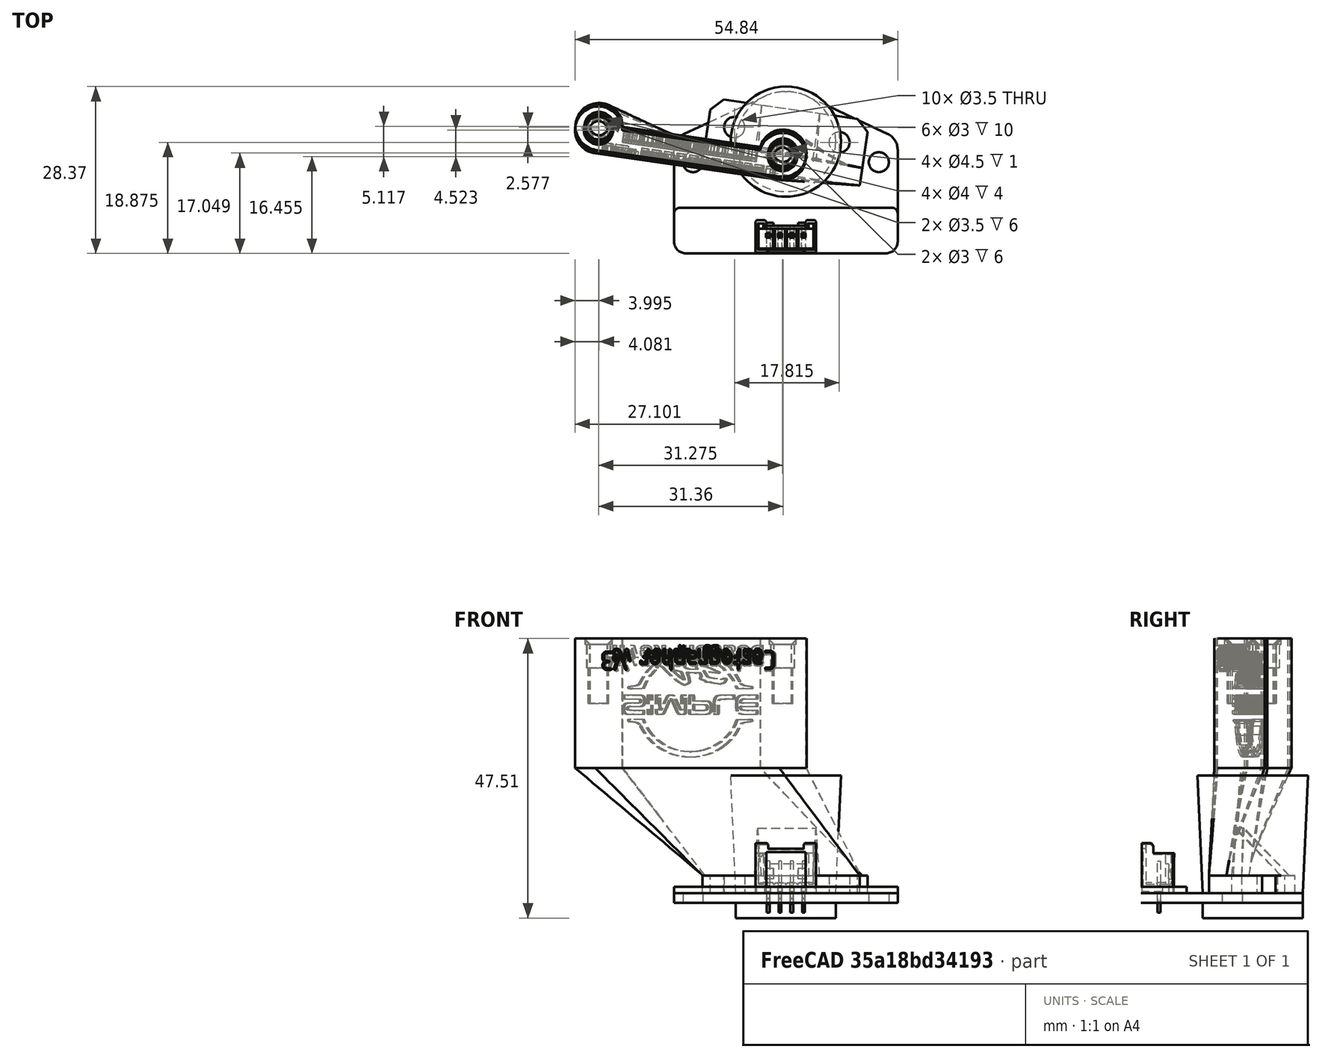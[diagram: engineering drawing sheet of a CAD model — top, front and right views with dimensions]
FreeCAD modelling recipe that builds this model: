
FCSTD DOCUMENT  (FreeCAD 1.2R20260324 (Git shallow))
Label: CartoBeaconMountEnder3V3SE
License: All rights reserved
LicenseURL: http://en.wikipedia.org/wiki/All_rights_reserved
objects: Sketcher::SketchObject×44, PartDesign::Pocket×19, PartDesign::Pad×10, PartDesign::AdditiveLoft×10, PartDesign::Chamfer×8, App::Point×7, Part::Feature×5, Part::Part2DObjectPython×5, PartDesign::Body×5, App::Part×2
note: 244 computed .brp shape members not serialized (recipe doc carries the construction recipe); baked Part::Feature solids carry a one-line shape summary decoded from their .brp

FEATURE [Part::Feature] Part__Feature  label="BeaconG_LP"
  shape: bbox 17 x 17 x 2.6 mm, 4 faces (baked)
FEATURE [Part::Feature] Part__Feature001  label="BeaconG_LP001"
  shape: bbox 18.75 x 18.75 x 20 mm, 4 faces (baked)
FEATURE [Part::Feature] Part__Feature002  label="BeaconG_LP002"
  shape: bbox 38 x 7.762 x 1.1 mm, 10 faces (baked)
FEATURE [Part::Feature] Part__Feature003  label="BeaconG_LP003"
  shape: bbox 38 x 27.5 x 1.611 mm, 18 faces (baked)
FEATURE [App::Part] BeaconG_LP  label="BeaconG_LP004"
  Group = -> [Part__Feature,Part__Feature001,Part__Feature002,Part__Feature003]
  Origin = -> Origin
  Placement = pos=(0,0,0) rot=(0,0,1;1.5708rad)
FEATURE [App::Point] Origin001
  Role = Origin
FEATURE [Part::Feature] Part__Feature004  label="353620450"
  Placement = pos=(4e-16,-16.1345,4.25) rot=(0,0.707107,0.707107;3.14159rad)
  shape: bbox 10.3 x 5.55 x 11.8 mm, 178 faces (baked)
FEATURE [App::Part] Beacon_Rev_H_Assm  label="Beacon Rev H Assm"
  Group = -> [BeaconG_LP,Part__Feature004]
  Origin = -> Origin002
  Placement = pos=(-14.8882,-23.3593,-85.3) rot=(0,0,1;4.71239rad)
FEATURE [App::Point] Origin003
  Role = Origin
FEATURE [App::Point] Origin009  label="Origin011"
  Role = Origin
FEATURE [Sketcher::SketchObject] Sketch011
  ArcFitTolerance = 1e-06
  AttachmentOffset = pos=(-16,-2,43.3) rot=(0,0,1;0rad)
  AttachmentSupport = -> [Origin008]
  ExternalTypes = [0,0]
  FullyConstrained = true
  MakeInternals = false
  MapMode = 5
  Placement = pos=(-16,-2,43.3) rot=(0,0,1;0rad)
  _ExternalGeoVersion = 0
  sketch-geometry (4):
    g0: ArcOfCircle CenterX=-15.8 CenterY=0 CenterZ=0 NormalX=0 NormalY=0 NormalZ=1 AngleXU=0 Radius=4 StartAngle=0.125328 EndAngle=4.71239
    g1: ArcOfCircle CenterX=15.8 CenterY=0 CenterZ=0 NormalX=0 NormalY=0 NormalZ=1 AngleXU=0 Radius=4 StartAngle=4.71239 EndAngle=9.29945
    g2: LineSegment StartX=-15.8 StartY=-4 StartZ=0 EndX=15.8 EndY=-4 EndZ=0
    g3: LineSegment StartX=-11.8314 StartY=0.5 StartZ=0 EndX=11.8314 EndY=0.5 EndZ=0
  constraints (12):
    c: DistanceX(g0,g1) = 31.6
    c: Vertical(g2,g1)
    c: Symmetric(g0,g1,g-2)
    c: Symmetric(g2,g2,g-2)
    c: Horizontal(g3)
    c: PointOnObject(g0,g-1)
    c: DistanceY(g2,g3) = 4.5
    c: DistanceY(g2,g0) = 4
    c: Coincident(g3,g1)
    c: Coincident(g1,g2)
    c: Coincident(g3,g0)
    c: Coincident(g0,g2)
FEATURE [Sketcher::SketchObject] Sketch013
  ArcFitTolerance = 1e-06
  AttachmentSupport = -> [Origin008]
  ExternalTypes = [0]
  FullyConstrained = true
  MakeInternals = false
  MapMode = 5
  _ExternalGeoVersion = 0
  expr: Constraints[11] = 5 + 3.5 / 2
  sketch-geometry (6):
    g0: LineSegment StartX=-13.5 StartY=-5.575 StartZ=0 EndX=13.5 EndY=-5.575 EndZ=0
    g1: LineSegment StartX=13.5 StartY=-5.575 StartZ=0 EndX=13.5 EndY=5.575 EndZ=0
    g2: Circle CenterX=-9 CenterY=1.175 CenterZ=0 NormalX=0 NormalY=0 NormalZ=1 AngleXU=0 Radius=1.75
    g3: Circle CenterX=9 CenterY=1.175 CenterZ=0 NormalX=0 NormalY=0 NormalZ=1 AngleXU=0 Radius=1.75
    g4: LineSegment StartX=-13.5 StartY=-5.575 StartZ=0 EndX=-13.5 EndY=5.575 EndZ=0
    g5: LineSegment StartX=-13.5 StartY=5.575 StartZ=0 EndX=13.5 EndY=5.575 EndZ=0
  constraints (16):
    c: Equal(g3,g2)
    c: Diameter(g3) = 3.5
    c: Symmetric(g2,g3,g-2)
    c: Coincident(g4,g0)
    c: Vertical(g4)
    c: Coincident(g5,g4)
    c: Coincident(g5,g1)
    c: Horizontal(g5)
    c: DistanceY(g4,g4) = 11.15
    c: Symmetric(g4,g0,g-1)
    c: DistanceX(g5,g5) = 27
    c: DistanceY(g0,g2) = 6.75
    c: DistanceX(g2,g3) = 18
    c: Horizontal(g0)
    c: Vertical(g1)
    c: Coincident(g1,g0)
FEATURE [PartDesign::Pad] Pad008
  Direction = (0,0,1)
  Length = 22
  Length2 = 10
  Profile = -> Sketch011
  ReferenceAxis = -> Sketch011 [N_Axis]
  Refine = true
  Reversed = true
  SideType = 0
  Suppressed = false
  Type = 0
  Type2 = 0
FEATURE [PartDesign::Pad] Pad009
  BaseFeature = -> Pad008
  Direction = (0,0,1)
  Length = 3
  Length2 = 10
  Profile = -> Sketch013
  ReferenceAxis = -> Sketch013 [N_Axis]
  Refine = true
  SideType = 0
  Suppressed = false
  Type = 0
  Type2 = 0
FEATURE [Sketcher::SketchObject] Sketch014
  ArcFitTolerance = 1e-06
  AttachmentSupport = -> [Pad009]
  ExternalGeometry = -> [Pad009]
  ExternalTypes = [0,0]
  FullyConstrained = true
  MakeInternals = false
  MapMode = 5
  Placement = pos=(0,0,3) rot=(0,0,1;0rad)
  _ExternalGeoVersion = 0
  sketch-geometry (4):
    g0: LineSegment StartX=-13.5 StartY=-5.575 StartZ=0 EndX=13.5 EndY=-5.575 EndZ=0
    g1: LineSegment StartX=13.5 StartY=-5.575 StartZ=0 EndX=13.5 EndY=-2.575 EndZ=0
    g2: LineSegment StartX=13.5 StartY=-2.575 StartZ=0 EndX=-13.5 EndY=-2.575 EndZ=0
    g3: LineSegment StartX=-13.5 StartY=-2.575 StartZ=0 EndX=-13.5 EndY=-5.575 EndZ=0
  constraints (11):
    c: Coincident(g0,g1)
    c: Coincident(g1,g2)
    c: Coincident(g2,g3)
    c: Coincident(g3,g0)
    c: Horizontal(g2)
    c: Vertical(g1)
    c: Vertical(g3)
    c: DistanceY(g1,g1) = 3
    c: Horizontal(g0)
    c: Coincident(g0,g-3)
    c: PointOnObject(g2,g-4)
FEATURE [Sketcher::SketchObject] MirroredSketch001
  ArcFitTolerance = 1e-06
  AttachmentOffset = pos=(14,-18,0) rot=(0,0,1;0rad)
  AttachmentSupport = -> [Pad009]
  ExternalTypes = [0]
  FullyConstrained = false
  MakeInternals = false
  MapMode = 5
  Placement = pos=(-14,-1.5,-18) rot=(0,0.707107,0.707107;3.14159rad)
  _ExternalGeoVersion = 0
  sketch-geometry (160):
    g0: BSplineCurve PolesCount=4 KnotsCount=2 Degree=3 IsPeriodic=0
    g1: BSplineCurve PolesCount=4 KnotsCount=2 Degree=3 IsPeriodic=0
    g2: BSplineCurve PolesCount=4 KnotsCount=2 Degree=3 IsPeriodic=0
    g3: BSplineCurve PolesCount=4 KnotsCount=2 Degree=3 IsPeriodic=0
    g4: BSplineCurve PolesCount=4 KnotsCount=2 Degree=3 IsPeriodic=0
    g5: BSplineCurve PolesCount=4 KnotsCount=2 Degree=3 IsPeriodic=0
    g6: BSplineCurve PolesCount=4 KnotsCount=2 Degree=3 IsPeriodic=0
    g7: BSplineCurve PolesCount=4 KnotsCount=2 Degree=3 IsPeriodic=0
    g8: BSplineCurve PolesCount=4 KnotsCount=2 Degree=3 IsPeriodic=0
    g9: BSplineCurve PolesCount=4 KnotsCount=2 Degree=3 IsPeriodic=0
    g10: BSplineCurve PolesCount=4 KnotsCount=2 Degree=3 IsPeriodic=0
    g11: BSplineCurve PolesCount=4 KnotsCount=2 Degree=3 IsPeriodic=0
    g12: BSplineCurve PolesCount=4 KnotsCount=2 Degree=3 IsPeriodic=0
    g13: BSplineCurve PolesCount=4 KnotsCount=2 Degree=3 IsPeriodic=0
    g14: BSplineCurve PolesCount=4 KnotsCount=2 Degree=3 IsPeriodic=0
    g15: BSplineCurve PolesCount=4 KnotsCount=2 Degree=3 IsPeriodic=0
    g16: BSplineCurve PolesCount=4 KnotsCount=2 Degree=3 IsPeriodic=0
    g17: BSplineCurve PolesCount=4 KnotsCount=2 Degree=3 IsPeriodic=0
    g18: BSplineCurve PolesCount=4 KnotsCount=2 Degree=3 IsPeriodic=0
    g19: BSplineCurve PolesCount=4 KnotsCount=2 Degree=3 IsPeriodic=0
    g20: BSplineCurve PolesCount=4 KnotsCount=2 Degree=3 IsPeriodic=0
    g21: BSplineCurve PolesCount=4 KnotsCount=2 Degree=3 IsPeriodic=0
    g22: BSplineCurve PolesCount=4 KnotsCount=2 Degree=3 IsPeriodic=0
    g23: BSplineCurve PolesCount=4 KnotsCount=2 Degree=3 IsPeriodic=0
    g24: BSplineCurve PolesCount=4 KnotsCount=2 Degree=3 IsPeriodic=0
    g25: BSplineCurve PolesCount=4 KnotsCount=2 Degree=3 IsPeriodic=0
    g26: BSplineCurve PolesCount=4 KnotsCount=2 Degree=3 IsPeriodic=0
    g27: BSplineCurve PolesCount=4 KnotsCount=2 Degree=3 IsPeriodic=0
    g28: BSplineCurve PolesCount=4 KnotsCount=2 Degree=3 IsPeriodic=0
    g29: BSplineCurve PolesCount=4 KnotsCount=2 Degree=3 IsPeriodic=0
    g30: BSplineCurve PolesCount=4 KnotsCount=2 Degree=3 IsPeriodic=0
    g31: BSplineCurve PolesCount=4 KnotsCount=2 Degree=3 IsPeriodic=0
    g32: BSplineCurve PolesCount=4 KnotsCount=2 Degree=3 IsPeriodic=0
    g33: BSplineCurve PolesCount=4 KnotsCount=2 Degree=3 IsPeriodic=0
    g34: BSplineCurve PolesCount=4 KnotsCount=2 Degree=3 IsPeriodic=0
    g35: BSplineCurve PolesCount=4 KnotsCount=2 Degree=3 IsPeriodic=0
    g36: BSplineCurve PolesCount=4 KnotsCount=2 Degree=3 IsPeriodic=0
    g37: BSplineCurve PolesCount=4 KnotsCount=2 Degree=3 IsPeriodic=0
    g38: BSplineCurve PolesCount=4 KnotsCount=2 Degree=3 IsPeriodic=0
    g39: BSplineCurve PolesCount=4 KnotsCount=2 Degree=3 IsPeriodic=0
    g40: BSplineCurve PolesCount=4 KnotsCount=2 Degree=3 IsPeriodic=0
    g41: BSplineCurve PolesCount=4 KnotsCount=2 Degree=3 IsPeriodic=0
    g42: BSplineCurve PolesCount=4 KnotsCount=2 Degree=3 IsPeriodic=0
    g43: BSplineCurve PolesCount=4 KnotsCount=2 Degree=3 IsPeriodic=0
    g44: BSplineCurve PolesCount=4 KnotsCount=2 Degree=3 IsPeriodic=0
    g45: BSplineCurve PolesCount=4 KnotsCount=2 Degree=3 IsPeriodic=0
    g46: BSplineCurve PolesCount=4 KnotsCount=2 Degree=3 IsPeriodic=0
    g47: BSplineCurve PolesCount=4 KnotsCount=2 Degree=3 IsPeriodic=0
    g48: BSplineCurve PolesCount=4 KnotsCount=2 Degree=3 IsPeriodic=0
    g49: BSplineCurve PolesCount=4 KnotsCount=2 Degree=3 IsPeriodic=0
    g50: BSplineCurve PolesCount=4 KnotsCount=2 Degree=3 IsPeriodic=0
    g51: BSplineCurve PolesCount=4 KnotsCount=2 Degree=3 IsPeriodic=0
    g52: BSplineCurve PolesCount=4 KnotsCount=2 Degree=3 IsPeriodic=0
    g53: BSplineCurve PolesCount=4 KnotsCount=2 Degree=3 IsPeriodic=0
    g54: BSplineCurve PolesCount=4 KnotsCount=2 Degree=3 IsPeriodic=0
    g55: BSplineCurve PolesCount=4 KnotsCount=2 Degree=3 IsPeriodic=0
    g56: BSplineCurve PolesCount=4 KnotsCount=2 Degree=3 IsPeriodic=0
    g57: BSplineCurve PolesCount=4 KnotsCount=2 Degree=3 IsPeriodic=0
    g58: BSplineCurve PolesCount=4 KnotsCount=2 Degree=3 IsPeriodic=0
    g59: BSplineCurve PolesCount=4 KnotsCount=2 Degree=3 IsPeriodic=0
    g60: BSplineCurve PolesCount=4 KnotsCount=2 Degree=3 IsPeriodic=0
    g61: BSplineCurve PolesCount=4 KnotsCount=2 Degree=3 IsPeriodic=0
    g62: BSplineCurve PolesCount=4 KnotsCount=2 Degree=3 IsPeriodic=0
    g63: BSplineCurve PolesCount=4 KnotsCount=2 Degree=3 IsPeriodic=0
    g64: BSplineCurve PolesCount=4 KnotsCount=2 Degree=3 IsPeriodic=0
    g65: BSplineCurve PolesCount=4 KnotsCount=2 Degree=3 IsPeriodic=0
    g66: BSplineCurve PolesCount=4 KnotsCount=2 Degree=3 IsPeriodic=0
    g67: BSplineCurve PolesCount=4 KnotsCount=2 Degree=3 IsPeriodic=0
    g68: BSplineCurve PolesCount=4 KnotsCount=2 Degree=3 IsPeriodic=0
    g69: BSplineCurve PolesCount=4 KnotsCount=2 Degree=3 IsPeriodic=0
    g70: BSplineCurve PolesCount=4 KnotsCount=2 Degree=3 IsPeriodic=0
    g71: BSplineCurve PolesCount=4 KnotsCount=2 Degree=3 IsPeriodic=0
    g72: BSplineCurve PolesCount=4 KnotsCount=2 Degree=3 IsPeriodic=0
    g73: BSplineCurve PolesCount=4 KnotsCount=2 Degree=3 IsPeriodic=0
    g74: BSplineCurve PolesCount=4 KnotsCount=2 Degree=3 IsPeriodic=0
    g75: BSplineCurve PolesCount=4 KnotsCount=2 Degree=3 IsPeriodic=0
    g76: BSplineCurve PolesCount=4 KnotsCount=2 Degree=3 IsPeriodic=0
    g77: BSplineCurve PolesCount=4 KnotsCount=2 Degree=3 IsPeriodic=0
    g78: BSplineCurve PolesCount=4 KnotsCount=2 Degree=3 IsPeriodic=0
    g79: BSplineCurve PolesCount=4 KnotsCount=2 Degree=3 IsPeriodic=0
    g80: BSplineCurve PolesCount=4 KnotsCount=2 Degree=3 IsPeriodic=0
    g81: BSplineCurve PolesCount=4 KnotsCount=2 Degree=3 IsPeriodic=0
    g82: BSplineCurve PolesCount=4 KnotsCount=2 Degree=3 IsPeriodic=0
    g83: BSplineCurve PolesCount=4 KnotsCount=2 Degree=3 IsPeriodic=0
    g84: BSplineCurve PolesCount=4 KnotsCount=2 Degree=3 IsPeriodic=0
    g85: BSplineCurve PolesCount=4 KnotsCount=2 Degree=3 IsPeriodic=0
    g86: BSplineCurve PolesCount=4 KnotsCount=2 Degree=3 IsPeriodic=0
    g87: BSplineCurve PolesCount=4 KnotsCount=2 Degree=3 IsPeriodic=0
    g88: BSplineCurve PolesCount=4 KnotsCount=2 Degree=3 IsPeriodic=0
    g89: BSplineCurve PolesCount=4 KnotsCount=2 Degree=3 IsPeriodic=0
    g90: BSplineCurve PolesCount=4 KnotsCount=2 Degree=3 IsPeriodic=0
    g91: BSplineCurve PolesCount=4 KnotsCount=2 Degree=3 IsPeriodic=0
    g92: BSplineCurve PolesCount=4 KnotsCount=2 Degree=3 IsPeriodic=0
    g93: BSplineCurve PolesCount=4 KnotsCount=2 Degree=3 IsPeriodic=0
    g94: BSplineCurve PolesCount=4 KnotsCount=2 Degree=3 IsPeriodic=0
    g95: BSplineCurve PolesCount=4 KnotsCount=2 Degree=3 IsPeriodic=0
    g96: BSplineCurve PolesCount=4 KnotsCount=2 Degree=3 IsPeriodic=0
    g97: BSplineCurve PolesCount=4 KnotsCount=2 Degree=3 IsPeriodic=0
    g98: BSplineCurve PolesCount=4 KnotsCount=2 Degree=3 IsPeriodic=0
    g99: BSplineCurve PolesCount=4 KnotsCount=2 Degree=3 IsPeriodic=0
    g100: BSplineCurve PolesCount=4 KnotsCount=2 Degree=3 IsPeriodic=0
    g101: BSplineCurve PolesCount=4 KnotsCount=2 Degree=3 IsPeriodic=0
    g102: BSplineCurve PolesCount=4 KnotsCount=2 Degree=3 IsPeriodic=0
    g103: BSplineCurve PolesCount=4 KnotsCount=2 Degree=3 IsPeriodic=0
    g104: BSplineCurve PolesCount=4 KnotsCount=2 Degree=3 IsPeriodic=0
    g105: BSplineCurve PolesCount=2 KnotsCount=2 Degree=1 IsPeriodic=0
    g106: BSplineCurve PolesCount=4 KnotsCount=2 Degree=3 IsPeriodic=0
    g107: BSplineCurve PolesCount=4 KnotsCount=2 Degree=3 IsPeriodic=0
    g108: BSplineCurve PolesCount=4 KnotsCount=2 Degree=3 IsPeriodic=0
    g109: BSplineCurve PolesCount=4 KnotsCount=2 Degree=3 IsPeriodic=0
    g110: BSplineCurve PolesCount=4 KnotsCount=2 Degree=3 IsPeriodic=0
    g111: BSplineCurve PolesCount=4 KnotsCount=2 Degree=3 IsPeriodic=0
    g112: BSplineCurve PolesCount=4 KnotsCount=2 Degree=3 IsPeriodic=0
    g113: BSplineCurve PolesCount=4 KnotsCount=2 Degree=3 IsPeriodic=0
    g114: BSplineCurve PolesCount=4 KnotsCount=2 Degree=3 IsPeriodic=0
    g115: BSplineCurve PolesCount=4 KnotsCount=2 Degree=3 IsPeriodic=0
    g116: BSplineCurve PolesCount=4 KnotsCount=2 Degree=3 IsPeriodic=0
    g117: BSplineCurve PolesCount=4 KnotsCount=2 Degree=3 IsPeriodic=0
    g118: BSplineCurve PolesCount=4 KnotsCount=2 Degree=3 IsPeriodic=0
    g119: BSplineCurve PolesCount=4 KnotsCount=2 Degree=3 IsPeriodic=0
    g120: BSplineCurve PolesCount=4 KnotsCount=2 Degree=3 IsPeriodic=0
    g121: BSplineCurve PolesCount=4 KnotsCount=2 Degree=3 IsPeriodic=0
    g122: BSplineCurve PolesCount=4 KnotsCount=2 Degree=3 IsPeriodic=0
    g123: BSplineCurve PolesCount=4 KnotsCount=2 Degree=3 IsPeriodic=0
    g124: BSplineCurve PolesCount=4 KnotsCount=2 Degree=3 IsPeriodic=0
    g125: BSplineCurve PolesCount=4 KnotsCount=2 Degree=3 IsPeriodic=0
    g126: BSplineCurve PolesCount=4 KnotsCount=2 Degree=3 IsPeriodic=0
    g127: BSplineCurve PolesCount=4 KnotsCount=2 Degree=3 IsPeriodic=0
    g128: BSplineCurve PolesCount=4 KnotsCount=2 Degree=3 IsPeriodic=0
    g129: BSplineCurve PolesCount=4 KnotsCount=2 Degree=3 IsPeriodic=0
    g130: BSplineCurve PolesCount=4 KnotsCount=2 Degree=3 IsPeriodic=0
    g131: BSplineCurve PolesCount=4 KnotsCount=2 Degree=3 IsPeriodic=0
    g132: BSplineCurve PolesCount=4 KnotsCount=2 Degree=3 IsPeriodic=0
    g133: BSplineCurve PolesCount=4 KnotsCount=2 Degree=3 IsPeriodic=0
    g134: BSplineCurve PolesCount=4 KnotsCount=2 Degree=3 IsPeriodic=0
    g135: BSplineCurve PolesCount=4 KnotsCount=2 Degree=3 IsPeriodic=0
    g136: BSplineCurve PolesCount=4 KnotsCount=2 Degree=3 IsPeriodic=0
    g137: BSplineCurve PolesCount=4 KnotsCount=2 Degree=3 IsPeriodic=0
    g138: BSplineCurve PolesCount=4 KnotsCount=2 Degree=3 IsPeriodic=0
    g139: BSplineCurve PolesCount=4 KnotsCount=2 Degree=3 IsPeriodic=0
    g140: BSplineCurve PolesCount=4 KnotsCount=2 Degree=3 IsPeriodic=0
    g141: BSplineCurve PolesCount=4 KnotsCount=2 Degree=3 IsPeriodic=0
    g142: BSplineCurve PolesCount=4 KnotsCount=2 Degree=3 IsPeriodic=0
    g143: BSplineCurve PolesCount=4 KnotsCount=2 Degree=3 IsPeriodic=0
    g144: BSplineCurve PolesCount=4 KnotsCount=2 Degree=3 IsPeriodic=0
    g145: BSplineCurve PolesCount=4 KnotsCount=2 Degree=3 IsPeriodic=0
    g146: BSplineCurve PolesCount=4 KnotsCount=2 Degree=3 IsPeriodic=0
    g147: BSplineCurve PolesCount=4 KnotsCount=2 Degree=3 IsPeriodic=0
    g148: BSplineCurve PolesCount=4 KnotsCount=2 Degree=3 IsPeriodic=0
    g149: BSplineCurve PolesCount=4 KnotsCount=2 Degree=3 IsPeriodic=0
    g150: BSplineCurve PolesCount=4 KnotsCount=2 Degree=3 IsPeriodic=0
    g151: BSplineCurve PolesCount=4 KnotsCount=2 Degree=3 IsPeriodic=0
    g152: BSplineCurve PolesCount=4 KnotsCount=2 Degree=3 IsPeriodic=0
    g153: BSplineCurve PolesCount=4 KnotsCount=2 Degree=3 IsPeriodic=0
    g154: BSplineCurve PolesCount=4 KnotsCount=2 Degree=3 IsPeriodic=0
    g155: BSplineCurve PolesCount=4 KnotsCount=2 Degree=3 IsPeriodic=0
    g156: BSplineCurve PolesCount=4 KnotsCount=2 Degree=3 IsPeriodic=0
    g157: BSplineCurve PolesCount=4 KnotsCount=2 Degree=3 IsPeriodic=0
    g158: BSplineCurve PolesCount=4 KnotsCount=2 Degree=3 IsPeriodic=0
    g159: BSplineCurve PolesCount=4 KnotsCount=2 Degree=3 IsPeriodic=0
  constraints (160):
    c: Coincident(g10,g11)
    c: Coincident(g4,g5)
    c: Coincident(g11,g12)
    c: Coincident(g0,g12)
    c: Coincident(g5,g6)
    c: Coincident(g9,g10)
    c: Coincident(g0,g1)
    c: Coincident(g8,g9)
    c: Coincident(g1,g2)
    c: Coincident(g3,g4)
    c: Coincident(g2,g3)
    c: Coincident(g7,g8)
    c: Coincident(g6,g7)
    c: Coincident(g79,g80)
    c: Coincident(g96,g97)
    c: Coincident(g109,g110)
    c: Coincident(g13,g26)
    c: Coincident(g110,g111)
    c: Coincident(g13,g14)
    c: Coincident(g136,g137)
    c: Coincident(g102,g103)
    c: Coincident(g82,g83)
    c: Coincident(g137,g138)
    c: Coincident(g103,g104)
    c: Coincident(g78,g79)
    c: Coincident(g83,g84)
    c: Coincident(g80,g81)
    c: Coincident(g25,g26)
    c: Coincident(g95,g96)
    c: Coincident(g108,g109)
    c: Coincident(g73,g81)
    c: Coincident(g14,g15)
    c: Coincident(g111,g112)
    c: Coincident(g127,g131)
    c: Coincident(g127,g128)
    c: Coincident(g87,g88)
    c: Coincident(g91,g92)
    c: Coincident(g112,g113)
    c: Coincident(g15,g16)
    c: Coincident(g130,g131)
    c: Coincident(g97,g98)
    c: Coincident(g88,g89)
    c: Coincident(g84,g85)
    c: Coincident(g92,g93)
    c: Coincident(g113,g114)
    c: Coincident(g16,g17)
    c: Coincident(g17,g18)
    c: Coincident(g114,g115)
    c: Coincident(g82,g100)
    c: Coincident(g129,g130)
    c: Coincident(g128,g129)
    c: Coincident(g73,g74)
    c: Coincident(g107,g108)
    c: Coincident(g135,g136)
    c: Coincident(g18,g19)
    c: Coincident(g19,g20)
    c: Coincident(g106,g107)
    c: Coincident(g24,g25)
    c: Coincident(g99,g100)
    c: Coincident(g106,g120)
    c: Coincident(g74,g75)
    c: Coincident(g75,g76)
    c: Coincident(g138,g139)
    c: Coincident(g119,g120)
    c: Coincident(g139,g140)
    c: Coincident(g132,g140)
    c: Coincident(g20,g21)
    c: Coincident(g98,g99)
    c: Coincident(g118,g119)
    c: Coincident(g132,g133)
    c: Coincident(g21,g22)
    c: Coincident(g115,g116)
    c: Coincident(g90,g91)
    c: Coincident(g89,g90)
    c: Coincident(g77,g78)
    c: Coincident(g134,g135)
    c: Coincident(g85,g86)
    c: Coincident(g86,g87)
    c: Coincident(g23,g24)
    c: Coincident(g104,g105)
    c: Coincident(g101,g102)
    c: Coincident(g94,g95)
    c: Coincident(g117,g118)
    c: Coincident(g101,g105)
    c: Coincident(g22,g23)
    c: Coincident(g93,g94)
    c: Coincident(g76,g77)
    c: Coincident(g133,g134)
    c: Coincident(g116,g117)
    c: Coincident(g148,g149)
    c: Coincident(g157,g158)
    c: Coincident(g158,g159)
    c: Coincident(g147,g148)
    c: Coincident(g146,g147)
    c: Coincident(g156,g157)
    c: Coincident(g149,g150)
    c: Coincident(g57,g58)
    c: Coincident(g155,g156)
    c: Coincident(g46,g47)
    c: Coincident(g56,g57)
    c: Coincident(g47,g48)
    c: Coincident(g48,g49)
    c: Coincident(g45,g46)
    c: Coincident(g150,g151)
    c: Coincident(g55,g56)
    c: Coincident(g49,g50)
    c: Coincident(g122,g123)
    c: Coincident(g43,g44)
    c: Coincident(g44,g45)
    c: Coincident(g54,g55)
    c: Coincident(g123,g124)
    c: Coincident(g42,g43)
    c: Coincident(g50,g51)
    c: Coincident(g124,g125)
    c: Coincident(g53,g54)
    c: Coincident(g40,g41)
    c: Coincident(g52,g53)
    c: Coincident(g51,g52)
    c: Coincident(g58,g59)
    c: Coincident(g121,g122)
    c: Coincident(g39,g40)
    c: Coincident(g41,g42)
    c: Coincident(g38,g39)
    c: Coincident(g125,g126)
    c: Coincident(g121,g126)
    c: Coincident(g32,g33)
    c: Coincident(g31,g32)
    c: Coincident(g153,g159)
    c: Coincident(g37,g38)
    c: Coincident(g59,g60)
    c: Coincident(g67,g68)
    c: Coincident(g154,g155)
    c: Coincident(g66,g67)
    c: Coincident(g36,g37)
    c: Coincident(g60,g61)
    c: Coincident(g153,g154)
    c: Coincident(g65,g66)
    c: Coincident(g68,g69)
    c: Coincident(g71,g72)
    c: Coincident(g141,g144)
    c: Coincident(g33,g34)
    c: Coincident(g64,g65)
    c: Coincident(g145,g146)
    c: Coincident(g141,g142)
    c: Coincident(g63,g64)
    c: Coincident(g145,g152)
    c: Coincident(g143,g144)
    c: Coincident(g61,g62)
    c: Coincident(g34,g35)
    c: Coincident(g29,g30)
    c: Coincident(g35,g36)
    c: Coincident(g62,g63)
    c: Coincident(g27,g30)
    c: Coincident(g69,g70)
    c: Coincident(g70,g71)
    c: Coincident(g142,g143)
    c: Coincident(g28,g29)
    c: Coincident(g151,g152)
    c: Coincident(g27,g28)
    c: Coincident(g31,g72)
FEATURE [Part::Part2DObjectPython] Clone2D002  label="MirroredSketch001 (2D)"  # Draft 2D object (typed FeaturePython)
  AttachmentOffset = pos=(4.3,23,0) rot=(0,0,-1;1.5708rad)
  AttachmentSupport = -> [Pad009]
  ForceCompound = false
  Fuse = false
  MapMode = 5
  Objects = -> [MirroredSketch001]
  Placement = pos=(-4.3,-1.5,23) rot=(-0.57735,0.57735,0.57735;2.0944rad)
  Scale = (0.65,0.65,0.65)
FEATURE [PartDesign::Pocket] Pocket005
  BaseFeature = -> Pad009
  Direction = (0,-1,2e-16)
  Length = 2
  Length2 = 5
  Profile = -> Clone2D002
  ReferenceAxis = -> Clone2D002 [N_Axis]
  Refine = true
  SideType = 0
  Suppressed = false
  Type = 0
  Type2 = 0
FEATURE [PartDesign::AdditiveLoft] AdditiveLoft002
  BaseFeature = -> Pocket005
  Closed = false
  Profile = -> Sketch014
  Refine = true
  Ruled = false
  Sections = -> [Pocket005]
  Suppressed = false
FEATURE [PartDesign::Chamfer] Chamfer
  Angle = 45
  Base = -> AdditiveLoft002 [Edge468,Edge489]
  BaseFeature = -> AdditiveLoft002
  ChamferType = 0
  FlipDirection = false
  Refine = true
  Size = 2
  Size2 = 1
  SupportTransform = false
  Suppressed = false
  UseAllEdges = false
FEATURE [Sketcher::SketchObject] Sketch016
  ArcFitTolerance = 1e-06
  AttachmentSupport = -> [Chamfer]
  ExternalGeometry = -> [Chamfer]
  ExternalTypes = [0,0]
  FullyConstrained = true
  MakeInternals = false
  MapMode = 5
  Placement = pos=(0,0,43.3) rot=(0,0,1;0rad)
  _ExternalGeoVersion = 0
  sketch-geometry (2):
    g0: Circle CenterX=-31.8 CenterY=-2 CenterZ=0 NormalX=0 NormalY=0 NormalZ=1 AngleXU=0 Radius=1.5
    g1: Circle CenterX=-0.2 CenterY=-2 CenterZ=0 NormalX=0 NormalY=0 NormalZ=1 AngleXU=0 Radius=1.5
  constraints (4):
    c: Coincident(g0,g-4)
    c: Coincident(g1,g-3)
    c: Equal(g1,g0)
    c: Diameter(g0) = 3
FEATURE [PartDesign::Pocket] Pocket006
  BaseFeature = -> Chamfer
  Direction = (0,0,-1)
  Length = 11
  Length2 = 5
  Profile = -> Sketch016
  ReferenceAxis = -> Sketch016 [N_Axis]
  Refine = true
  SideType = 0
  Suppressed = false
  Type = 0
  Type2 = 0
FEATURE [PartDesign::Chamfer] Chamfer001
  Angle = 45
  Base = -> Pocket006 [Edge194,Edge193]
  BaseFeature = -> Pocket006
  ChamferType = 0
  FlipDirection = false
  Refine = true
  Size = 1
  Size2 = 1
  SupportTransform = false
  Suppressed = false
  UseAllEdges = false
FEATURE [Sketcher::SketchObject] Sketch017
  ArcFitTolerance = 1e-06
  AttachmentSupport = -> [Chamfer001]
  ExternalGeometry = -> [Chamfer001]
  ExternalTypes = [0,0]
  FullyConstrained = true
  MakeInternals = false
  MapMode = 5
  Placement = pos=(0,0,3) rot=(0,0,1;0rad)
  _ExternalGeoVersion = 0
  sketch-geometry (4):
    g0: LineSegment StartX=-5 StartY=-2.575 StartZ=0 EndX=5 EndY=-2.575 EndZ=0
    g1: LineSegment StartX=5 StartY=-2.575 StartZ=0 EndX=5 EndY=5.575 EndZ=0
    g2: LineSegment StartX=5 StartY=5.575 StartZ=0 EndX=-5 EndY=5.575 EndZ=0
    g3: LineSegment StartX=-5 StartY=5.575 StartZ=0 EndX=-5 EndY=-2.575 EndZ=0
  constraints (11):
    c: Coincident(g0,g1)
    c: Coincident(g1,g2)
    c: Coincident(g2,g3)
    c: Coincident(g3,g0)
    c: Horizontal(g0)
    c: Vertical(g1)
    c: Vertical(g3)
    c: PointOnObject(g0,g-3)
    c: PointOnObject(g1,g-4)
    c: DistanceX(g2,g2) = 10
    c: Symmetric(g1,g2,g-2)
FEATURE [Sketcher::SketchObject] Sketch018
  ArcFitTolerance = 1e-06
  AttachmentSupport = -> [Chamfer001]
  ExternalGeometry = -> [Chamfer001]
  ExternalTypes = [0]
  FullyConstrained = true
  MakeInternals = false
  MapMode = 5
  Placement = pos=(1e-16,-2.74177,0.16106) rot=(0,0.727545,0.68606;3.14159rad)
  _ExternalGeoVersion = 0
  sketch-geometry (4):
    g0: LineSegment StartX=-5.5 StartY=10.9438 StartZ=0 EndX=-5.5 EndY=10.8438 EndZ=0
    g1: LineSegment StartX=-5.5 StartY=10.8438 StartZ=0 EndX=4.5 EndY=10.8438 EndZ=0
    g2: LineSegment StartX=4.5 StartY=10.8438 StartZ=0 EndX=4.5 EndY=10.9438 EndZ=0
    g3: LineSegment StartX=4.5 StartY=10.9438 StartZ=0 EndX=-5.5 EndY=10.9438 EndZ=0
  constraints (12):
    c: Coincident(g0,g1)
    c: Coincident(g1,g2)
    c: Coincident(g2,g3)
    c: Coincident(g3,g0)
    c: Vertical(g0)
    c: Vertical(g2)
    c: Horizontal(g1)
    c: Horizontal(g3)
    c: DistanceX(g3,g3) = 10
    c: DistanceY(g2,g2) = 0.1
    c: DistanceY(g-3,g0) = 8
    c: DistanceX(g-3,g0) = 8
FEATURE [PartDesign::AdditiveLoft] AdditiveLoft003
  BaseFeature = -> Chamfer001
  Closed = false
  Profile = -> Sketch017
  Refine = true
  Ruled = false
  Sections = -> [Sketch018]
  Suppressed = false
FEATURE [Sketcher::SketchObject] Sketch
  ArcFitTolerance = 1e-06
  AttachmentSupport = -> [AdditiveLoft003]
  ExternalGeometry = -> [AdditiveLoft003]
  ExternalTypes = [0,0]
  FullyConstrained = false
  MakeInternals = false
  MapMode = 5
  Placement = pos=(0,-6,0) rot=(1,0,0;1.5708rad)
  _ExternalGeoVersion = 0
  sketch-geometry (256):
    g0: LineSegment [constr] StartX=-3.2 StartY=42.193 StartZ=0 EndX=-28.8 EndY=42.193 EndZ=0
    g1: BSplineCurve PolesCount=3 KnotsCount=2 Degree=2 IsPeriodic=0
    g2: BSplineCurve PolesCount=3 KnotsCount=2 Degree=2 IsPeriodic=0
    g3: BSplineCurve PolesCount=3 KnotsCount=2 Degree=2 IsPeriodic=0
    g4: LineSegment StartX=-4.39844 StartY=38.9376 StartZ=0 EndX=-3.86003 EndY=38.9376 EndZ=0
    g5: BSplineCurve PolesCount=3 KnotsCount=2 Degree=2 IsPeriodic=0
    g6: BSplineCurve PolesCount=3 KnotsCount=2 Degree=2 IsPeriodic=0
    g7: LineSegment StartX=-3.46115 StartY=39.3364 StartZ=0 EndX=-3.46115 EndY=40.703 EndZ=0
    g8: BSplineCurve PolesCount=3 KnotsCount=2 Degree=2 IsPeriodic=0
    g9: BSplineCurve PolesCount=3 KnotsCount=2 Degree=2 IsPeriodic=0
    g10: LineSegment StartX=-3.81889 StartY=41.118 StartZ=0 EndX=-4.4199 EndY=41.118 EndZ=0
    g11: BSplineCurve PolesCount=3 KnotsCount=2 Degree=2 IsPeriodic=0
    g12: BSplineCurve PolesCount=3 KnotsCount=2 Degree=2 IsPeriodic=0
    g13: LineSegment StartX=-4.41811 StartY=41.372 StartZ=0 EndX=-3.80816 EndY=41.372 EndZ=0
    g14: BSplineCurve PolesCount=3 KnotsCount=2 Degree=2 IsPeriodic=0
    g15: BSplineCurve PolesCount=3 KnotsCount=2 Degree=2 IsPeriodic=0
    g16: LineSegment StartX=-3.2 StartY=40.7173 StartZ=0 EndX=-3.2 EndY=39.3168 EndZ=0
    g17: BSplineCurve PolesCount=3 KnotsCount=2 Degree=2 IsPeriodic=0
    g18: BSplineCurve PolesCount=3 KnotsCount=2 Degree=2 IsPeriodic=0
    g19: BSplineCurve PolesCount=3 KnotsCount=2 Degree=2 IsPeriodic=0
    g20: BSplineCurve PolesCount=3 KnotsCount=2 Degree=2 IsPeriodic=0
    g21: BSplineCurve PolesCount=3 KnotsCount=2 Degree=2 IsPeriodic=0
    g22: BSplineCurve PolesCount=3 KnotsCount=2 Degree=2 IsPeriodic=0
    g23: LineSegment StartX=-5.44304 StartY=41.1073 StartZ=0 EndX=-5.99039 EndY=41.1073 EndZ=0
    g24: LineSegment StartX=-5.99039 StartY=41.1073 StartZ=0 EndX=-5.99039 EndY=40.5528 EndZ=0
    g25: LineSegment StartX=-5.99039 StartY=40.5528 StartZ=0 EndX=-5.46808 EndY=40.5528 EndZ=0
    g26: BSplineCurve PolesCount=3 KnotsCount=2 Degree=2 IsPeriodic=0
    g27: BSplineCurve PolesCount=3 KnotsCount=2 Degree=2 IsPeriodic=0
    g28: LineSegment StartX=-5.18189 StartY=39.4795 StartZ=0 EndX=-5.73818 EndY=39.4795 EndZ=0
    g29: BSplineCurve PolesCount=3 KnotsCount=2 Degree=2 IsPeriodic=0
    g30: BSplineCurve PolesCount=3 KnotsCount=2 Degree=2 IsPeriodic=0
    g31: LineSegment StartX=-6.25869 StartY=40.0072 StartZ=0 EndX=-6.25869 EndY=41.2092 EndZ=0
    g32: BSplineCurve PolesCount=3 KnotsCount=2 Degree=2 IsPeriodic=0
    g33: BSplineCurve PolesCount=3 KnotsCount=2 Degree=2 IsPeriodic=0
    g34: LineSegment StartX=-6.10486 StartY=41.3774 StartZ=0 EndX=-5.42515 EndY=41.3774 EndZ=0
    g35: BSplineCurve PolesCount=3 KnotsCount=2 Degree=2 IsPeriodic=0
    g36: BSplineCurve PolesCount=3 KnotsCount=2 Degree=2 IsPeriodic=0
    g37: BSplineCurve PolesCount=3 KnotsCount=2 Degree=2 IsPeriodic=0
    g38: BSplineCurve PolesCount=3 KnotsCount=2 Degree=2 IsPeriodic=0
    g39: LineSegment StartX=-5.43231 StartY=40.2934 StartZ=0 EndX=-5.99039 EndY=40.2934 EndZ=0
    g40: LineSegment StartX=-5.99039 StartY=40.2934 StartZ=0 EndX=-5.99039 EndY=39.9643 EndZ=0
    g41: BSplineCurve PolesCount=3 KnotsCount=2 Degree=2 IsPeriodic=0
    g42: BSplineCurve PolesCount=3 KnotsCount=2 Degree=2 IsPeriodic=0
    g43: LineSegment StartX=-5.73102 StartY=39.7407 StartZ=0 EndX=-5.18189 EndY=39.7407 EndZ=0
    g44: BSplineCurve PolesCount=3 KnotsCount=2 Degree=2 IsPeriodic=0
    g45: BSplineCurve PolesCount=3 KnotsCount=2 Degree=2 IsPeriodic=0
    g46: BSplineCurve PolesCount=3 KnotsCount=2 Degree=2 IsPeriodic=0
    g47: BSplineCurve PolesCount=3 KnotsCount=2 Degree=2 IsPeriodic=0
    g48: BSplineCurve PolesCount=3 KnotsCount=2 Degree=2 IsPeriodic=0
    g49: BSplineCurve PolesCount=3 KnotsCount=2 Degree=2 IsPeriodic=0
    g50: BSplineCurve PolesCount=3 KnotsCount=2 Degree=2 IsPeriodic=0
    g51: LineSegment StartX=-7.54299 StartY=39.7425 StartZ=0 EndX=-6.98849 EndY=39.7425 EndZ=0
    g52: LineSegment StartX=-6.98849 StartY=39.7425 StartZ=0 EndX=-6.98849 EndY=41.2307 EndZ=0
    g53: BSplineCurve PolesCount=3 KnotsCount=2 Degree=2 IsPeriodic=0
    g54: BSplineCurve PolesCount=3 KnotsCount=2 Degree=2 IsPeriodic=0
    g55: BSplineCurve PolesCount=3 KnotsCount=2 Degree=2 IsPeriodic=0
    g56: BSplineCurve PolesCount=3 KnotsCount=2 Degree=2 IsPeriodic=0
    g57: BSplineCurve PolesCount=3 KnotsCount=2 Degree=2 IsPeriodic=0
    g58: BSplineCurve PolesCount=3 KnotsCount=2 Degree=2 IsPeriodic=0
    g59: BSplineCurve PolesCount=3 KnotsCount=2 Degree=2 IsPeriodic=0
    g60: BSplineCurve PolesCount=3 KnotsCount=2 Degree=2 IsPeriodic=0
    g61: BSplineCurve PolesCount=3 KnotsCount=2 Degree=2 IsPeriodic=0
    g62: LineSegment StartX=-9.02225 StartY=39.7461 StartZ=0 EndX=-8.61621 EndY=39.7461 EndZ=0
    g63: LineSegment StartX=-8.61621 StartY=39.7461 StartZ=0 EndX=-8.61621 EndY=41.2396 EndZ=0
    g64: BSplineCurve PolesCount=3 KnotsCount=2 Degree=2 IsPeriodic=0
    g65: BSplineCurve PolesCount=3 KnotsCount=2 Degree=2 IsPeriodic=0
    g66: LineSegment StartX=-8.35864 StartY=41.2271 StartZ=0 EndX=-8.35864 EndY=39.7461 EndZ=0
    g67: LineSegment StartX=-8.35864 StartY=39.7461 StartZ=0 EndX=-8.22269 EndY=39.7461 EndZ=0
    g68: BSplineCurve PolesCount=3 KnotsCount=2 Degree=2 IsPeriodic=0
    g69: BSplineCurve PolesCount=3 KnotsCount=2 Degree=2 IsPeriodic=0
    g70: LineSegment StartX=-8.22091 StartY=39.4921 StartZ=0 EndX=-8.35864 EndY=39.4921 EndZ=0
    g71: LineSegment StartX=-8.35864 StartY=39.4921 StartZ=0 EndX=-8.35864 EndY=38.8106 EndZ=0
    g72: BSplineCurve PolesCount=3 KnotsCount=2 Degree=2 IsPeriodic=0
    g73: LineSegment StartX=-9.7431 StartY=40.1628 StartZ=0 EndX=-9.7431 EndY=40.712 EndZ=0
    g74: BSplineCurve PolesCount=3 KnotsCount=2 Degree=2 IsPeriodic=0
    g75: BSplineCurve PolesCount=3 KnotsCount=2 Degree=2 IsPeriodic=0
    g76: BSplineCurve PolesCount=3 KnotsCount=2 Degree=2 IsPeriodic=0
    g77: BSplineCurve PolesCount=3 KnotsCount=2 Degree=2 IsPeriodic=0
    g78: LineSegment StartX=-10.5748 StartY=40.6565 StartZ=0 EndX=-10.5748 EndY=40.2004 EndZ=0
    g79: BSplineCurve PolesCount=3 KnotsCount=2 Degree=2 IsPeriodic=0
    g80: BSplineCurve PolesCount=3 KnotsCount=2 Degree=2 IsPeriodic=0
    g81: BSplineCurve PolesCount=3 KnotsCount=2 Degree=2 IsPeriodic=0
    g82: BSplineCurve PolesCount=3 KnotsCount=2 Degree=2 IsPeriodic=0
    g83: BSplineCurve PolesCount=3 KnotsCount=2 Degree=2 IsPeriodic=0
    g84: LineSegment StartX=-10.8271 StartY=40.0859 StartZ=0 EndX=-10.8271 EndY=40.7084 EndZ=0
    g85: BSplineCurve PolesCount=3 KnotsCount=2 Degree=2 IsPeriodic=0
    g86: BSplineCurve PolesCount=3 KnotsCount=2 Degree=2 IsPeriodic=0
    g87: BSplineCurve PolesCount=3 KnotsCount=2 Degree=2 IsPeriodic=0
    g88: BSplineCurve PolesCount=3 KnotsCount=2 Degree=2 IsPeriodic=0
    g89: LineSegment StartX=-9.48731 StartY=40.6994 StartZ=0 EndX=-9.48731 EndY=40.1145 EndZ=0
    g90: BSplineCurve PolesCount=3 KnotsCount=2 Degree=2 IsPeriodic=0
    g91: BSplineCurve PolesCount=3 KnotsCount=2 Degree=2 IsPeriodic=0
    g92: BSplineCurve PolesCount=3 KnotsCount=2 Degree=2 IsPeriodic=0
    g93: BSplineCurve PolesCount=3 KnotsCount=2 Degree=2 IsPeriodic=0
    g94: LineSegment StartX=-11.5461 StartY=40.0483 StartZ=0 EndX=-11.5461 EndY=40.7942 EndZ=0
    g95: BSplineCurve PolesCount=3 KnotsCount=2 Degree=2 IsPeriodic=0
    g96: BSplineCurve PolesCount=3 KnotsCount=2 Degree=2 IsPeriodic=0
    g97: LineSegment StartX=-11.843 StartY=41.118 StartZ=0 EndX=-12.3725 EndY=41.118 EndZ=0
    g98: LineSegment StartX=-12.3725 StartY=41.118 StartZ=0 EndX=-12.3725 EndY=39.7478 EndZ=0
    g99: LineSegment StartX=-12.3725 StartY=39.7478 StartZ=0 EndX=-11.8556 EndY=39.7478 EndZ=0
    g100: BSplineCurve PolesCount=3 KnotsCount=2 Degree=2 IsPeriodic=0
    g101: BSplineCurve PolesCount=3 KnotsCount=2 Degree=2 IsPeriodic=0
    g102: BSplineCurve PolesCount=3 KnotsCount=2 Degree=2 IsPeriodic=0
    g103: BSplineCurve PolesCount=3 KnotsCount=2 Degree=2 IsPeriodic=0
    g104: BSplineCurve PolesCount=3 KnotsCount=2 Degree=2 IsPeriodic=0
    g105: BSplineCurve PolesCount=3 KnotsCount=2 Degree=2 IsPeriodic=0
    g106: BSplineCurve PolesCount=3 KnotsCount=2 Degree=2 IsPeriodic=0
    g107: BSplineCurve PolesCount=3 KnotsCount=2 Degree=2 IsPeriodic=0
    g108: BSplineCurve PolesCount=3 KnotsCount=2 Degree=2 IsPeriodic=0
    g109: BSplineCurve PolesCount=3 KnotsCount=2 Degree=2 IsPeriodic=0
    g110: LineSegment StartX=-12.3671 StartY=41.6796 StartZ=0 EndX=-12.3671 EndY=41.3774 EndZ=0
    g111: BSplineCurve PolesCount=3 KnotsCount=2 Degree=2 IsPeriodic=0
    g112: BSplineCurve PolesCount=3 KnotsCount=2 Degree=2 IsPeriodic=0
    g113: BSplineCurve PolesCount=3 KnotsCount=2 Degree=2 IsPeriodic=0
    g114: BSplineCurve PolesCount=3 KnotsCount=2 Degree=2 IsPeriodic=0
    g115: BSplineCurve PolesCount=3 KnotsCount=2 Degree=2 IsPeriodic=0
    g116: BSplineCurve PolesCount=3 KnotsCount=2 Degree=2 IsPeriodic=0
    g117: BSplineCurve PolesCount=3 KnotsCount=2 Degree=2 IsPeriodic=0
    g118: BSplineCurve PolesCount=3 KnotsCount=2 Degree=2 IsPeriodic=0
    g119: BSplineCurve PolesCount=3 KnotsCount=2 Degree=2 IsPeriodic=0
    g120: BSplineCurve PolesCount=3 KnotsCount=2 Degree=2 IsPeriodic=0
    g121: BSplineCurve PolesCount=3 KnotsCount=2 Degree=2 IsPeriodic=0
    g122: BSplineCurve PolesCount=3 KnotsCount=2 Degree=2 IsPeriodic=0
    g123: BSplineCurve PolesCount=3 KnotsCount=2 Degree=2 IsPeriodic=0
    g124: LineSegment StartX=-13.9519 StartY=39.7425 StartZ=0 EndX=-13.3974 EndY=39.7425 EndZ=0
    g125: LineSegment StartX=-13.3974 StartY=39.7425 StartZ=0 EndX=-13.3974 EndY=41.2307 EndZ=0
    g126: BSplineCurve PolesCount=3 KnotsCount=2 Degree=2 IsPeriodic=0
    g127: BSplineCurve PolesCount=3 KnotsCount=2 Degree=2 IsPeriodic=0
    g128: BSplineCurve PolesCount=3 KnotsCount=2 Degree=2 IsPeriodic=0
    g129: BSplineCurve PolesCount=3 KnotsCount=2 Degree=2 IsPeriodic=0
    g130: BSplineCurve PolesCount=3 KnotsCount=2 Degree=2 IsPeriodic=0
    g131: BSplineCurve PolesCount=3 KnotsCount=2 Degree=2 IsPeriodic=0
    g132: BSplineCurve PolesCount=3 KnotsCount=2 Degree=2 IsPeriodic=0
    g133: LineSegment StartX=-15.1074 StartY=41.1073 StartZ=0 EndX=-15.6548 EndY=41.1073 EndZ=0
    g134: LineSegment StartX=-15.6548 StartY=41.1073 StartZ=0 EndX=-15.6548 EndY=40.5528 EndZ=0
    g135: LineSegment StartX=-15.6548 StartY=40.5528 StartZ=0 EndX=-15.1325 EndY=40.5528 EndZ=0
    g136: BSplineCurve PolesCount=3 KnotsCount=2 Degree=2 IsPeriodic=0
    g137: BSplineCurve PolesCount=3 KnotsCount=2 Degree=2 IsPeriodic=0
    g138: LineSegment StartX=-14.8463 StartY=39.4795 StartZ=0 EndX=-15.4026 EndY=39.4795 EndZ=0
    g139: BSplineCurve PolesCount=3 KnotsCount=2 Degree=2 IsPeriodic=0
    g140: BSplineCurve PolesCount=3 KnotsCount=2 Degree=2 IsPeriodic=0
    g141: LineSegment StartX=-15.9231 StartY=40.0072 StartZ=0 EndX=-15.9231 EndY=41.2092 EndZ=0
    g142: BSplineCurve PolesCount=3 KnotsCount=2 Degree=2 IsPeriodic=0
    g143: BSplineCurve PolesCount=3 KnotsCount=2 Degree=2 IsPeriodic=0
    g144: LineSegment StartX=-15.7693 StartY=41.3774 StartZ=0 EndX=-15.0895 EndY=41.3774 EndZ=0
    g145: BSplineCurve PolesCount=3 KnotsCount=2 Degree=2 IsPeriodic=0
    g146: BSplineCurve PolesCount=3 KnotsCount=2 Degree=2 IsPeriodic=0
    g147: BSplineCurve PolesCount=3 KnotsCount=2 Degree=2 IsPeriodic=0
    g148: BSplineCurve PolesCount=3 KnotsCount=2 Degree=2 IsPeriodic=0
    g149: LineSegment StartX=-15.0967 StartY=40.2934 StartZ=0 EndX=-15.6548 EndY=40.2934 EndZ=0
    g150: LineSegment StartX=-15.6548 StartY=40.2934 StartZ=0 EndX=-15.6548 EndY=39.9643 EndZ=0
    g151: BSplineCurve PolesCount=3 KnotsCount=2 Degree=2 IsPeriodic=0
    g152: BSplineCurve PolesCount=3 KnotsCount=2 Degree=2 IsPeriodic=0
    g153: LineSegment StartX=-15.3954 StartY=39.7407 StartZ=0 EndX=-14.8463 EndY=39.7407 EndZ=0
    g154: BSplineCurve PolesCount=3 KnotsCount=2 Degree=2 IsPeriodic=0
    g155: BSplineCurve PolesCount=3 KnotsCount=2 Degree=2 IsPeriodic=0
    g156: LineSegment StartX=-17.515 StartY=40.83 StartZ=0 EndX=-17.515 EndY=40.0466 EndZ=0
    g157: BSplineCurve PolesCount=3 KnotsCount=2 Degree=2 IsPeriodic=0
    g158: BSplineCurve PolesCount=3 KnotsCount=2 Degree=2 IsPeriodic=0
    g159: LineSegment StartX=-17.2414 StartY=39.7532 StartZ=0 EndX=-16.6869 EndY=39.7532 EndZ=0
    g160: LineSegment StartX=-16.6869 StartY=39.7532 StartZ=0 EndX=-16.6869 EndY=41.1198 EndZ=0
    g161: LineSegment StartX=-16.6869 StartY=41.1198 StartZ=0 EndX=-17.261 EndY=41.1198 EndZ=0
    g162: BSplineCurve PolesCount=3 KnotsCount=2 Degree=2 IsPeriodic=0
    g163: BSplineCurve PolesCount=3 KnotsCount=2 Degree=2 IsPeriodic=0
    g164: BSplineCurve PolesCount=3 KnotsCount=2 Degree=2 IsPeriodic=0
    g165: BSplineCurve PolesCount=3 KnotsCount=2 Degree=2 IsPeriodic=0
    g166: BSplineCurve PolesCount=3 KnotsCount=2 Degree=2 IsPeriodic=0
    g167: BSplineCurve PolesCount=3 KnotsCount=2 Degree=2 IsPeriodic=0
    g168: BSplineCurve PolesCount=3 KnotsCount=2 Degree=2 IsPeriodic=0
    g169: LineSegment StartX=-17.2736 StartY=41.3774 StartZ=0 EndX=-16.6869 EndY=41.3774 EndZ=0
    g170: LineSegment StartX=-16.6869 StartY=41.3774 StartZ=0 EndX=-16.6869 EndY=42.0302 EndZ=0
    g171: BSplineCurve PolesCount=3 KnotsCount=2 Degree=2 IsPeriodic=0
    g172: BSplineCurve PolesCount=3 KnotsCount=2 Degree=2 IsPeriodic=0
    g173: BSplineCurve PolesCount=3 KnotsCount=2 Degree=2 IsPeriodic=0
    g174: BSplineCurve PolesCount=3 KnotsCount=2 Degree=2 IsPeriodic=0
    g175: BSplineCurve PolesCount=3 KnotsCount=2 Degree=2 IsPeriodic=0
    g176: LineSegment StartX=-18.5435 StartY=38.8195 StartZ=0 EndX=-18.5435 EndY=39.4813 EndZ=0
    g177: LineSegment StartX=-18.5435 StartY=39.4813 StartZ=0 EndX=-19.098 EndY=39.4813 EndZ=0
    g178: BSplineCurve PolesCount=3 KnotsCount=2 Degree=2 IsPeriodic=0
    g179: BSplineCurve PolesCount=3 KnotsCount=2 Degree=2 IsPeriodic=0
    g180: LineSegment StartX=-19.6257 StartY=40.0161 StartZ=0 EndX=-19.6257 EndY=41.2271 EndZ=0
    g181: BSplineCurve PolesCount=3 KnotsCount=2 Degree=2 IsPeriodic=0
    g182: BSplineCurve PolesCount=3 KnotsCount=2 Degree=2 IsPeriodic=0
    g183: LineSegment StartX=-19.3699 StartY=41.2235 StartZ=0 EndX=-19.3699 EndY=40.0466 EndZ=0
    g184: BSplineCurve PolesCount=3 KnotsCount=2 Degree=2 IsPeriodic=0
    g185: LineSegment StartX=-19.0551 StartY=39.7389 StartZ=0 EndX=-18.5435 EndY=39.7389 EndZ=0
    g186: LineSegment StartX=-18.5435 StartY=39.7389 StartZ=0 EndX=-18.5435 EndY=41.2217 EndZ=0
    g187: BSplineCurve PolesCount=3 KnotsCount=2 Degree=2 IsPeriodic=0
    g188: BSplineCurve PolesCount=3 KnotsCount=2 Degree=2 IsPeriodic=0
    g189: LineSegment StartX=-18.2824 StartY=41.2128 StartZ=0 EndX=-18.2824 EndY=38.8267 EndZ=0
    g190: LineSegment StartX=-20.3591 StartY=40.297 StartZ=0 EndX=-21.1801 EndY=40.297 EndZ=0
    g191: BSplineCurve PolesCount=3 KnotsCount=2 Degree=2 IsPeriodic=0
    g192: BSplineCurve PolesCount=3 KnotsCount=2 Degree=2 IsPeriodic=0
    g193: BSplineCurve PolesCount=3 KnotsCount=2 Degree=2 IsPeriodic=0
    g194: BSplineCurve PolesCount=3 KnotsCount=2 Degree=2 IsPeriodic=0
    g195: BSplineCurve PolesCount=3 KnotsCount=2 Degree=2 IsPeriodic=0
    g196: BSplineCurve PolesCount=3 KnotsCount=2 Degree=2 IsPeriodic=0
    g197: BSplineCurve PolesCount=3 KnotsCount=2 Degree=2 IsPeriodic=0
    g198: BSplineCurve PolesCount=3 KnotsCount=2 Degree=2 IsPeriodic=0
    g199: LineSegment StartX=-21.4359 StartY=40.0823 StartZ=0 EndX=-21.4359 EndY=40.4222 EndZ=0
    g200: BSplineCurve PolesCount=3 KnotsCount=2 Degree=2 IsPeriodic=0
    g201: LineSegment StartX=-21.316 StartY=40.551 StartZ=0 EndX=-20.3555 EndY=40.551 EndZ=0
    g202: LineSegment StartX=-20.3555 StartY=40.551 StartZ=0 EndX=-20.3555 EndY=40.7871 EndZ=0
    g203: BSplineCurve PolesCount=3 KnotsCount=2 Degree=2 IsPeriodic=0
    g204: LineSegment StartX=-20.6345 StartY=41.1162 StartZ=0 EndX=-21.2838 EndY=41.1162 EndZ=0
    g205: BSplineCurve PolesCount=3 KnotsCount=2 Degree=2 IsPeriodic=0
    g206: BSplineCurve PolesCount=3 KnotsCount=2 Degree=2 IsPeriodic=0
    g207: LineSegment StartX=-21.2856 StartY=41.3774 StartZ=0 EndX=-20.6274 EndY=41.3774 EndZ=0
    g208: BSplineCurve PolesCount=3 KnotsCount=2 Degree=2 IsPeriodic=0
    g209: BSplineCurve PolesCount=3 KnotsCount=2 Degree=2 IsPeriodic=0
    g210: BSplineCurve PolesCount=3 KnotsCount=2 Degree=2 IsPeriodic=0
    g211: BSplineCurve PolesCount=3 KnotsCount=2 Degree=2 IsPeriodic=0
    g212: BSplineCurve PolesCount=3 KnotsCount=2 Degree=2 IsPeriodic=0
    g213: BSplineCurve PolesCount=3 KnotsCount=2 Degree=2 IsPeriodic=0
    g214: BSplineCurve PolesCount=3 KnotsCount=2 Degree=2 IsPeriodic=0
    g215: BSplineCurve PolesCount=3 KnotsCount=2 Degree=2 IsPeriodic=0
    g216: BSplineCurve PolesCount=3 KnotsCount=2 Degree=2 IsPeriodic=0
    g217: BSplineCurve PolesCount=3 KnotsCount=2 Degree=2 IsPeriodic=0
    g218: LineSegment StartX=-22.7255 StartY=39.7425 StartZ=0 EndX=-22.171 EndY=39.7425 EndZ=0
    g219: LineSegment StartX=-22.171 StartY=39.7425 StartZ=0 EndX=-22.171 EndY=41.2307 EndZ=0
    g220: BSplineCurve PolesCount=3 KnotsCount=2 Degree=2 IsPeriodic=0
    g221: BSplineCurve PolesCount=3 KnotsCount=2 Degree=2 IsPeriodic=0
    g222: BSplineCurve PolesCount=3 KnotsCount=2 Degree=2 IsPeriodic=0
    g223: LineSegment StartX=-25.8808 StartY=40.8407 StartZ=0 EndX=-26.5695 EndY=38.7945 EndZ=0
    g224: BSplineCurve PolesCount=3 KnotsCount=2 Degree=2 IsPeriodic=0
    g225: BSplineCurve PolesCount=3 KnotsCount=2 Degree=2 IsPeriodic=0
    g226: BSplineCurve PolesCount=3 KnotsCount=2 Degree=2 IsPeriodic=0
    g227: LineSegment StartX=-26.8145 StartY=38.8839 StartZ=0 EndX=-26.0257 EndY=41.2557 EndZ=0
    g228: BSplineCurve PolesCount=3 KnotsCount=2 Degree=2 IsPeriodic=0
    g229: BSplineCurve PolesCount=3 KnotsCount=2 Degree=2 IsPeriodic=0
    g230: LineSegment StartX=-25.7574 StartY=41.2593 StartZ=0 EndX=-24.9471 EndY=38.8589 EndZ=0
    g231: BSplineCurve PolesCount=3 KnotsCount=2 Degree=2 IsPeriodic=0
    g232: BSplineCurve PolesCount=3 KnotsCount=2 Degree=2 IsPeriodic=0
    g233: BSplineCurve PolesCount=3 KnotsCount=2 Degree=2 IsPeriodic=0
    g234: LineSegment StartX=-25.2011 StartY=38.8088 StartZ=0 EndX=-25.8808 EndY=40.8407 EndZ=0
    g235: BSplineCurve PolesCount=3 KnotsCount=2 Degree=2 IsPeriodic=0
    g236: BSplineCurve PolesCount=3 KnotsCount=2 Degree=2 IsPeriodic=0
    g237: BSplineCurve PolesCount=3 KnotsCount=2 Degree=2 IsPeriodic=0
    g238: LineSegment StartX=-27.9718 StartY=38.8624 StartZ=0 EndX=-27.4835 EndY=40.5653 EndZ=0
    g239: LineSegment StartX=-27.4835 StartY=40.5653 StartZ=0 EndX=-28.1364 EndY=40.5653 EndZ=0
    g240: LineSegment StartX=-28.1364 StartY=40.5653 StartZ=0 EndX=-28.1364 EndY=40.1753 EndZ=0
    g241: BSplineCurve PolesCount=3 KnotsCount=2 Degree=2 IsPeriodic=0
    g242: BSplineCurve PolesCount=3 KnotsCount=2 Degree=2 IsPeriodic=0
    g243: LineSegment StartX=-28.394 StartY=40.1861 StartZ=0 EndX=-28.394 EndY=40.5671 EndZ=0
    g244: BSplineCurve PolesCount=3 KnotsCount=2 Degree=2 IsPeriodic=0
    g245: BSplineCurve PolesCount=3 KnotsCount=2 Degree=2 IsPeriodic=0
    g246: BSplineCurve PolesCount=3 KnotsCount=2 Degree=2 IsPeriodic=0
    g247: LineSegment StartX=-28.6641 StartY=40.8229 StartZ=0 EndX=-28.394 EndY=40.8229 EndZ=0
    g248: LineSegment StartX=-28.394 StartY=40.8229 StartZ=0 EndX=-28.394 EndY=41.2271 EndZ=0
    g249: BSplineCurve PolesCount=3 KnotsCount=2 Degree=2 IsPeriodic=0
    g250: BSplineCurve PolesCount=3 KnotsCount=2 Degree=2 IsPeriodic=0
    g251: LineSegment StartX=-28.1364 StartY=41.2325 StartZ=0 EndX=-28.1364 EndY=40.8282 EndZ=0
    g252: LineSegment StartX=-28.1364 StartY=40.8282 StartZ=0 EndX=-27.3154 EndY=40.8282 EndZ=0
    g253: BSplineCurve PolesCount=3 KnotsCount=2 Degree=2 IsPeriodic=0
    g254: BSplineCurve PolesCount=3 KnotsCount=2 Degree=2 IsPeriodic=0
    g255: BSplineCurve PolesCount=3 KnotsCount=2 Degree=2 IsPeriodic=0
  constraints (4):
    c: Horizontal(g0)
    c: T21(g0,g1,g2)
    c: DistanceX(g0,g-4) = 3
    c: DistanceX(g-3,g0) = 3
FEATURE [PartDesign::Pocket] Pocket
  BaseFeature = -> AdditiveLoft003
  Direction = (0,1,-2e-16)
  Length = 1
  Length2 = 5
  Profile = -> Sketch
  ReferenceAxis = -> Sketch [N_Axis]
  Refine = true
  SideType = 0
  Suppressed = false
  Type = 0
  Type2 = 0
FEATURE [PartDesign::Body] Body002  label="CartographerV4"
  AllowCompound = true
  Group = -> [Sketch011,Sketch013,Pad008,Pad009,Sketch014,MirroredSketch001,Clone2D002,Pocket005,AdditiveLoft002,Chamfer,Sketch016,Pocket006,Chamfer001,Sketch017,Sketch018,AdditiveLoft003,Sketch,Pocket]
  Origin = -> Origin008
  Placement = pos=(0,0,0) rot=(0,0,1;6.13955rad)
  Tip = -> Pocket
FEATURE [App::Point] Origin011  label="Origin013"
  Role = Origin
FEATURE [Sketcher::SketchObject] Sketch020
  ArcFitTolerance = 1e-06
  AttachmentOffset = pos=(-16,-2.6,43.3) rot=(0,0,1;0rad)
  AttachmentSupport = -> [Origin010]
  ExternalTypes = [0,0]
  FullyConstrained = true
  MakeInternals = false
  MapMode = 5
  Placement = pos=(-16,-2.6,43.3) rot=(0,0,1;0rad)
  _ExternalGeoVersion = 0
  sketch-geometry (4):
    g0: ArcOfCircle CenterX=-15.8 CenterY=0 CenterZ=0 NormalX=0 NormalY=0 NormalZ=1 AngleXU=0 Radius=4 StartAngle=0.125328 EndAngle=4.71239
    g1: ArcOfCircle CenterX=15.8 CenterY=0 CenterZ=0 NormalX=0 NormalY=0 NormalZ=1 AngleXU=0 Radius=4 StartAngle=4.71239 EndAngle=9.29945
    g2: LineSegment StartX=-15.8 StartY=-4 StartZ=0 EndX=15.8 EndY=-4 EndZ=0
    g3: LineSegment StartX=-11.8314 StartY=0.5 StartZ=0 EndX=11.8314 EndY=0.5 EndZ=0
  constraints (12):
    c: DistanceX(g0,g1) = 31.6
    c: Vertical(g2,g1)
    c: Symmetric(g0,g1,g-2)
    c: Symmetric(g2,g2,g-2)
    c: Horizontal(g3)
    c: PointOnObject(g0,g-1)
    c: DistanceY(g2,g3) = 4.5
    c: DistanceY(g2,g0) = 4
    c: Coincident(g3,g1)
    c: Coincident(g1,g2)
    c: Coincident(g3,g0)
    c: Coincident(g0,g2)
FEATURE [PartDesign::Pad] Pad010
  Direction = (0,0,1)
  Length = 22
  Length2 = 10
  Profile = -> Sketch020
  ReferenceAxis = -> Sketch020 [N_Axis]
  Refine = true
  Reversed = true
  SideType = 0
  Suppressed = false
  Type = 0
  Type2 = 0
FEATURE [Sketcher::SketchObject] Sketch021
  ArcFitTolerance = 1e-06
  AttachmentSupport = -> [Origin010]
  ExternalTypes = [0]
  FullyConstrained = true
  MakeInternals = false
  MapMode = 5
  _ExternalGeoVersion = 0
  expr: Constraints[11] = 5 + 3.5 / 2
  sketch-geometry (6):
    g0: LineSegment StartX=-13.5 StartY=-5.575 StartZ=0 EndX=13.5 EndY=-5.575 EndZ=0
    g1: LineSegment StartX=13.5 StartY=-5.575 StartZ=0 EndX=13.5 EndY=5.575 EndZ=0
    g2: Circle CenterX=-9 CenterY=1.175 CenterZ=0 NormalX=0 NormalY=0 NormalZ=1 AngleXU=0 Radius=1.75
    g3: Circle CenterX=9 CenterY=1.175 CenterZ=0 NormalX=0 NormalY=0 NormalZ=1 AngleXU=0 Radius=1.75
    g4: LineSegment StartX=-13.5 StartY=-5.575 StartZ=0 EndX=-13.5 EndY=5.575 EndZ=0
    g5: LineSegment StartX=-13.5 StartY=5.575 StartZ=0 EndX=13.5 EndY=5.575 EndZ=0
  constraints (16):
    c: Equal(g3,g2)
    c: Diameter(g3) = 3.5
    c: Symmetric(g2,g3,g-2)
    c: Coincident(g4,g0)
    c: Vertical(g4)
    c: Coincident(g5,g4)
    c: Coincident(g5,g1)
    c: Horizontal(g5)
    c: DistanceY(g4,g4) = 11.15
    c: Symmetric(g4,g0,g-1)
    c: DistanceX(g5,g5) = 27
    c: DistanceY(g0,g2) = 6.75
    c: DistanceX(g2,g3) = 18
    c: Horizontal(g0)
    c: Vertical(g1)
    c: Coincident(g1,g0)
FEATURE [PartDesign::Pad] Pad011
  BaseFeature = -> Pad010
  Direction = (0,0,1)
  Length = 3
  Length2 = 10
  Profile = -> Sketch021
  ReferenceAxis = -> Sketch021 [N_Axis]
  Refine = true
  SideType = 0
  Suppressed = false
  Type = 0
  Type2 = 0
FEATURE [Sketcher::SketchObject] MirroredSketch002
  ArcFitTolerance = 1e-06
  AttachmentOffset = pos=(14,-18,0) rot=(0,0,1;0rad)
  AttachmentSupport = -> [Pad011]
  ExternalTypes = [0]
  FullyConstrained = false
  MakeInternals = false
  MapMode = 5
  Placement = pos=(-14,-2.1,-18) rot=(0,0.707107,0.707107;3.14159rad)
  _ExternalGeoVersion = 0
  sketch-geometry (160):
    g0: BSplineCurve PolesCount=4 KnotsCount=2 Degree=3 IsPeriodic=0
    g1: BSplineCurve PolesCount=4 KnotsCount=2 Degree=3 IsPeriodic=0
    g2: BSplineCurve PolesCount=4 KnotsCount=2 Degree=3 IsPeriodic=0
    g3: BSplineCurve PolesCount=4 KnotsCount=2 Degree=3 IsPeriodic=0
    g4: BSplineCurve PolesCount=4 KnotsCount=2 Degree=3 IsPeriodic=0
    g5: BSplineCurve PolesCount=4 KnotsCount=2 Degree=3 IsPeriodic=0
    g6: BSplineCurve PolesCount=4 KnotsCount=2 Degree=3 IsPeriodic=0
    g7: BSplineCurve PolesCount=4 KnotsCount=2 Degree=3 IsPeriodic=0
    g8: BSplineCurve PolesCount=4 KnotsCount=2 Degree=3 IsPeriodic=0
    g9: BSplineCurve PolesCount=4 KnotsCount=2 Degree=3 IsPeriodic=0
    g10: BSplineCurve PolesCount=4 KnotsCount=2 Degree=3 IsPeriodic=0
    g11: BSplineCurve PolesCount=4 KnotsCount=2 Degree=3 IsPeriodic=0
    g12: BSplineCurve PolesCount=4 KnotsCount=2 Degree=3 IsPeriodic=0
    g13: BSplineCurve PolesCount=4 KnotsCount=2 Degree=3 IsPeriodic=0
    g14: BSplineCurve PolesCount=4 KnotsCount=2 Degree=3 IsPeriodic=0
    g15: BSplineCurve PolesCount=4 KnotsCount=2 Degree=3 IsPeriodic=0
    g16: BSplineCurve PolesCount=4 KnotsCount=2 Degree=3 IsPeriodic=0
    g17: BSplineCurve PolesCount=4 KnotsCount=2 Degree=3 IsPeriodic=0
    g18: BSplineCurve PolesCount=4 KnotsCount=2 Degree=3 IsPeriodic=0
    g19: BSplineCurve PolesCount=4 KnotsCount=2 Degree=3 IsPeriodic=0
    g20: BSplineCurve PolesCount=4 KnotsCount=2 Degree=3 IsPeriodic=0
    g21: BSplineCurve PolesCount=4 KnotsCount=2 Degree=3 IsPeriodic=0
    g22: BSplineCurve PolesCount=4 KnotsCount=2 Degree=3 IsPeriodic=0
    g23: BSplineCurve PolesCount=4 KnotsCount=2 Degree=3 IsPeriodic=0
    g24: BSplineCurve PolesCount=4 KnotsCount=2 Degree=3 IsPeriodic=0
    g25: BSplineCurve PolesCount=4 KnotsCount=2 Degree=3 IsPeriodic=0
    g26: BSplineCurve PolesCount=4 KnotsCount=2 Degree=3 IsPeriodic=0
    g27: BSplineCurve PolesCount=4 KnotsCount=2 Degree=3 IsPeriodic=0
    g28: BSplineCurve PolesCount=4 KnotsCount=2 Degree=3 IsPeriodic=0
    g29: BSplineCurve PolesCount=4 KnotsCount=2 Degree=3 IsPeriodic=0
    g30: BSplineCurve PolesCount=4 KnotsCount=2 Degree=3 IsPeriodic=0
    g31: BSplineCurve PolesCount=4 KnotsCount=2 Degree=3 IsPeriodic=0
    g32: BSplineCurve PolesCount=4 KnotsCount=2 Degree=3 IsPeriodic=0
    g33: BSplineCurve PolesCount=4 KnotsCount=2 Degree=3 IsPeriodic=0
    g34: BSplineCurve PolesCount=4 KnotsCount=2 Degree=3 IsPeriodic=0
    g35: BSplineCurve PolesCount=4 KnotsCount=2 Degree=3 IsPeriodic=0
    g36: BSplineCurve PolesCount=4 KnotsCount=2 Degree=3 IsPeriodic=0
    g37: BSplineCurve PolesCount=4 KnotsCount=2 Degree=3 IsPeriodic=0
    g38: BSplineCurve PolesCount=4 KnotsCount=2 Degree=3 IsPeriodic=0
    g39: BSplineCurve PolesCount=4 KnotsCount=2 Degree=3 IsPeriodic=0
    g40: BSplineCurve PolesCount=4 KnotsCount=2 Degree=3 IsPeriodic=0
    g41: BSplineCurve PolesCount=4 KnotsCount=2 Degree=3 IsPeriodic=0
    g42: BSplineCurve PolesCount=4 KnotsCount=2 Degree=3 IsPeriodic=0
    g43: BSplineCurve PolesCount=4 KnotsCount=2 Degree=3 IsPeriodic=0
    g44: BSplineCurve PolesCount=4 KnotsCount=2 Degree=3 IsPeriodic=0
    g45: BSplineCurve PolesCount=4 KnotsCount=2 Degree=3 IsPeriodic=0
    g46: BSplineCurve PolesCount=4 KnotsCount=2 Degree=3 IsPeriodic=0
    g47: BSplineCurve PolesCount=4 KnotsCount=2 Degree=3 IsPeriodic=0
    g48: BSplineCurve PolesCount=4 KnotsCount=2 Degree=3 IsPeriodic=0
    g49: BSplineCurve PolesCount=4 KnotsCount=2 Degree=3 IsPeriodic=0
    g50: BSplineCurve PolesCount=4 KnotsCount=2 Degree=3 IsPeriodic=0
    g51: BSplineCurve PolesCount=4 KnotsCount=2 Degree=3 IsPeriodic=0
    g52: BSplineCurve PolesCount=4 KnotsCount=2 Degree=3 IsPeriodic=0
    g53: BSplineCurve PolesCount=4 KnotsCount=2 Degree=3 IsPeriodic=0
    g54: BSplineCurve PolesCount=4 KnotsCount=2 Degree=3 IsPeriodic=0
    g55: BSplineCurve PolesCount=4 KnotsCount=2 Degree=3 IsPeriodic=0
    g56: BSplineCurve PolesCount=4 KnotsCount=2 Degree=3 IsPeriodic=0
    g57: BSplineCurve PolesCount=4 KnotsCount=2 Degree=3 IsPeriodic=0
    g58: BSplineCurve PolesCount=4 KnotsCount=2 Degree=3 IsPeriodic=0
    g59: BSplineCurve PolesCount=4 KnotsCount=2 Degree=3 IsPeriodic=0
    g60: BSplineCurve PolesCount=4 KnotsCount=2 Degree=3 IsPeriodic=0
    g61: BSplineCurve PolesCount=4 KnotsCount=2 Degree=3 IsPeriodic=0
    g62: BSplineCurve PolesCount=4 KnotsCount=2 Degree=3 IsPeriodic=0
    g63: BSplineCurve PolesCount=4 KnotsCount=2 Degree=3 IsPeriodic=0
    g64: BSplineCurve PolesCount=4 KnotsCount=2 Degree=3 IsPeriodic=0
    g65: BSplineCurve PolesCount=4 KnotsCount=2 Degree=3 IsPeriodic=0
    g66: BSplineCurve PolesCount=4 KnotsCount=2 Degree=3 IsPeriodic=0
    g67: BSplineCurve PolesCount=4 KnotsCount=2 Degree=3 IsPeriodic=0
    g68: BSplineCurve PolesCount=4 KnotsCount=2 Degree=3 IsPeriodic=0
    g69: BSplineCurve PolesCount=4 KnotsCount=2 Degree=3 IsPeriodic=0
    g70: BSplineCurve PolesCount=4 KnotsCount=2 Degree=3 IsPeriodic=0
    g71: BSplineCurve PolesCount=4 KnotsCount=2 Degree=3 IsPeriodic=0
    g72: BSplineCurve PolesCount=4 KnotsCount=2 Degree=3 IsPeriodic=0
    g73: BSplineCurve PolesCount=4 KnotsCount=2 Degree=3 IsPeriodic=0
    g74: BSplineCurve PolesCount=4 KnotsCount=2 Degree=3 IsPeriodic=0
    g75: BSplineCurve PolesCount=4 KnotsCount=2 Degree=3 IsPeriodic=0
    g76: BSplineCurve PolesCount=4 KnotsCount=2 Degree=3 IsPeriodic=0
    g77: BSplineCurve PolesCount=4 KnotsCount=2 Degree=3 IsPeriodic=0
    g78: BSplineCurve PolesCount=4 KnotsCount=2 Degree=3 IsPeriodic=0
    g79: BSplineCurve PolesCount=4 KnotsCount=2 Degree=3 IsPeriodic=0
    g80: BSplineCurve PolesCount=4 KnotsCount=2 Degree=3 IsPeriodic=0
    g81: BSplineCurve PolesCount=4 KnotsCount=2 Degree=3 IsPeriodic=0
    g82: BSplineCurve PolesCount=4 KnotsCount=2 Degree=3 IsPeriodic=0
    g83: BSplineCurve PolesCount=4 KnotsCount=2 Degree=3 IsPeriodic=0
    g84: BSplineCurve PolesCount=4 KnotsCount=2 Degree=3 IsPeriodic=0
    g85: BSplineCurve PolesCount=4 KnotsCount=2 Degree=3 IsPeriodic=0
    g86: BSplineCurve PolesCount=4 KnotsCount=2 Degree=3 IsPeriodic=0
    g87: BSplineCurve PolesCount=4 KnotsCount=2 Degree=3 IsPeriodic=0
    g88: BSplineCurve PolesCount=4 KnotsCount=2 Degree=3 IsPeriodic=0
    g89: BSplineCurve PolesCount=4 KnotsCount=2 Degree=3 IsPeriodic=0
    g90: BSplineCurve PolesCount=4 KnotsCount=2 Degree=3 IsPeriodic=0
    g91: BSplineCurve PolesCount=4 KnotsCount=2 Degree=3 IsPeriodic=0
    g92: BSplineCurve PolesCount=4 KnotsCount=2 Degree=3 IsPeriodic=0
    g93: BSplineCurve PolesCount=4 KnotsCount=2 Degree=3 IsPeriodic=0
    g94: BSplineCurve PolesCount=4 KnotsCount=2 Degree=3 IsPeriodic=0
    g95: BSplineCurve PolesCount=4 KnotsCount=2 Degree=3 IsPeriodic=0
    g96: BSplineCurve PolesCount=4 KnotsCount=2 Degree=3 IsPeriodic=0
    g97: BSplineCurve PolesCount=4 KnotsCount=2 Degree=3 IsPeriodic=0
    g98: BSplineCurve PolesCount=4 KnotsCount=2 Degree=3 IsPeriodic=0
    g99: BSplineCurve PolesCount=4 KnotsCount=2 Degree=3 IsPeriodic=0
    g100: BSplineCurve PolesCount=4 KnotsCount=2 Degree=3 IsPeriodic=0
    g101: BSplineCurve PolesCount=4 KnotsCount=2 Degree=3 IsPeriodic=0
    g102: BSplineCurve PolesCount=4 KnotsCount=2 Degree=3 IsPeriodic=0
    g103: BSplineCurve PolesCount=4 KnotsCount=2 Degree=3 IsPeriodic=0
    g104: BSplineCurve PolesCount=4 KnotsCount=2 Degree=3 IsPeriodic=0
    g105: BSplineCurve PolesCount=2 KnotsCount=2 Degree=1 IsPeriodic=0
    g106: BSplineCurve PolesCount=4 KnotsCount=2 Degree=3 IsPeriodic=0
    g107: BSplineCurve PolesCount=4 KnotsCount=2 Degree=3 IsPeriodic=0
    g108: BSplineCurve PolesCount=4 KnotsCount=2 Degree=3 IsPeriodic=0
    g109: BSplineCurve PolesCount=4 KnotsCount=2 Degree=3 IsPeriodic=0
    g110: BSplineCurve PolesCount=4 KnotsCount=2 Degree=3 IsPeriodic=0
    g111: BSplineCurve PolesCount=4 KnotsCount=2 Degree=3 IsPeriodic=0
    g112: BSplineCurve PolesCount=4 KnotsCount=2 Degree=3 IsPeriodic=0
    g113: BSplineCurve PolesCount=4 KnotsCount=2 Degree=3 IsPeriodic=0
    g114: BSplineCurve PolesCount=4 KnotsCount=2 Degree=3 IsPeriodic=0
    g115: BSplineCurve PolesCount=4 KnotsCount=2 Degree=3 IsPeriodic=0
    g116: BSplineCurve PolesCount=4 KnotsCount=2 Degree=3 IsPeriodic=0
    g117: BSplineCurve PolesCount=4 KnotsCount=2 Degree=3 IsPeriodic=0
    g118: BSplineCurve PolesCount=4 KnotsCount=2 Degree=3 IsPeriodic=0
    g119: BSplineCurve PolesCount=4 KnotsCount=2 Degree=3 IsPeriodic=0
    g120: BSplineCurve PolesCount=4 KnotsCount=2 Degree=3 IsPeriodic=0
    g121: BSplineCurve PolesCount=4 KnotsCount=2 Degree=3 IsPeriodic=0
    g122: BSplineCurve PolesCount=4 KnotsCount=2 Degree=3 IsPeriodic=0
    g123: BSplineCurve PolesCount=4 KnotsCount=2 Degree=3 IsPeriodic=0
    g124: BSplineCurve PolesCount=4 KnotsCount=2 Degree=3 IsPeriodic=0
    g125: BSplineCurve PolesCount=4 KnotsCount=2 Degree=3 IsPeriodic=0
    g126: BSplineCurve PolesCount=4 KnotsCount=2 Degree=3 IsPeriodic=0
    g127: BSplineCurve PolesCount=4 KnotsCount=2 Degree=3 IsPeriodic=0
    g128: BSplineCurve PolesCount=4 KnotsCount=2 Degree=3 IsPeriodic=0
    g129: BSplineCurve PolesCount=4 KnotsCount=2 Degree=3 IsPeriodic=0
    g130: BSplineCurve PolesCount=4 KnotsCount=2 Degree=3 IsPeriodic=0
    g131: BSplineCurve PolesCount=4 KnotsCount=2 Degree=3 IsPeriodic=0
    g132: BSplineCurve PolesCount=4 KnotsCount=2 Degree=3 IsPeriodic=0
    g133: BSplineCurve PolesCount=4 KnotsCount=2 Degree=3 IsPeriodic=0
    g134: BSplineCurve PolesCount=4 KnotsCount=2 Degree=3 IsPeriodic=0
    g135: BSplineCurve PolesCount=4 KnotsCount=2 Degree=3 IsPeriodic=0
    g136: BSplineCurve PolesCount=4 KnotsCount=2 Degree=3 IsPeriodic=0
    g137: BSplineCurve PolesCount=4 KnotsCount=2 Degree=3 IsPeriodic=0
    g138: BSplineCurve PolesCount=4 KnotsCount=2 Degree=3 IsPeriodic=0
    g139: BSplineCurve PolesCount=4 KnotsCount=2 Degree=3 IsPeriodic=0
    g140: BSplineCurve PolesCount=4 KnotsCount=2 Degree=3 IsPeriodic=0
    g141: BSplineCurve PolesCount=4 KnotsCount=2 Degree=3 IsPeriodic=0
    g142: BSplineCurve PolesCount=4 KnotsCount=2 Degree=3 IsPeriodic=0
    g143: BSplineCurve PolesCount=4 KnotsCount=2 Degree=3 IsPeriodic=0
    g144: BSplineCurve PolesCount=4 KnotsCount=2 Degree=3 IsPeriodic=0
    g145: BSplineCurve PolesCount=4 KnotsCount=2 Degree=3 IsPeriodic=0
    g146: BSplineCurve PolesCount=4 KnotsCount=2 Degree=3 IsPeriodic=0
    g147: BSplineCurve PolesCount=4 KnotsCount=2 Degree=3 IsPeriodic=0
    g148: BSplineCurve PolesCount=4 KnotsCount=2 Degree=3 IsPeriodic=0
    g149: BSplineCurve PolesCount=4 KnotsCount=2 Degree=3 IsPeriodic=0
    g150: BSplineCurve PolesCount=4 KnotsCount=2 Degree=3 IsPeriodic=0
    g151: BSplineCurve PolesCount=4 KnotsCount=2 Degree=3 IsPeriodic=0
    g152: BSplineCurve PolesCount=4 KnotsCount=2 Degree=3 IsPeriodic=0
    g153: BSplineCurve PolesCount=4 KnotsCount=2 Degree=3 IsPeriodic=0
    g154: BSplineCurve PolesCount=4 KnotsCount=2 Degree=3 IsPeriodic=0
    g155: BSplineCurve PolesCount=4 KnotsCount=2 Degree=3 IsPeriodic=0
    g156: BSplineCurve PolesCount=4 KnotsCount=2 Degree=3 IsPeriodic=0
    g157: BSplineCurve PolesCount=4 KnotsCount=2 Degree=3 IsPeriodic=0
    g158: BSplineCurve PolesCount=4 KnotsCount=2 Degree=3 IsPeriodic=0
    g159: BSplineCurve PolesCount=4 KnotsCount=2 Degree=3 IsPeriodic=0
  constraints (160):
    c: Coincident(g10,g11)
    c: Coincident(g4,g5)
    c: Coincident(g11,g12)
    c: Coincident(g0,g12)
    c: Coincident(g5,g6)
    c: Coincident(g9,g10)
    c: Coincident(g0,g1)
    c: Coincident(g8,g9)
    c: Coincident(g1,g2)
    c: Coincident(g3,g4)
    c: Coincident(g2,g3)
    c: Coincident(g7,g8)
    c: Coincident(g6,g7)
    c: Coincident(g79,g80)
    c: Coincident(g96,g97)
    c: Coincident(g109,g110)
    c: Coincident(g13,g26)
    c: Coincident(g110,g111)
    c: Coincident(g13,g14)
    c: Coincident(g136,g137)
    c: Coincident(g102,g103)
    c: Coincident(g82,g83)
    c: Coincident(g137,g138)
    c: Coincident(g103,g104)
    c: Coincident(g78,g79)
    c: Coincident(g83,g84)
    c: Coincident(g80,g81)
    c: Coincident(g25,g26)
    c: Coincident(g95,g96)
    c: Coincident(g108,g109)
    c: Coincident(g73,g81)
    c: Coincident(g14,g15)
    c: Coincident(g111,g112)
    c: Coincident(g127,g131)
    c: Coincident(g127,g128)
    c: Coincident(g87,g88)
    c: Coincident(g91,g92)
    c: Coincident(g112,g113)
    c: Coincident(g15,g16)
    c: Coincident(g130,g131)
    c: Coincident(g97,g98)
    c: Coincident(g88,g89)
    c: Coincident(g84,g85)
    c: Coincident(g92,g93)
    c: Coincident(g113,g114)
    c: Coincident(g16,g17)
    c: Coincident(g17,g18)
    c: Coincident(g114,g115)
    c: Coincident(g82,g100)
    c: Coincident(g129,g130)
    c: Coincident(g128,g129)
    c: Coincident(g73,g74)
    c: Coincident(g107,g108)
    c: Coincident(g135,g136)
    c: Coincident(g18,g19)
    c: Coincident(g19,g20)
    c: Coincident(g106,g107)
    c: Coincident(g24,g25)
    c: Coincident(g99,g100)
    c: Coincident(g106,g120)
    c: Coincident(g74,g75)
    c: Coincident(g75,g76)
    c: Coincident(g138,g139)
    c: Coincident(g119,g120)
    c: Coincident(g139,g140)
    c: Coincident(g132,g140)
    c: Coincident(g20,g21)
    c: Coincident(g98,g99)
    c: Coincident(g118,g119)
    c: Coincident(g132,g133)
    c: Coincident(g21,g22)
    c: Coincident(g115,g116)
    c: Coincident(g90,g91)
    c: Coincident(g89,g90)
    c: Coincident(g77,g78)
    c: Coincident(g134,g135)
    c: Coincident(g85,g86)
    c: Coincident(g86,g87)
    c: Coincident(g23,g24)
    c: Coincident(g104,g105)
    c: Coincident(g101,g102)
    c: Coincident(g94,g95)
    c: Coincident(g117,g118)
    c: Coincident(g101,g105)
    c: Coincident(g22,g23)
    c: Coincident(g93,g94)
    c: Coincident(g76,g77)
    c: Coincident(g133,g134)
    c: Coincident(g116,g117)
    c: Coincident(g148,g149)
    c: Coincident(g157,g158)
    c: Coincident(g158,g159)
    c: Coincident(g147,g148)
    c: Coincident(g146,g147)
    c: Coincident(g156,g157)
    c: Coincident(g149,g150)
    c: Coincident(g57,g58)
    c: Coincident(g155,g156)
    c: Coincident(g46,g47)
    c: Coincident(g56,g57)
    c: Coincident(g47,g48)
    c: Coincident(g48,g49)
    c: Coincident(g45,g46)
    c: Coincident(g150,g151)
    c: Coincident(g55,g56)
    c: Coincident(g49,g50)
    c: Coincident(g122,g123)
    c: Coincident(g43,g44)
    c: Coincident(g44,g45)
    c: Coincident(g54,g55)
    c: Coincident(g123,g124)
    c: Coincident(g42,g43)
    c: Coincident(g50,g51)
    c: Coincident(g124,g125)
    c: Coincident(g53,g54)
    c: Coincident(g40,g41)
    c: Coincident(g52,g53)
    c: Coincident(g51,g52)
    c: Coincident(g58,g59)
    c: Coincident(g121,g122)
    c: Coincident(g39,g40)
    c: Coincident(g41,g42)
    c: Coincident(g38,g39)
    c: Coincident(g125,g126)
    c: Coincident(g121,g126)
    c: Coincident(g32,g33)
    c: Coincident(g31,g32)
    c: Coincident(g153,g159)
    c: Coincident(g37,g38)
    c: Coincident(g59,g60)
    c: Coincident(g67,g68)
    c: Coincident(g154,g155)
    c: Coincident(g66,g67)
    c: Coincident(g36,g37)
    c: Coincident(g60,g61)
    c: Coincident(g153,g154)
    c: Coincident(g65,g66)
    c: Coincident(g68,g69)
    c: Coincident(g71,g72)
    c: Coincident(g141,g144)
    c: Coincident(g33,g34)
    c: Coincident(g64,g65)
    c: Coincident(g145,g146)
    c: Coincident(g141,g142)
    c: Coincident(g63,g64)
    c: Coincident(g145,g152)
    c: Coincident(g143,g144)
    c: Coincident(g61,g62)
    c: Coincident(g34,g35)
    c: Coincident(g29,g30)
    c: Coincident(g35,g36)
    c: Coincident(g62,g63)
    c: Coincident(g27,g30)
    c: Coincident(g69,g70)
    c: Coincident(g70,g71)
    c: Coincident(g142,g143)
    c: Coincident(g28,g29)
    c: Coincident(g151,g152)
    c: Coincident(g27,g28)
    c: Coincident(g31,g72)
FEATURE [Part::Part2DObjectPython] Clone2D003  label="MirroredSketch001 (2D)002"  # Draft 2D object (typed FeaturePython)
  AttachmentOffset = pos=(4.3,23,0) rot=(0,0,-1;1.5708rad)
  AttachmentSupport = -> [Pad011]
  ForceCompound = false
  Fuse = false
  MapMode = 5
  Objects = -> [MirroredSketch002]
  Placement = pos=(-4.3,-2.1,23) rot=(-0.57735,0.57735,0.57735;2.0944rad)
  Scale = (0.65,0.65,0.65)
FEATURE [PartDesign::Pocket] Pocket008
  BaseFeature = -> Pad011
  Direction = (0,-1,2e-16)
  Length = 2
  Length2 = 5
  Profile = -> Clone2D003
  ReferenceAxis = -> Clone2D003 [N_Axis]
  Refine = true
  SideType = 0
  Suppressed = false
  Type = 0
  Type2 = 0
FEATURE [Sketcher::SketchObject] Sketch022
  ArcFitTolerance = 1e-06
  AttachmentSupport = -> [Pad011]
  ExternalGeometry = -> [Pad011]
  ExternalTypes = [0,0]
  FullyConstrained = true
  MakeInternals = false
  MapMode = 5
  Placement = pos=(0,0,3) rot=(0,0,1;0rad)
  _ExternalGeoVersion = 0
  sketch-geometry (4):
    g0: LineSegment StartX=-13.5 StartY=-5.575 StartZ=0 EndX=13.5 EndY=-5.575 EndZ=0
    g1: LineSegment StartX=13.5 StartY=-5.575 StartZ=0 EndX=13.5 EndY=-2.575 EndZ=0
    g2: LineSegment StartX=13.5 StartY=-2.575 StartZ=0 EndX=-13.5 EndY=-2.575 EndZ=0
    g3: LineSegment StartX=-13.5 StartY=-2.575 StartZ=0 EndX=-13.5 EndY=-5.575 EndZ=0
  constraints (11):
    c: Coincident(g0,g1)
    c: Coincident(g1,g2)
    c: Coincident(g2,g3)
    c: Coincident(g3,g0)
    c: Horizontal(g2)
    c: Vertical(g1)
    c: Vertical(g3)
    c: DistanceY(g1,g1) = 3
    c: Horizontal(g0)
    c: Coincident(g0,g-3)
    c: PointOnObject(g2,g-4)
FEATURE [PartDesign::AdditiveLoft] AdditiveLoft004
  BaseFeature = -> Pocket008
  Closed = false
  Profile = -> Sketch022
  Refine = true
  Ruled = false
  Sections = -> [Pocket008]
  Suppressed = false
FEATURE [PartDesign::Chamfer] Chamfer002
  Angle = 45
  Base = -> AdditiveLoft004 [Edge468,Edge489]
  BaseFeature = -> AdditiveLoft004
  ChamferType = 0
  FlipDirection = false
  Refine = true
  Size = 2
  Size2 = 1
  SupportTransform = false
  Suppressed = false
  UseAllEdges = false
FEATURE [Sketcher::SketchObject] Sketch023
  ArcFitTolerance = 1e-06
  AttachmentSupport = -> [Chamfer002]
  ExternalGeometry = -> [Chamfer002]
  ExternalTypes = [0,0]
  FullyConstrained = true
  MakeInternals = false
  MapMode = 5
  Placement = pos=(0,0,43.3) rot=(0,0,1;0rad)
  _ExternalGeoVersion = 0
  sketch-geometry (2):
    g0: Circle CenterX=-31.8 CenterY=-2.6 CenterZ=0 NormalX=0 NormalY=0 NormalZ=1 AngleXU=0 Radius=1.5
    g1: Circle CenterX=-0.2 CenterY=-2.6 CenterZ=0 NormalX=0 NormalY=0 NormalZ=1 AngleXU=0 Radius=1.5
  constraints (4):
    c: Coincident(g0,g-4)
    c: Coincident(g1,g-3)
    c: Equal(g1,g0)
    c: Diameter(g0) = 3
FEATURE [PartDesign::Pocket] Pocket009
  BaseFeature = -> Chamfer002
  Direction = (0,0,-1)
  Length = 11
  Length2 = 5
  Profile = -> Sketch023
  ReferenceAxis = -> Sketch023 [N_Axis]
  Refine = true
  SideType = 0
  Suppressed = false
  Type = 0
  Type2 = 0
FEATURE [PartDesign::Chamfer] Chamfer003
  Angle = 45
  Base = -> Pocket009 [Edge194,Edge193]
  BaseFeature = -> Pocket009
  ChamferType = 0
  FlipDirection = false
  Refine = true
  Size = 1
  Size2 = 1
  SupportTransform = false
  Suppressed = false
  UseAllEdges = false
FEATURE [Sketcher::SketchObject] Sketch024
  ArcFitTolerance = 1e-06
  AttachmentSupport = -> [Chamfer003]
  ExternalGeometry = -> [Chamfer003]
  ExternalTypes = [0,0]
  FullyConstrained = true
  MakeInternals = false
  MapMode = 5
  Placement = pos=(0,0,3) rot=(0,0,1;0rad)
  _ExternalGeoVersion = 0
  sketch-geometry (4):
    g0: LineSegment StartX=-5 StartY=-2.575 StartZ=0 EndX=5 EndY=-2.575 EndZ=0
    g1: LineSegment StartX=5 StartY=-2.575 StartZ=0 EndX=5 EndY=5.575 EndZ=0
    g2: LineSegment StartX=5 StartY=5.575 StartZ=0 EndX=-5 EndY=5.575 EndZ=0
    g3: LineSegment StartX=-5 StartY=5.575 StartZ=0 EndX=-5 EndY=-2.575 EndZ=0
  constraints (11):
    c: Coincident(g0,g1)
    c: Coincident(g1,g2)
    c: Coincident(g2,g3)
    c: Coincident(g3,g0)
    c: Horizontal(g0)
    c: Vertical(g1)
    c: Vertical(g3)
    c: PointOnObject(g0,g-3)
    c: PointOnObject(g1,g-4)
    c: DistanceX(g2,g2) = 10
    c: Symmetric(g1,g2,g-2)
FEATURE [Sketcher::SketchObject] Sketch025
  ArcFitTolerance = 1e-06
  AttachmentSupport = -> [Chamfer003]
  ExternalGeometry = -> [Chamfer003]
  ExternalTypes = [0]
  FullyConstrained = true
  MakeInternals = false
  MapMode = 5
  Placement = pos=(1e-16,-2.65108,0.0688123) rot=(0,0.716222,0.697873;3.14159rad)
  _ExternalGeoVersion = 0
  sketch-geometry (4):
    g0: LineSegment StartX=-5.5 StartY=11.0322 StartZ=0 EndX=-5.5 EndY=10.9322 EndZ=0
    g1: LineSegment StartX=-5.5 StartY=10.9322 StartZ=0 EndX=4.5 EndY=10.9322 EndZ=0
    g2: LineSegment StartX=4.5 StartY=10.9322 StartZ=0 EndX=4.5 EndY=11.0322 EndZ=0
    g3: LineSegment StartX=4.5 StartY=11.0322 StartZ=0 EndX=-5.5 EndY=11.0322 EndZ=0
  constraints (12):
    c: Coincident(g0,g1)
    c: Coincident(g1,g2)
    c: Coincident(g2,g3)
    c: Coincident(g3,g0)
    c: Vertical(g0)
    c: Vertical(g2)
    c: Horizontal(g1)
    c: Horizontal(g3)
    c: DistanceX(g3,g3) = 10
    c: DistanceY(g2,g2) = 0.1
    c: DistanceY(g-3,g0) = 8
    c: DistanceX(g-3,g0) = 8
FEATURE [PartDesign::AdditiveLoft] AdditiveLoft005
  BaseFeature = -> Chamfer003
  Closed = false
  Profile = -> Sketch024
  Refine = true
  Ruled = false
  Sections = -> [Sketch025]
  Suppressed = false
FEATURE [Sketcher::SketchObject] Sketch019
  ArcFitTolerance = 1e-06
  AttachmentSupport = -> [AdditiveLoft005]
  ExternalTypes = [0,0]
  FullyConstrained = false
  MakeInternals = false
  MapMode = 5
  Placement = pos=(0,-6.6,0) rot=(1,0,0;1.5708rad)
  _ExternalGeoVersion = 0
  sketch-geometry (560):
    g0: LineSegment [constr] StartX=-3.2 StartY=42.193 StartZ=0 EndX=-28.8 EndY=42.193 EndZ=0
    g1: BSplineCurve PolesCount=3 KnotsCount=2 Degree=2 IsPeriodic=0
    g2: BSplineCurve PolesCount=3 KnotsCount=2 Degree=2 IsPeriodic=0
    g3: BSplineCurve PolesCount=3 KnotsCount=2 Degree=2 IsPeriodic=0
    g4: BSplineCurve PolesCount=3 KnotsCount=2 Degree=2 IsPeriodic=0
    g5: BSplineCurve PolesCount=3 KnotsCount=2 Degree=2 IsPeriodic=0
    g6: BSplineCurve PolesCount=3 KnotsCount=2 Degree=2 IsPeriodic=0
    g7: LineSegment StartX=-3.2 StartY=40.9277 StartZ=0 EndX=-3.2 EndY=40.0467 EndZ=0
    g8: BSplineCurve PolesCount=3 KnotsCount=2 Degree=2 IsPeriodic=0
    g9: BSplineCurve PolesCount=3 KnotsCount=2 Degree=2 IsPeriodic=0
    g10: BSplineCurve PolesCount=3 KnotsCount=2 Degree=2 IsPeriodic=0
    g11: BSplineCurve PolesCount=3 KnotsCount=2 Degree=2 IsPeriodic=0
    g12: BSplineCurve PolesCount=3 KnotsCount=2 Degree=2 IsPeriodic=0
    g13: BSplineCurve PolesCount=3 KnotsCount=2 Degree=2 IsPeriodic=0
    g14: BSplineCurve PolesCount=3 KnotsCount=2 Degree=2 IsPeriodic=0
    g15: BSplineCurve PolesCount=3 KnotsCount=2 Degree=2 IsPeriodic=0
    g16: BSplineCurve PolesCount=3 KnotsCount=2 Degree=2 IsPeriodic=0
    g17: BSplineCurve PolesCount=3 KnotsCount=2 Degree=2 IsPeriodic=0
    g18: BSplineCurve PolesCount=3 KnotsCount=2 Degree=2 IsPeriodic=0
    g19: BSplineCurve PolesCount=3 KnotsCount=2 Degree=2 IsPeriodic=0
    g20: LineSegment StartX=-4.49416 StartY=39.96 StartZ=0 EndX=-4.49416 EndY=39.9716 EndZ=0
    g21: LineSegment StartX=-4.49416 StartY=39.9716 StartZ=0 EndX=-4.1504 EndY=39.9716 EndZ=0
    g22: LineSegment StartX=-4.1504 StartY=39.9716 StartZ=0 EndX=-4.1504 EndY=39.9658 EndZ=0
    g23: BSplineCurve PolesCount=3 KnotsCount=2 Degree=2 IsPeriodic=0
    g24: BSplineCurve PolesCount=3 KnotsCount=2 Degree=2 IsPeriodic=0
    g25: BSplineCurve PolesCount=3 KnotsCount=2 Degree=2 IsPeriodic=0
    g26: BSplineCurve PolesCount=3 KnotsCount=2 Degree=2 IsPeriodic=0
    g27: BSplineCurve PolesCount=3 KnotsCount=2 Degree=2 IsPeriodic=0
    g28: BSplineCurve PolesCount=3 KnotsCount=2 Degree=2 IsPeriodic=0
    g29: BSplineCurve PolesCount=3 KnotsCount=2 Degree=2 IsPeriodic=0
    g30: BSplineCurve PolesCount=3 KnotsCount=2 Degree=2 IsPeriodic=0
    g31: LineSegment StartX=-3.54376 StartY=40.0467 StartZ=0 EndX=-3.54376 EndY=40.9277 EndZ=0
    g32: BSplineCurve PolesCount=3 KnotsCount=2 Degree=2 IsPeriodic=0
    g33: BSplineCurve PolesCount=3 KnotsCount=2 Degree=2 IsPeriodic=0
    g34: BSplineCurve PolesCount=3 KnotsCount=2 Degree=2 IsPeriodic=0
    g35: BSplineCurve PolesCount=3 KnotsCount=2 Degree=2 IsPeriodic=0
    g36: BSplineCurve PolesCount=3 KnotsCount=2 Degree=2 IsPeriodic=0
    g37: BSplineCurve PolesCount=3 KnotsCount=2 Degree=2 IsPeriodic=0
    g38: BSplineCurve PolesCount=3 KnotsCount=2 Degree=2 IsPeriodic=0
    g39: BSplineCurve PolesCount=3 KnotsCount=2 Degree=2 IsPeriodic=0
    g40: LineSegment StartX=-4.1504 StartY=41.0086 StartZ=0 EndX=-4.1504 EndY=41.0028 EndZ=0
    g41: LineSegment StartX=-4.1504 StartY=41.0028 StartZ=0 EndX=-4.49416 EndY=41.0028 EndZ=0
    g42: LineSegment StartX=-4.49416 StartY=41.0028 StartZ=0 EndX=-4.49416 EndY=41.0144 EndZ=0
    g43: BSplineCurve PolesCount=3 KnotsCount=2 Degree=2 IsPeriodic=0
    g44: BSplineCurve PolesCount=3 KnotsCount=2 Degree=2 IsPeriodic=0
    g45: BSplineCurve PolesCount=3 KnotsCount=2 Degree=2 IsPeriodic=0
    g46: BSplineCurve PolesCount=3 KnotsCount=2 Degree=2 IsPeriodic=0
    g47: BSplineCurve PolesCount=3 KnotsCount=2 Degree=2 IsPeriodic=0
    g48: BSplineCurve PolesCount=3 KnotsCount=2 Degree=2 IsPeriodic=0
    g49: BSplineCurve PolesCount=3 KnotsCount=2 Degree=2 IsPeriodic=0
    g50: BSplineCurve PolesCount=3 KnotsCount=2 Degree=2 IsPeriodic=0
    g51: BSplineCurve PolesCount=3 KnotsCount=2 Degree=2 IsPeriodic=0
    g52: BSplineCurve PolesCount=3 KnotsCount=2 Degree=2 IsPeriodic=0
    g53: BSplineCurve PolesCount=3 KnotsCount=2 Degree=2 IsPeriodic=0
    g54: BSplineCurve PolesCount=3 KnotsCount=2 Degree=2 IsPeriodic=0
    g55: BSplineCurve PolesCount=3 KnotsCount=2 Degree=2 IsPeriodic=0
    g56: BSplineCurve PolesCount=3 KnotsCount=2 Degree=2 IsPeriodic=0
    g57: BSplineCurve PolesCount=3 KnotsCount=2 Degree=2 IsPeriodic=0
    g58: BSplineCurve PolesCount=3 KnotsCount=2 Degree=2 IsPeriodic=0
    g59: BSplineCurve PolesCount=3 KnotsCount=2 Degree=2 IsPeriodic=0
    g60: BSplineCurve PolesCount=3 KnotsCount=2 Degree=2 IsPeriodic=0
    g61: LineSegment StartX=-5.65254 StartY=40.6302 StartZ=0 EndX=-5.88364 EndY=40.6302 EndZ=0
    g62: LineSegment StartX=-5.88364 StartY=40.6302 StartZ=0 EndX=-5.88364 EndY=40.5551 EndZ=0
    g63: BSplineCurve PolesCount=3 KnotsCount=2 Degree=2 IsPeriodic=0
    g64: BSplineCurve PolesCount=3 KnotsCount=2 Degree=2 IsPeriodic=0
    g65: BSplineCurve PolesCount=3 KnotsCount=2 Degree=2 IsPeriodic=0
    g66: BSplineCurve PolesCount=3 KnotsCount=2 Degree=2 IsPeriodic=0
    g67: BSplineCurve PolesCount=3 KnotsCount=2 Degree=2 IsPeriodic=0
    g68: BSplineCurve PolesCount=3 KnotsCount=2 Degree=2 IsPeriodic=0
    g69: BSplineCurve PolesCount=3 KnotsCount=2 Degree=2 IsPeriodic=0
    g70: BSplineCurve PolesCount=3 KnotsCount=2 Degree=2 IsPeriodic=0
    g71: LineSegment StartX=-5.28856 StartY=40.4887 StartZ=0 EndX=-5.28856 EndY=40.4915 EndZ=0
    g72: LineSegment StartX=-5.28856 StartY=40.4915 StartZ=0 EndX=-4.95058 EndY=40.4915 EndZ=0
    g73: LineSegment StartX=-4.95058 StartY=40.4915 StartZ=0 EndX=-4.95058 EndY=40.4829 EndZ=0
    g74: BSplineCurve PolesCount=3 KnotsCount=2 Degree=2 IsPeriodic=0
    g75: BSplineCurve PolesCount=3 KnotsCount=2 Degree=2 IsPeriodic=0
    g76: BSplineCurve PolesCount=3 KnotsCount=2 Degree=2 IsPeriodic=0
    g77: BSplineCurve PolesCount=3 KnotsCount=2 Degree=2 IsPeriodic=0
    g78: BSplineCurve PolesCount=3 KnotsCount=2 Degree=2 IsPeriodic=0
    g79: BSplineCurve PolesCount=3 KnotsCount=2 Degree=2 IsPeriodic=0
    g80: BSplineCurve PolesCount=3 KnotsCount=2 Degree=2 IsPeriodic=0
    g81: BSplineCurve PolesCount=3 KnotsCount=2 Degree=2 IsPeriodic=0
    g82: BSplineCurve PolesCount=3 KnotsCount=2 Degree=2 IsPeriodic=0
    g83: BSplineCurve PolesCount=3 KnotsCount=2 Degree=2 IsPeriodic=0
    g84: BSplineCurve PolesCount=3 KnotsCount=2 Degree=2 IsPeriodic=0
    g85: BSplineCurve PolesCount=3 KnotsCount=2 Degree=2 IsPeriodic=0
    g86: LineSegment StartX=-6.22162 StartY=40.5551 StartZ=0 EndX=-6.22162 EndY=41.5488 EndZ=0
    g87: LineSegment StartX=-6.22162 StartY=41.5488 StartZ=0 EndX=-5.88364 EndY=41.5488 EndZ=0
    g88: LineSegment StartX=-5.88364 StartY=41.5488 StartZ=0 EndX=-5.88364 EndY=41.2975 EndZ=0
    g89: BSplineCurve PolesCount=3 KnotsCount=2 Degree=2 IsPeriodic=0
    g90: BSplineCurve PolesCount=3 KnotsCount=2 Degree=2 IsPeriodic=0
    g91: BSplineCurve PolesCount=3 KnotsCount=2 Degree=2 IsPeriodic=0
    g92: BSplineCurve PolesCount=3 KnotsCount=2 Degree=2 IsPeriodic=0
    g93: BSplineCurve PolesCount=3 KnotsCount=2 Degree=2 IsPeriodic=0
    g94: BSplineCurve PolesCount=3 KnotsCount=2 Degree=2 IsPeriodic=0
    g95: BSplineCurve PolesCount=3 KnotsCount=2 Degree=2 IsPeriodic=0
    g96: BSplineCurve PolesCount=3 KnotsCount=2 Degree=2 IsPeriodic=0
    g97: LineSegment StartX=-5.88364 StartY=41.0028 StartZ=0 EndX=-5.88364 EndY=40.9162 EndZ=0
    g98: LineSegment StartX=-5.88364 StartY=40.9162 StartZ=0 EndX=-5.65254 EndY=40.9162 EndZ=0
    g99: BSplineCurve PolesCount=3 KnotsCount=2 Degree=2 IsPeriodic=0
    g100: BSplineCurve PolesCount=3 KnotsCount=2 Degree=2 IsPeriodic=0
    g101: BSplineCurve PolesCount=3 KnotsCount=2 Degree=2 IsPeriodic=0
    g102: BSplineCurve PolesCount=3 KnotsCount=2 Degree=2 IsPeriodic=0
    g103: BSplineCurve PolesCount=3 KnotsCount=2 Degree=2 IsPeriodic=0
    g104: BSplineCurve PolesCount=3 KnotsCount=2 Degree=2 IsPeriodic=0
    g105: BSplineCurve PolesCount=3 KnotsCount=2 Degree=2 IsPeriodic=0
    g106: BSplineCurve PolesCount=3 KnotsCount=2 Degree=2 IsPeriodic=0
    g107: BSplineCurve PolesCount=3 KnotsCount=2 Degree=2 IsPeriodic=0
    g108: BSplineCurve PolesCount=3 KnotsCount=2 Degree=2 IsPeriodic=0
    g109: LineSegment StartX=-6.87736 StartY=41.5488 StartZ=0 EndX=-6.87736 EndY=40.0467 EndZ=0
    g110: LineSegment StartX=-6.87736 StartY=40.0467 StartZ=0 EndX=-7.22112 EndY=40.0467 EndZ=0
    g111: LineSegment StartX=-7.22112 StartY=40.0467 StartZ=0 EndX=-7.22112 EndY=40.4424 EndZ=0
    g112: BSplineCurve PolesCount=3 KnotsCount=2 Degree=2 IsPeriodic=0
    g113: BSplineCurve PolesCount=3 KnotsCount=2 Degree=2 IsPeriodic=0
    g114: BSplineCurve PolesCount=3 KnotsCount=2 Degree=2 IsPeriodic=0
    g115: BSplineCurve PolesCount=3 KnotsCount=2 Degree=2 IsPeriodic=0
    g116: BSplineCurve PolesCount=3 KnotsCount=2 Degree=2 IsPeriodic=0
    g117: BSplineCurve PolesCount=3 KnotsCount=2 Degree=2 IsPeriodic=0
    g118: LineSegment StartX=-7.96353 StartY=40.0236 StartZ=0 EndX=-7.96353 EndY=40.3384 EndZ=0
    g119: BSplineCurve PolesCount=3 KnotsCount=2 Degree=2 IsPeriodic=0
    g120: BSplineCurve PolesCount=3 KnotsCount=2 Degree=2 IsPeriodic=0
    g121: BSplineCurve PolesCount=3 KnotsCount=2 Degree=2 IsPeriodic=0
    g122: BSplineCurve PolesCount=3 KnotsCount=2 Degree=2 IsPeriodic=0
    g123: BSplineCurve PolesCount=3 KnotsCount=2 Degree=2 IsPeriodic=0
    g124: BSplineCurve PolesCount=3 KnotsCount=2 Degree=2 IsPeriodic=0
    g125: BSplineCurve PolesCount=3 KnotsCount=2 Degree=2 IsPeriodic=0
    g126: BSplineCurve PolesCount=3 KnotsCount=2 Degree=2 IsPeriodic=0
    g127: BSplineCurve PolesCount=3 KnotsCount=2 Degree=2 IsPeriodic=0
    g128: BSplineCurve PolesCount=3 KnotsCount=2 Degree=2 IsPeriodic=0
    g129: LineSegment StartX=-7.22112 StartY=40.7515 StartZ=0 EndX=-7.22112 EndY=41.5488 EndZ=0
    g130: LineSegment StartX=-7.22112 StartY=41.5488 StartZ=0 EndX=-6.87736 EndY=41.5488 EndZ=0
    g131: LineSegment StartX=-9.68811 StartY=41.5488 StartZ=0 EndX=-9.33857 EndY=41.5488 EndZ=0
    g132: BSplineCurve PolesCount=3 KnotsCount=2 Degree=2 IsPeriodic=0
    g133: BSplineCurve PolesCount=3 KnotsCount=2 Degree=2 IsPeriodic=0
    g134: BSplineCurve PolesCount=3 KnotsCount=2 Degree=2 IsPeriodic=0
    g135: BSplineCurve PolesCount=3 KnotsCount=2 Degree=2 IsPeriodic=0
    g136: BSplineCurve PolesCount=3 KnotsCount=2 Degree=2 IsPeriodic=0
    g137: BSplineCurve PolesCount=3 KnotsCount=2 Degree=2 IsPeriodic=0
    g138: LineSegment StartX=-8.82437 StartY=41.0346 StartZ=0 EndX=-8.82437 EndY=40.3384 EndZ=0
    g139: LineSegment StartX=-8.82437 StartY=40.3384 StartZ=0 EndX=-8.42284 EndY=40.3384 EndZ=0
    g140: LineSegment StartX=-8.42284 StartY=40.3384 StartZ=0 EndX=-8.42284 EndY=40.0467 EndZ=0
    g141: LineSegment StartX=-8.42284 StartY=40.0467 StartZ=0 EndX=-8.82437 EndY=40.0467 EndZ=0
    g142: LineSegment StartX=-8.82437 StartY=40.0467 StartZ=0 EndX=-8.82437 EndY=39.4256 EndZ=0
    g143: LineSegment StartX=-8.82437 StartY=39.4256 StartZ=0 EndX=-9.16813 EndY=39.4256 EndZ=0
    g144: LineSegment StartX=-9.16813 StartY=39.4256 StartZ=0 EndX=-9.16813 EndY=40.0467 EndZ=0
    g145: LineSegment StartX=-9.16813 StartY=40.0467 StartZ=0 EndX=-9.68811 EndY=40.0467 EndZ=0
    g146: LineSegment StartX=-9.68811 StartY=40.0467 StartZ=0 EndX=-9.68811 EndY=40.3384 EndZ=0
    g147: LineSegment StartX=-9.68811 StartY=40.3384 StartZ=0 EndX=-9.16813 EndY=40.3384 EndZ=0
    g148: LineSegment StartX=-9.16813 StartY=40.3384 StartZ=0 EndX=-9.16813 EndY=41.0346 EndZ=0
    g149: BSplineCurve PolesCount=3 KnotsCount=2 Degree=2 IsPeriodic=0
    g150: BSplineCurve PolesCount=3 KnotsCount=2 Degree=2 IsPeriodic=0
    g151: BSplineCurve PolesCount=3 KnotsCount=2 Degree=2 IsPeriodic=0
    g152: BSplineCurve PolesCount=3 KnotsCount=2 Degree=2 IsPeriodic=0
    g153: LineSegment StartX=-9.33857 StartY=41.2571 StartZ=0 EndX=-9.68811 EndY=41.2571 EndZ=0
    g154: LineSegment StartX=-9.68811 StartY=41.2571 StartZ=0 EndX=-9.68811 EndY=41.5488 EndZ=0
    g155: BSplineCurve PolesCount=3 KnotsCount=2 Degree=2 IsPeriodic=0
    g156: BSplineCurve PolesCount=3 KnotsCount=2 Degree=2 IsPeriodic=0
    g157: BSplineCurve PolesCount=3 KnotsCount=2 Degree=2 IsPeriodic=0
    g158: BSplineCurve PolesCount=3 KnotsCount=2 Degree=2 IsPeriodic=0
    g159: BSplineCurve PolesCount=3 KnotsCount=2 Degree=2 IsPeriodic=0
    g160: BSplineCurve PolesCount=3 KnotsCount=2 Degree=2 IsPeriodic=0
    g161: LineSegment StartX=-10.133 StartY=40.9422 StartZ=0 EndX=-10.133 EndY=40.6533 EndZ=0
    g162: BSplineCurve PolesCount=3 KnotsCount=2 Degree=2 IsPeriodic=0
    g163: BSplineCurve PolesCount=3 KnotsCount=2 Degree=2 IsPeriodic=0
    g164: BSplineCurve PolesCount=3 KnotsCount=2 Degree=2 IsPeriodic=0
    g165: BSplineCurve PolesCount=3 KnotsCount=2 Degree=2 IsPeriodic=0
    g166: BSplineCurve PolesCount=3 KnotsCount=2 Degree=2 IsPeriodic=0
    g167: BSplineCurve PolesCount=3 KnotsCount=2 Degree=2 IsPeriodic=0
    g168: BSplineCurve PolesCount=3 KnotsCount=2 Degree=2 IsPeriodic=0
    g169: BSplineCurve PolesCount=3 KnotsCount=2 Degree=2 IsPeriodic=0
    g170: BSplineCurve PolesCount=3 KnotsCount=2 Degree=2 IsPeriodic=0
    g171: BSplineCurve PolesCount=3 KnotsCount=2 Degree=2 IsPeriodic=0
    g172: BSplineCurve PolesCount=3 KnotsCount=2 Degree=2 IsPeriodic=0
    g173: BSplineCurve PolesCount=3 KnotsCount=2 Degree=2 IsPeriodic=0
    g174: LineSegment StartX=-11.4445 StartY=40.6533 StartZ=0 EndX=-11.4445 EndY=40.9422 EndZ=0
    g175: BSplineCurve PolesCount=3 KnotsCount=2 Degree=2 IsPeriodic=0
    g176: BSplineCurve PolesCount=3 KnotsCount=2 Degree=2 IsPeriodic=0
    g177: BSplineCurve PolesCount=3 KnotsCount=2 Degree=2 IsPeriodic=0
    g178: BSplineCurve PolesCount=3 KnotsCount=2 Degree=2 IsPeriodic=0
    g179: BSplineCurve PolesCount=3 KnotsCount=2 Degree=2 IsPeriodic=0
    g180: BSplineCurve PolesCount=3 KnotsCount=2 Degree=2 IsPeriodic=0
    g181: BSplineCurve PolesCount=3 KnotsCount=2 Degree=2 IsPeriodic=0
    g182: BSplineCurve PolesCount=3 KnotsCount=2 Degree=2 IsPeriodic=0
    g183: BSplineCurve PolesCount=3 KnotsCount=2 Degree=2 IsPeriodic=0
    g184: BSplineCurve PolesCount=3 KnotsCount=2 Degree=2 IsPeriodic=0
    g185: LineSegment StartX=-11.1007 StartY=40.9422 StartZ=0 EndX=-11.1007 EndY=40.6533 EndZ=0
    g186: BSplineCurve PolesCount=3 KnotsCount=2 Degree=2 IsPeriodic=0
    g187: BSplineCurve PolesCount=3 KnotsCount=2 Degree=2 IsPeriodic=0
    g188: BSplineCurve PolesCount=3 KnotsCount=2 Degree=2 IsPeriodic=0
    g189: BSplineCurve PolesCount=3 KnotsCount=2 Degree=2 IsPeriodic=0
    g190: BSplineCurve PolesCount=3 KnotsCount=2 Degree=2 IsPeriodic=0
    g191: BSplineCurve PolesCount=3 KnotsCount=2 Degree=2 IsPeriodic=0
    g192: BSplineCurve PolesCount=3 KnotsCount=2 Degree=2 IsPeriodic=0
    g193: BSplineCurve PolesCount=3 KnotsCount=2 Degree=2 IsPeriodic=0
    g194: LineSegment StartX=-10.4767 StartY=40.6533 StartZ=0 EndX=-10.4767 EndY=40.9422 EndZ=0
    g195: BSplineCurve PolesCount=3 KnotsCount=2 Degree=2 IsPeriodic=0
    g196: BSplineCurve PolesCount=3 KnotsCount=2 Degree=2 IsPeriodic=0
    g197: BSplineCurve PolesCount=3 KnotsCount=2 Degree=2 IsPeriodic=0
    g198: BSplineCurve PolesCount=3 KnotsCount=2 Degree=2 IsPeriodic=0
    g199: BSplineCurve PolesCount=3 KnotsCount=2 Degree=2 IsPeriodic=0
    g200: BSplineCurve PolesCount=3 KnotsCount=2 Degree=2 IsPeriodic=0
    g201: BSplineCurve PolesCount=3 KnotsCount=2 Degree=2 IsPeriodic=0
    g202: BSplineCurve PolesCount=3 KnotsCount=2 Degree=2 IsPeriodic=0
    g203: BSplineCurve PolesCount=3 KnotsCount=2 Degree=2 IsPeriodic=0
    g204: BSplineCurve PolesCount=3 KnotsCount=2 Degree=2 IsPeriodic=0
    g205: LineSegment StartX=-11.8835 StartY=41.7539 StartZ=0 EndX=-12.2273 EndY=41.7539 EndZ=0
    g206: BSplineCurve PolesCount=3 KnotsCount=2 Degree=2 IsPeriodic=0
    g207: BSplineCurve PolesCount=3 KnotsCount=2 Degree=2 IsPeriodic=0
    g208: BSplineCurve PolesCount=3 KnotsCount=2 Degree=2 IsPeriodic=0
    g209: BSplineCurve PolesCount=3 KnotsCount=2 Degree=2 IsPeriodic=0
    g210: BSplineCurve PolesCount=3 KnotsCount=2 Degree=2 IsPeriodic=0
    g211: BSplineCurve PolesCount=3 KnotsCount=2 Degree=2 IsPeriodic=0
    g212: BSplineCurve PolesCount=3 KnotsCount=2 Degree=2 IsPeriodic=0
    g213: BSplineCurve PolesCount=3 KnotsCount=2 Degree=2 IsPeriodic=0
    g214: LineSegment StartX=-12.8108 StartY=41.5633 StartZ=0 EndX=-12.8108 EndY=41.2686 EndZ=0
    g215: BSplineCurve PolesCount=3 KnotsCount=2 Degree=2 IsPeriodic=0
    g216: BSplineCurve PolesCount=3 KnotsCount=2 Degree=2 IsPeriodic=0
    g217: BSplineCurve PolesCount=3 KnotsCount=2 Degree=2 IsPeriodic=0
    g218: BSplineCurve PolesCount=3 KnotsCount=2 Degree=2 IsPeriodic=0
    g219: BSplineCurve PolesCount=3 KnotsCount=2 Degree=2 IsPeriodic=0
    g220: BSplineCurve PolesCount=3 KnotsCount=2 Degree=2 IsPeriodic=0
    g221: BSplineCurve PolesCount=3 KnotsCount=2 Degree=2 IsPeriodic=0
    g222: BSplineCurve PolesCount=3 KnotsCount=2 Degree=2 IsPeriodic=0
    g223: BSplineCurve PolesCount=3 KnotsCount=2 Degree=2 IsPeriodic=0
    g224: BSplineCurve PolesCount=3 KnotsCount=2 Degree=2 IsPeriodic=0
    g225: LineSegment StartX=-11.8662 StartY=40.9422 StartZ=0 EndX=-11.8662 EndY=40.6533 EndZ=0
    g226: BSplineCurve PolesCount=3 KnotsCount=2 Degree=2 IsPeriodic=0
    g227: BSplineCurve PolesCount=3 KnotsCount=2 Degree=2 IsPeriodic=0
    g228: BSplineCurve PolesCount=3 KnotsCount=2 Degree=2 IsPeriodic=0
    g229: BSplineCurve PolesCount=3 KnotsCount=2 Degree=2 IsPeriodic=0
    g230: BSplineCurve PolesCount=3 KnotsCount=2 Degree=2 IsPeriodic=0
    g231: BSplineCurve PolesCount=3 KnotsCount=2 Degree=2 IsPeriodic=0
    g232: BSplineCurve PolesCount=3 KnotsCount=2 Degree=2 IsPeriodic=0
    g233: BSplineCurve PolesCount=3 KnotsCount=2 Degree=2 IsPeriodic=0
    g234: BSplineCurve PolesCount=3 KnotsCount=2 Degree=2 IsPeriodic=0
    g235: BSplineCurve PolesCount=3 KnotsCount=2 Degree=2 IsPeriodic=0
    g236: LineSegment StartX=-12.8108 StartY=40.3269 StartZ=0 EndX=-12.8108 EndY=40.0467 EndZ=0
    g237: LineSegment StartX=-12.8108 StartY=40.0467 StartZ=0 EndX=-13.1546 EndY=40.0467 EndZ=0
    g238: LineSegment StartX=-13.1546 StartY=40.0467 StartZ=0 EndX=-13.1546 EndY=41.5633 EndZ=0
    g239: BSplineCurve PolesCount=3 KnotsCount=2 Degree=2 IsPeriodic=0
    g240: BSplineCurve PolesCount=3 KnotsCount=2 Degree=2 IsPeriodic=0
    g241: BSplineCurve PolesCount=3 KnotsCount=2 Degree=2 IsPeriodic=0
    g242: BSplineCurve PolesCount=3 KnotsCount=2 Degree=2 IsPeriodic=0
    g243: BSplineCurve PolesCount=3 KnotsCount=2 Degree=2 IsPeriodic=0
    g244: BSplineCurve PolesCount=3 KnotsCount=2 Degree=2 IsPeriodic=0
    g245: BSplineCurve PolesCount=3 KnotsCount=2 Degree=2 IsPeriodic=0
    g246: BSplineCurve PolesCount=3 KnotsCount=2 Degree=2 IsPeriodic=0
    g247: BSplineCurve PolesCount=3 KnotsCount=2 Degree=2 IsPeriodic=0
    g248: BSplineCurve PolesCount=3 KnotsCount=2 Degree=2 IsPeriodic=0
    g249: LineSegment StartX=-12.8108 StartY=40.9422 StartZ=0 EndX=-12.8108 EndY=40.6533 EndZ=0
    g250: BSplineCurve PolesCount=3 KnotsCount=2 Degree=2 IsPeriodic=0
    g251: BSplineCurve PolesCount=3 KnotsCount=2 Degree=2 IsPeriodic=0
    g252: BSplineCurve PolesCount=3 KnotsCount=2 Degree=2 IsPeriodic=0
    g253: BSplineCurve PolesCount=3 KnotsCount=2 Degree=2 IsPeriodic=0
    g254: BSplineCurve PolesCount=3 KnotsCount=2 Degree=2 IsPeriodic=0
    g255: BSplineCurve PolesCount=3 KnotsCount=2 Degree=2 IsPeriodic=0
    g256: BSplineCurve PolesCount=3 KnotsCount=2 Degree=2 IsPeriodic=0
    g257: BSplineCurve PolesCount=3 KnotsCount=2 Degree=2 IsPeriodic=0
    g258: LineSegment StartX=-12.21 StartY=40.6533 StartZ=0 EndX=-12.21 EndY=40.9422 EndZ=0
    g259: BSplineCurve PolesCount=3 KnotsCount=2 Degree=2 IsPeriodic=0
    g260: BSplineCurve PolesCount=3 KnotsCount=2 Degree=2 IsPeriodic=0
    g261: BSplineCurve PolesCount=3 KnotsCount=2 Degree=2 IsPeriodic=0
    g262: BSplineCurve PolesCount=3 KnotsCount=2 Degree=2 IsPeriodic=0
    g263: LineSegment StartX=-13.8103 StartY=41.5488 StartZ=0 EndX=-13.8103 EndY=40.0467 EndZ=0
    g264: LineSegment StartX=-13.8103 StartY=40.0467 StartZ=0 EndX=-14.1541 EndY=40.0467 EndZ=0
    g265: LineSegment StartX=-14.1541 StartY=40.0467 StartZ=0 EndX=-14.1541 EndY=40.4424 EndZ=0
    g266: BSplineCurve PolesCount=3 KnotsCount=2 Degree=2 IsPeriodic=0
    g267: BSplineCurve PolesCount=3 KnotsCount=2 Degree=2 IsPeriodic=0
    g268: BSplineCurve PolesCount=3 KnotsCount=2 Degree=2 IsPeriodic=0
    g269: BSplineCurve PolesCount=3 KnotsCount=2 Degree=2 IsPeriodic=0
    g270: BSplineCurve PolesCount=3 KnotsCount=2 Degree=2 IsPeriodic=0
    g271: BSplineCurve PolesCount=3 KnotsCount=2 Degree=2 IsPeriodic=0
    g272: LineSegment StartX=-14.8965 StartY=40.0236 StartZ=0 EndX=-14.8965 EndY=40.3384 EndZ=0
    g273: BSplineCurve PolesCount=3 KnotsCount=2 Degree=2 IsPeriodic=0
    g274: BSplineCurve PolesCount=3 KnotsCount=2 Degree=2 IsPeriodic=0
    g275: BSplineCurve PolesCount=3 KnotsCount=2 Degree=2 IsPeriodic=0
    g276: BSplineCurve PolesCount=3 KnotsCount=2 Degree=2 IsPeriodic=0
    g277: BSplineCurve PolesCount=3 KnotsCount=2 Degree=2 IsPeriodic=0
    g278: BSplineCurve PolesCount=3 KnotsCount=2 Degree=2 IsPeriodic=0
    g279: BSplineCurve PolesCount=3 KnotsCount=2 Degree=2 IsPeriodic=0
    g280: BSplineCurve PolesCount=3 KnotsCount=2 Degree=2 IsPeriodic=0
    g281: BSplineCurve PolesCount=3 KnotsCount=2 Degree=2 IsPeriodic=0
    g282: BSplineCurve PolesCount=3 KnotsCount=2 Degree=2 IsPeriodic=0
    g283: LineSegment StartX=-14.1541 StartY=40.7515 StartZ=0 EndX=-14.1541 EndY=41.5488 EndZ=0
    g284: LineSegment StartX=-14.1541 StartY=41.5488 StartZ=0 EndX=-13.8103 EndY=41.5488 EndZ=0
    g285: BSplineCurve PolesCount=3 KnotsCount=2 Degree=2 IsPeriodic=0
    g286: BSplineCurve PolesCount=3 KnotsCount=2 Degree=2 IsPeriodic=0
    g287: BSplineCurve PolesCount=3 KnotsCount=2 Degree=2 IsPeriodic=0
    g288: BSplineCurve PolesCount=3 KnotsCount=2 Degree=2 IsPeriodic=0
    g289: BSplineCurve PolesCount=3 KnotsCount=2 Degree=2 IsPeriodic=0
    g290: BSplineCurve PolesCount=3 KnotsCount=2 Degree=2 IsPeriodic=0
    g291: BSplineCurve PolesCount=3 KnotsCount=2 Degree=2 IsPeriodic=0
    g292: BSplineCurve PolesCount=3 KnotsCount=2 Degree=2 IsPeriodic=0
    g293: BSplineCurve PolesCount=3 KnotsCount=2 Degree=2 IsPeriodic=0
    g294: BSplineCurve PolesCount=3 KnotsCount=2 Degree=2 IsPeriodic=0
    g295: BSplineCurve PolesCount=3 KnotsCount=2 Degree=2 IsPeriodic=0
    g296: BSplineCurve PolesCount=3 KnotsCount=2 Degree=2 IsPeriodic=0
    g297: LineSegment StartX=-16.052 StartY=40.6302 StartZ=0 EndX=-16.2831 EndY=40.6302 EndZ=0
    g298: LineSegment StartX=-16.2831 StartY=40.6302 StartZ=0 EndX=-16.2831 EndY=40.5551 EndZ=0
    g299: BSplineCurve PolesCount=3 KnotsCount=2 Degree=2 IsPeriodic=0
    g300: BSplineCurve PolesCount=3 KnotsCount=2 Degree=2 IsPeriodic=0
    g301: BSplineCurve PolesCount=3 KnotsCount=2 Degree=2 IsPeriodic=0
    g302: BSplineCurve PolesCount=3 KnotsCount=2 Degree=2 IsPeriodic=0
    g303: BSplineCurve PolesCount=3 KnotsCount=2 Degree=2 IsPeriodic=0
    g304: BSplineCurve PolesCount=3 KnotsCount=2 Degree=2 IsPeriodic=0
    g305: BSplineCurve PolesCount=3 KnotsCount=2 Degree=2 IsPeriodic=0
    g306: BSplineCurve PolesCount=3 KnotsCount=2 Degree=2 IsPeriodic=0
    g307: LineSegment StartX=-15.688 StartY=40.4887 StartZ=0 EndX=-15.688 EndY=40.4915 EndZ=0
    g308: LineSegment StartX=-15.688 StartY=40.4915 StartZ=0 EndX=-15.35 EndY=40.4915 EndZ=0
    g309: LineSegment StartX=-15.35 StartY=40.4915 StartZ=0 EndX=-15.35 EndY=40.4829 EndZ=0
    g310: BSplineCurve PolesCount=3 KnotsCount=2 Degree=2 IsPeriodic=0
    g311: BSplineCurve PolesCount=3 KnotsCount=2 Degree=2 IsPeriodic=0
    g312: BSplineCurve PolesCount=3 KnotsCount=2 Degree=2 IsPeriodic=0
    g313: BSplineCurve PolesCount=3 KnotsCount=2 Degree=2 IsPeriodic=0
    g314: BSplineCurve PolesCount=3 KnotsCount=2 Degree=2 IsPeriodic=0
    g315: BSplineCurve PolesCount=3 KnotsCount=2 Degree=2 IsPeriodic=0
    g316: BSplineCurve PolesCount=3 KnotsCount=2 Degree=2 IsPeriodic=0
    g317: BSplineCurve PolesCount=3 KnotsCount=2 Degree=2 IsPeriodic=0
    g318: BSplineCurve PolesCount=3 KnotsCount=2 Degree=2 IsPeriodic=0
    g319: BSplineCurve PolesCount=3 KnotsCount=2 Degree=2 IsPeriodic=0
    g320: BSplineCurve PolesCount=3 KnotsCount=2 Degree=2 IsPeriodic=0
    g321: BSplineCurve PolesCount=3 KnotsCount=2 Degree=2 IsPeriodic=0
    g322: LineSegment StartX=-16.6211 StartY=40.5551 StartZ=0 EndX=-16.6211 EndY=41.5488 EndZ=0
    g323: LineSegment StartX=-16.6211 StartY=41.5488 StartZ=0 EndX=-16.2831 EndY=41.5488 EndZ=0
    g324: LineSegment StartX=-16.2831 StartY=41.5488 StartZ=0 EndX=-16.2831 EndY=41.2975 EndZ=0
    g325: BSplineCurve PolesCount=3 KnotsCount=2 Degree=2 IsPeriodic=0
    g326: BSplineCurve PolesCount=3 KnotsCount=2 Degree=2 IsPeriodic=0
    g327: BSplineCurve PolesCount=3 KnotsCount=2 Degree=2 IsPeriodic=0
    g328: BSplineCurve PolesCount=3 KnotsCount=2 Degree=2 IsPeriodic=0
    g329: BSplineCurve PolesCount=3 KnotsCount=2 Degree=2 IsPeriodic=0
    g330: BSplineCurve PolesCount=3 KnotsCount=2 Degree=2 IsPeriodic=0
    g331: BSplineCurve PolesCount=3 KnotsCount=2 Degree=2 IsPeriodic=0
    g332: BSplineCurve PolesCount=3 KnotsCount=2 Degree=2 IsPeriodic=0
    g333: LineSegment StartX=-16.2831 StartY=41.0028 StartZ=0 EndX=-16.2831 EndY=40.9162 EndZ=0
    g334: LineSegment StartX=-16.2831 StartY=40.9162 StartZ=0 EndX=-16.052 EndY=40.9162 EndZ=0
    g335: BSplineCurve PolesCount=3 KnotsCount=2 Degree=2 IsPeriodic=0
    g336: BSplineCurve PolesCount=3 KnotsCount=2 Degree=2 IsPeriodic=0
    g337: BSplineCurve PolesCount=3 KnotsCount=2 Degree=2 IsPeriodic=0
    g338: BSplineCurve PolesCount=3 KnotsCount=2 Degree=2 IsPeriodic=0
    g339: BSplineCurve PolesCount=3 KnotsCount=2 Degree=2 IsPeriodic=0
    g340: BSplineCurve PolesCount=3 KnotsCount=2 Degree=2 IsPeriodic=0
    g341: BSplineCurve PolesCount=3 KnotsCount=2 Degree=2 IsPeriodic=0
    g342: BSplineCurve PolesCount=3 KnotsCount=2 Degree=2 IsPeriodic=0
    g343: BSplineCurve PolesCount=3 KnotsCount=2 Degree=2 IsPeriodic=0
    g344: BSplineCurve PolesCount=3 KnotsCount=2 Degree=2 IsPeriodic=0
    g345: LineSegment StartX=-17.0891 StartY=42.1699 StartZ=0 EndX=-17.0891 EndY=40.0467 EndZ=0
    g346: LineSegment StartX=-17.0891 StartY=40.0467 StartZ=0 EndX=-17.4328 EndY=40.0467 EndZ=0
    g347: LineSegment StartX=-17.4328 StartY=40.0467 StartZ=0 EndX=-17.4328 EndY=40.3269 EndZ=0
    g348: BSplineCurve PolesCount=3 KnotsCount=2 Degree=2 IsPeriodic=0
    g349: BSplineCurve PolesCount=3 KnotsCount=2 Degree=2 IsPeriodic=0
    g350: BSplineCurve PolesCount=3 KnotsCount=2 Degree=2 IsPeriodic=0
    g351: BSplineCurve PolesCount=3 KnotsCount=2 Degree=2 IsPeriodic=0
    g352: BSplineCurve PolesCount=3 KnotsCount=2 Degree=2 IsPeriodic=0
    g353: BSplineCurve PolesCount=3 KnotsCount=2 Degree=2 IsPeriodic=0
    g354: BSplineCurve PolesCount=3 KnotsCount=2 Degree=2 IsPeriodic=0
    g355: BSplineCurve PolesCount=3 KnotsCount=2 Degree=2 IsPeriodic=0
    g356: BSplineCurve PolesCount=3 KnotsCount=2 Degree=2 IsPeriodic=0
    g357: BSplineCurve PolesCount=3 KnotsCount=2 Degree=2 IsPeriodic=0
    g358: LineSegment StartX=-18.3774 StartY=40.6533 StartZ=0 EndX=-18.3774 EndY=40.9422 EndZ=0
    g359: BSplineCurve PolesCount=3 KnotsCount=2 Degree=2 IsPeriodic=0
    g360: BSplineCurve PolesCount=3 KnotsCount=2 Degree=2 IsPeriodic=0
    g361: BSplineCurve PolesCount=3 KnotsCount=2 Degree=2 IsPeriodic=0
    g362: BSplineCurve PolesCount=3 KnotsCount=2 Degree=2 IsPeriodic=0
    g363: BSplineCurve PolesCount=3 KnotsCount=2 Degree=2 IsPeriodic=0
    g364: BSplineCurve PolesCount=3 KnotsCount=2 Degree=2 IsPeriodic=0
    g365: BSplineCurve PolesCount=3 KnotsCount=2 Degree=2 IsPeriodic=0
    g366: BSplineCurve PolesCount=3 KnotsCount=2 Degree=2 IsPeriodic=0
    g367: BSplineCurve PolesCount=3 KnotsCount=2 Degree=2 IsPeriodic=0
    g368: BSplineCurve PolesCount=3 KnotsCount=2 Degree=2 IsPeriodic=0
    g369: LineSegment StartX=-17.4328 StartY=41.2686 StartZ=0 EndX=-17.4328 EndY=42.1699 EndZ=0
    g370: LineSegment StartX=-17.4328 StartY=42.1699 StartZ=0 EndX=-17.0891 EndY=42.1699 EndZ=0
    g371: BSplineCurve PolesCount=3 KnotsCount=2 Degree=2 IsPeriodic=0
    g372: BSplineCurve PolesCount=3 KnotsCount=2 Degree=2 IsPeriodic=0
    g373: BSplineCurve PolesCount=3 KnotsCount=2 Degree=2 IsPeriodic=0
    g374: BSplineCurve PolesCount=3 KnotsCount=2 Degree=2 IsPeriodic=0
    g375: LineSegment StartX=-18.0337 StartY=40.9422 StartZ=0 EndX=-18.0337 EndY=40.6533 EndZ=0
    g376: BSplineCurve PolesCount=3 KnotsCount=2 Degree=2 IsPeriodic=0
    g377: BSplineCurve PolesCount=3 KnotsCount=2 Degree=2 IsPeriodic=0
    g378: BSplineCurve PolesCount=3 KnotsCount=2 Degree=2 IsPeriodic=0
    g379: BSplineCurve PolesCount=3 KnotsCount=2 Degree=2 IsPeriodic=0
    g380: BSplineCurve PolesCount=3 KnotsCount=2 Degree=2 IsPeriodic=0
    g381: BSplineCurve PolesCount=3 KnotsCount=2 Degree=2 IsPeriodic=0
    g382: BSplineCurve PolesCount=3 KnotsCount=2 Degree=2 IsPeriodic=0
    g383: BSplineCurve PolesCount=3 KnotsCount=2 Degree=2 IsPeriodic=0
    g384: LineSegment StartX=-17.4328 StartY=40.6533 StartZ=0 EndX=-17.4328 EndY=40.9422 EndZ=0
    g385: BSplineCurve PolesCount=3 KnotsCount=2 Degree=2 IsPeriodic=0
    g386: BSplineCurve PolesCount=3 KnotsCount=2 Degree=2 IsPeriodic=0
    g387: BSplineCurve PolesCount=3 KnotsCount=2 Degree=2 IsPeriodic=0
    g388: BSplineCurve PolesCount=3 KnotsCount=2 Degree=2 IsPeriodic=0
    g389: LineSegment StartX=-18.8223 StartY=41.5488 StartZ=0 EndX=-18.8223 EndY=39.4256 EndZ=0
    g390: LineSegment StartX=-18.8223 StartY=39.4256 StartZ=0 EndX=-19.1661 EndY=39.4256 EndZ=0
    g391: LineSegment StartX=-19.1661 StartY=39.4256 StartZ=0 EndX=-19.1661 EndY=40.324 EndZ=0
    g392: BSplineCurve PolesCount=3 KnotsCount=2 Degree=2 IsPeriodic=0
    g393: BSplineCurve PolesCount=3 KnotsCount=2 Degree=2 IsPeriodic=0
    g394: BSplineCurve PolesCount=3 KnotsCount=2 Degree=2 IsPeriodic=0
    g395: BSplineCurve PolesCount=3 KnotsCount=2 Degree=2 IsPeriodic=0
    g396: BSplineCurve PolesCount=3 KnotsCount=2 Degree=2 IsPeriodic=0
    g397: BSplineCurve PolesCount=3 KnotsCount=2 Degree=2 IsPeriodic=0
    g398: BSplineCurve PolesCount=3 KnotsCount=2 Degree=2 IsPeriodic=0
    g399: BSplineCurve PolesCount=3 KnotsCount=2 Degree=2 IsPeriodic=0
    ... +160 more geometry lines
  constraints (4):
    c: Horizontal(g0)
    c: DistanceX(g0,g-4) = 3
    c: DistanceX(g-3,g0) = 3
    c: T21(g0,g1,g2)
FEATURE [PartDesign::Pocket] Pocket007
  BaseFeature = -> AdditiveLoft005
  Direction = (0,1,-2e-16)
  Length = 1
  Length2 = 5
  Profile = -> Sketch019
  ReferenceAxis = -> Sketch019 [N_Axis]
  Refine = true
  SideType = 0
  Suppressed = false
  Type = 0
  Type2 = 0
FEATURE [PartDesign::Body] Body003  label="CartographerV3"
  AllowCompound = true
  Group = -> [Sketch020,Sketch021,Pad010,Pad011,Sketch022,MirroredSketch002,Clone2D003,Pocket008,AdditiveLoft004,Chamfer002,Sketch023,Pocket009,Chamfer003,Sketch024,Sketch025,AdditiveLoft005,Sketch019,Pocket007]
  Origin = -> Origin010
  Placement = pos=(0,0,0) rot=(0,0,1;6.13955rad)
  Tip = -> Pocket007
FEATURE [App::Point] Origin013  label="Origin015"
  Role = Origin
FEATURE [Sketcher::SketchObject] Sketch027
  ArcFitTolerance = 1e-06
  AttachmentOffset = pos=(-16,-2.27,43.3) rot=(0,0,1;0rad)
  AttachmentSupport = -> [Origin012]
  ExternalTypes = [0,0]
  FullyConstrained = true
  MakeInternals = false
  MapMode = 5
  Placement = pos=(-16,-2.27,43.3) rot=(0,0,1;0rad)
  _ExternalGeoVersion = 0
  sketch-geometry (4):
    g0: ArcOfCircle CenterX=-15.8 CenterY=0 CenterZ=0 NormalX=0 NormalY=0 NormalZ=1 AngleXU=0 Radius=4 StartAngle=0.125328 EndAngle=4.71239
    g1: ArcOfCircle CenterX=15.8 CenterY=0 CenterZ=0 NormalX=0 NormalY=0 NormalZ=1 AngleXU=0 Radius=4 StartAngle=4.71239 EndAngle=9.29945
    g2: LineSegment StartX=-15.8 StartY=-4 StartZ=0 EndX=15.8 EndY=-4 EndZ=0
    g3: LineSegment StartX=-11.8314 StartY=0.5 StartZ=0 EndX=11.8314 EndY=0.5 EndZ=0
  constraints (12):
    c: DistanceX(g0,g1) = 31.6
    c: Vertical(g2,g1)
    c: Symmetric(g0,g1,g-2)
    c: Symmetric(g2,g2,g-2)
    c: Horizontal(g3)
    c: PointOnObject(g0,g-1)
    c: DistanceY(g2,g3) = 4.5
    c: DistanceY(g2,g0) = 4
    c: Coincident(g3,g1)
    c: Coincident(g1,g2)
    c: Coincident(g3,g0)
    c: Coincident(g0,g2)
FEATURE [PartDesign::Pad] Pad012
  Direction = (0,0,1)
  Length = 22
  Length2 = 10
  Profile = -> Sketch027
  ReferenceAxis = -> Sketch027 [N_Axis]
  Refine = true
  Reversed = true
  SideType = 0
  Suppressed = false
  Type = 0
  Type2 = 0
FEATURE [Sketcher::SketchObject] Sketch028
  ArcFitTolerance = 1e-06
  AttachmentSupport = -> [Origin012]
  ExternalTypes = [0]
  FullyConstrained = true
  MakeInternals = false
  MapMode = 5
  _ExternalGeoVersion = 0
  expr: Constraints[11] = 5 + 3.5 / 2
  sketch-geometry (6):
    g0: LineSegment StartX=-13.5 StartY=-5.575 StartZ=0 EndX=13.5 EndY=-5.575 EndZ=0
    g1: LineSegment StartX=13.5 StartY=-5.575 StartZ=0 EndX=13.5 EndY=5.575 EndZ=0
    g2: Circle CenterX=-9 CenterY=1.175 CenterZ=0 NormalX=0 NormalY=0 NormalZ=1 AngleXU=0 Radius=1.75
    g3: Circle CenterX=9 CenterY=1.175 CenterZ=0 NormalX=0 NormalY=0 NormalZ=1 AngleXU=0 Radius=1.75
    g4: LineSegment StartX=-13.5 StartY=-5.575 StartZ=0 EndX=-13.5 EndY=5.575 EndZ=0
    g5: LineSegment StartX=-13.5 StartY=5.575 StartZ=0 EndX=13.5 EndY=5.575 EndZ=0
  constraints (16):
    c: Equal(g3,g2)
    c: Diameter(g3) = 3.5
    c: Symmetric(g2,g3,g-2)
    c: Coincident(g4,g0)
    c: Vertical(g4)
    c: Coincident(g5,g4)
    c: Coincident(g5,g1)
    c: Horizontal(g5)
    c: DistanceY(g4,g4) = 11.15
    c: Symmetric(g4,g0,g-1)
    c: DistanceX(g5,g5) = 27
    c: DistanceY(g0,g2) = 6.75
    c: DistanceX(g2,g3) = 18
    c: Horizontal(g0)
    c: Vertical(g1)
    c: Coincident(g1,g0)
FEATURE [PartDesign::Pad] Pad013
  BaseFeature = -> Pad012
  Direction = (0,0,1)
  Length = 3
  Length2 = 10
  Profile = -> Sketch028
  ReferenceAxis = -> Sketch028 [N_Axis]
  Refine = true
  SideType = 0
  Suppressed = false
  Type = 0
  Type2 = 0
FEATURE [Sketcher::SketchObject] MirroredSketch003
  ArcFitTolerance = 1e-06
  AttachmentOffset = pos=(14,-18,0) rot=(0,0,1;0rad)
  AttachmentSupport = -> [Pad013]
  ExternalTypes = [0]
  FullyConstrained = false
  MakeInternals = false
  MapMode = 5
  Placement = pos=(-14,-1.77,-18) rot=(0,0.707107,0.707107;3.14159rad)
  _ExternalGeoVersion = 0
  sketch-geometry (160):
    g0: BSplineCurve PolesCount=4 KnotsCount=2 Degree=3 IsPeriodic=0
    g1: BSplineCurve PolesCount=4 KnotsCount=2 Degree=3 IsPeriodic=0
    g2: BSplineCurve PolesCount=4 KnotsCount=2 Degree=3 IsPeriodic=0
    g3: BSplineCurve PolesCount=4 KnotsCount=2 Degree=3 IsPeriodic=0
    g4: BSplineCurve PolesCount=4 KnotsCount=2 Degree=3 IsPeriodic=0
    g5: BSplineCurve PolesCount=4 KnotsCount=2 Degree=3 IsPeriodic=0
    g6: BSplineCurve PolesCount=4 KnotsCount=2 Degree=3 IsPeriodic=0
    g7: BSplineCurve PolesCount=4 KnotsCount=2 Degree=3 IsPeriodic=0
    g8: BSplineCurve PolesCount=4 KnotsCount=2 Degree=3 IsPeriodic=0
    g9: BSplineCurve PolesCount=4 KnotsCount=2 Degree=3 IsPeriodic=0
    g10: BSplineCurve PolesCount=4 KnotsCount=2 Degree=3 IsPeriodic=0
    g11: BSplineCurve PolesCount=4 KnotsCount=2 Degree=3 IsPeriodic=0
    g12: BSplineCurve PolesCount=4 KnotsCount=2 Degree=3 IsPeriodic=0
    g13: BSplineCurve PolesCount=4 KnotsCount=2 Degree=3 IsPeriodic=0
    g14: BSplineCurve PolesCount=4 KnotsCount=2 Degree=3 IsPeriodic=0
    g15: BSplineCurve PolesCount=4 KnotsCount=2 Degree=3 IsPeriodic=0
    g16: BSplineCurve PolesCount=4 KnotsCount=2 Degree=3 IsPeriodic=0
    g17: BSplineCurve PolesCount=4 KnotsCount=2 Degree=3 IsPeriodic=0
    g18: BSplineCurve PolesCount=4 KnotsCount=2 Degree=3 IsPeriodic=0
    g19: BSplineCurve PolesCount=4 KnotsCount=2 Degree=3 IsPeriodic=0
    g20: BSplineCurve PolesCount=4 KnotsCount=2 Degree=3 IsPeriodic=0
    g21: BSplineCurve PolesCount=4 KnotsCount=2 Degree=3 IsPeriodic=0
    g22: BSplineCurve PolesCount=4 KnotsCount=2 Degree=3 IsPeriodic=0
    g23: BSplineCurve PolesCount=4 KnotsCount=2 Degree=3 IsPeriodic=0
    g24: BSplineCurve PolesCount=4 KnotsCount=2 Degree=3 IsPeriodic=0
    g25: BSplineCurve PolesCount=4 KnotsCount=2 Degree=3 IsPeriodic=0
    g26: BSplineCurve PolesCount=4 KnotsCount=2 Degree=3 IsPeriodic=0
    g27: BSplineCurve PolesCount=4 KnotsCount=2 Degree=3 IsPeriodic=0
    g28: BSplineCurve PolesCount=4 KnotsCount=2 Degree=3 IsPeriodic=0
    g29: BSplineCurve PolesCount=4 KnotsCount=2 Degree=3 IsPeriodic=0
    g30: BSplineCurve PolesCount=4 KnotsCount=2 Degree=3 IsPeriodic=0
    g31: BSplineCurve PolesCount=4 KnotsCount=2 Degree=3 IsPeriodic=0
    g32: BSplineCurve PolesCount=4 KnotsCount=2 Degree=3 IsPeriodic=0
    g33: BSplineCurve PolesCount=4 KnotsCount=2 Degree=3 IsPeriodic=0
    g34: BSplineCurve PolesCount=4 KnotsCount=2 Degree=3 IsPeriodic=0
    g35: BSplineCurve PolesCount=4 KnotsCount=2 Degree=3 IsPeriodic=0
    g36: BSplineCurve PolesCount=4 KnotsCount=2 Degree=3 IsPeriodic=0
    g37: BSplineCurve PolesCount=4 KnotsCount=2 Degree=3 IsPeriodic=0
    g38: BSplineCurve PolesCount=4 KnotsCount=2 Degree=3 IsPeriodic=0
    g39: BSplineCurve PolesCount=4 KnotsCount=2 Degree=3 IsPeriodic=0
    g40: BSplineCurve PolesCount=4 KnotsCount=2 Degree=3 IsPeriodic=0
    g41: BSplineCurve PolesCount=4 KnotsCount=2 Degree=3 IsPeriodic=0
    g42: BSplineCurve PolesCount=4 KnotsCount=2 Degree=3 IsPeriodic=0
    g43: BSplineCurve PolesCount=4 KnotsCount=2 Degree=3 IsPeriodic=0
    g44: BSplineCurve PolesCount=4 KnotsCount=2 Degree=3 IsPeriodic=0
    g45: BSplineCurve PolesCount=4 KnotsCount=2 Degree=3 IsPeriodic=0
    g46: BSplineCurve PolesCount=4 KnotsCount=2 Degree=3 IsPeriodic=0
    g47: BSplineCurve PolesCount=4 KnotsCount=2 Degree=3 IsPeriodic=0
    g48: BSplineCurve PolesCount=4 KnotsCount=2 Degree=3 IsPeriodic=0
    g49: BSplineCurve PolesCount=4 KnotsCount=2 Degree=3 IsPeriodic=0
    g50: BSplineCurve PolesCount=4 KnotsCount=2 Degree=3 IsPeriodic=0
    g51: BSplineCurve PolesCount=4 KnotsCount=2 Degree=3 IsPeriodic=0
    g52: BSplineCurve PolesCount=4 KnotsCount=2 Degree=3 IsPeriodic=0
    g53: BSplineCurve PolesCount=4 KnotsCount=2 Degree=3 IsPeriodic=0
    g54: BSplineCurve PolesCount=4 KnotsCount=2 Degree=3 IsPeriodic=0
    g55: BSplineCurve PolesCount=4 KnotsCount=2 Degree=3 IsPeriodic=0
    g56: BSplineCurve PolesCount=4 KnotsCount=2 Degree=3 IsPeriodic=0
    g57: BSplineCurve PolesCount=4 KnotsCount=2 Degree=3 IsPeriodic=0
    g58: BSplineCurve PolesCount=4 KnotsCount=2 Degree=3 IsPeriodic=0
    g59: BSplineCurve PolesCount=4 KnotsCount=2 Degree=3 IsPeriodic=0
    g60: BSplineCurve PolesCount=4 KnotsCount=2 Degree=3 IsPeriodic=0
    g61: BSplineCurve PolesCount=4 KnotsCount=2 Degree=3 IsPeriodic=0
    g62: BSplineCurve PolesCount=4 KnotsCount=2 Degree=3 IsPeriodic=0
    g63: BSplineCurve PolesCount=4 KnotsCount=2 Degree=3 IsPeriodic=0
    g64: BSplineCurve PolesCount=4 KnotsCount=2 Degree=3 IsPeriodic=0
    g65: BSplineCurve PolesCount=4 KnotsCount=2 Degree=3 IsPeriodic=0
    g66: BSplineCurve PolesCount=4 KnotsCount=2 Degree=3 IsPeriodic=0
    g67: BSplineCurve PolesCount=4 KnotsCount=2 Degree=3 IsPeriodic=0
    g68: BSplineCurve PolesCount=4 KnotsCount=2 Degree=3 IsPeriodic=0
    g69: BSplineCurve PolesCount=4 KnotsCount=2 Degree=3 IsPeriodic=0
    g70: BSplineCurve PolesCount=4 KnotsCount=2 Degree=3 IsPeriodic=0
    g71: BSplineCurve PolesCount=4 KnotsCount=2 Degree=3 IsPeriodic=0
    g72: BSplineCurve PolesCount=4 KnotsCount=2 Degree=3 IsPeriodic=0
    g73: BSplineCurve PolesCount=4 KnotsCount=2 Degree=3 IsPeriodic=0
    g74: BSplineCurve PolesCount=4 KnotsCount=2 Degree=3 IsPeriodic=0
    g75: BSplineCurve PolesCount=4 KnotsCount=2 Degree=3 IsPeriodic=0
    g76: BSplineCurve PolesCount=4 KnotsCount=2 Degree=3 IsPeriodic=0
    g77: BSplineCurve PolesCount=4 KnotsCount=2 Degree=3 IsPeriodic=0
    g78: BSplineCurve PolesCount=4 KnotsCount=2 Degree=3 IsPeriodic=0
    g79: BSplineCurve PolesCount=4 KnotsCount=2 Degree=3 IsPeriodic=0
    g80: BSplineCurve PolesCount=4 KnotsCount=2 Degree=3 IsPeriodic=0
    g81: BSplineCurve PolesCount=4 KnotsCount=2 Degree=3 IsPeriodic=0
    g82: BSplineCurve PolesCount=4 KnotsCount=2 Degree=3 IsPeriodic=0
    g83: BSplineCurve PolesCount=4 KnotsCount=2 Degree=3 IsPeriodic=0
    g84: BSplineCurve PolesCount=4 KnotsCount=2 Degree=3 IsPeriodic=0
    g85: BSplineCurve PolesCount=4 KnotsCount=2 Degree=3 IsPeriodic=0
    g86: BSplineCurve PolesCount=4 KnotsCount=2 Degree=3 IsPeriodic=0
    g87: BSplineCurve PolesCount=4 KnotsCount=2 Degree=3 IsPeriodic=0
    g88: BSplineCurve PolesCount=4 KnotsCount=2 Degree=3 IsPeriodic=0
    g89: BSplineCurve PolesCount=4 KnotsCount=2 Degree=3 IsPeriodic=0
    g90: BSplineCurve PolesCount=4 KnotsCount=2 Degree=3 IsPeriodic=0
    g91: BSplineCurve PolesCount=4 KnotsCount=2 Degree=3 IsPeriodic=0
    g92: BSplineCurve PolesCount=4 KnotsCount=2 Degree=3 IsPeriodic=0
    g93: BSplineCurve PolesCount=4 KnotsCount=2 Degree=3 IsPeriodic=0
    g94: BSplineCurve PolesCount=4 KnotsCount=2 Degree=3 IsPeriodic=0
    g95: BSplineCurve PolesCount=4 KnotsCount=2 Degree=3 IsPeriodic=0
    g96: BSplineCurve PolesCount=4 KnotsCount=2 Degree=3 IsPeriodic=0
    g97: BSplineCurve PolesCount=4 KnotsCount=2 Degree=3 IsPeriodic=0
    g98: BSplineCurve PolesCount=4 KnotsCount=2 Degree=3 IsPeriodic=0
    g99: BSplineCurve PolesCount=4 KnotsCount=2 Degree=3 IsPeriodic=0
    g100: BSplineCurve PolesCount=4 KnotsCount=2 Degree=3 IsPeriodic=0
    g101: BSplineCurve PolesCount=4 KnotsCount=2 Degree=3 IsPeriodic=0
    g102: BSplineCurve PolesCount=4 KnotsCount=2 Degree=3 IsPeriodic=0
    g103: BSplineCurve PolesCount=4 KnotsCount=2 Degree=3 IsPeriodic=0
    g104: BSplineCurve PolesCount=4 KnotsCount=2 Degree=3 IsPeriodic=0
    g105: BSplineCurve PolesCount=2 KnotsCount=2 Degree=1 IsPeriodic=0
    g106: BSplineCurve PolesCount=4 KnotsCount=2 Degree=3 IsPeriodic=0
    g107: BSplineCurve PolesCount=4 KnotsCount=2 Degree=3 IsPeriodic=0
    g108: BSplineCurve PolesCount=4 KnotsCount=2 Degree=3 IsPeriodic=0
    g109: BSplineCurve PolesCount=4 KnotsCount=2 Degree=3 IsPeriodic=0
    g110: BSplineCurve PolesCount=4 KnotsCount=2 Degree=3 IsPeriodic=0
    g111: BSplineCurve PolesCount=4 KnotsCount=2 Degree=3 IsPeriodic=0
    g112: BSplineCurve PolesCount=4 KnotsCount=2 Degree=3 IsPeriodic=0
    g113: BSplineCurve PolesCount=4 KnotsCount=2 Degree=3 IsPeriodic=0
    g114: BSplineCurve PolesCount=4 KnotsCount=2 Degree=3 IsPeriodic=0
    g115: BSplineCurve PolesCount=4 KnotsCount=2 Degree=3 IsPeriodic=0
    g116: BSplineCurve PolesCount=4 KnotsCount=2 Degree=3 IsPeriodic=0
    g117: BSplineCurve PolesCount=4 KnotsCount=2 Degree=3 IsPeriodic=0
    g118: BSplineCurve PolesCount=4 KnotsCount=2 Degree=3 IsPeriodic=0
    g119: BSplineCurve PolesCount=4 KnotsCount=2 Degree=3 IsPeriodic=0
    g120: BSplineCurve PolesCount=4 KnotsCount=2 Degree=3 IsPeriodic=0
    g121: BSplineCurve PolesCount=4 KnotsCount=2 Degree=3 IsPeriodic=0
    g122: BSplineCurve PolesCount=4 KnotsCount=2 Degree=3 IsPeriodic=0
    g123: BSplineCurve PolesCount=4 KnotsCount=2 Degree=3 IsPeriodic=0
    g124: BSplineCurve PolesCount=4 KnotsCount=2 Degree=3 IsPeriodic=0
    g125: BSplineCurve PolesCount=4 KnotsCount=2 Degree=3 IsPeriodic=0
    g126: BSplineCurve PolesCount=4 KnotsCount=2 Degree=3 IsPeriodic=0
    g127: BSplineCurve PolesCount=4 KnotsCount=2 Degree=3 IsPeriodic=0
    g128: BSplineCurve PolesCount=4 KnotsCount=2 Degree=3 IsPeriodic=0
    g129: BSplineCurve PolesCount=4 KnotsCount=2 Degree=3 IsPeriodic=0
    g130: BSplineCurve PolesCount=4 KnotsCount=2 Degree=3 IsPeriodic=0
    g131: BSplineCurve PolesCount=4 KnotsCount=2 Degree=3 IsPeriodic=0
    g132: BSplineCurve PolesCount=4 KnotsCount=2 Degree=3 IsPeriodic=0
    g133: BSplineCurve PolesCount=4 KnotsCount=2 Degree=3 IsPeriodic=0
    g134: BSplineCurve PolesCount=4 KnotsCount=2 Degree=3 IsPeriodic=0
    g135: BSplineCurve PolesCount=4 KnotsCount=2 Degree=3 IsPeriodic=0
    g136: BSplineCurve PolesCount=4 KnotsCount=2 Degree=3 IsPeriodic=0
    g137: BSplineCurve PolesCount=4 KnotsCount=2 Degree=3 IsPeriodic=0
    g138: BSplineCurve PolesCount=4 KnotsCount=2 Degree=3 IsPeriodic=0
    g139: BSplineCurve PolesCount=4 KnotsCount=2 Degree=3 IsPeriodic=0
    g140: BSplineCurve PolesCount=4 KnotsCount=2 Degree=3 IsPeriodic=0
    g141: BSplineCurve PolesCount=4 KnotsCount=2 Degree=3 IsPeriodic=0
    g142: BSplineCurve PolesCount=4 KnotsCount=2 Degree=3 IsPeriodic=0
    g143: BSplineCurve PolesCount=4 KnotsCount=2 Degree=3 IsPeriodic=0
    g144: BSplineCurve PolesCount=4 KnotsCount=2 Degree=3 IsPeriodic=0
    g145: BSplineCurve PolesCount=4 KnotsCount=2 Degree=3 IsPeriodic=0
    g146: BSplineCurve PolesCount=4 KnotsCount=2 Degree=3 IsPeriodic=0
    g147: BSplineCurve PolesCount=4 KnotsCount=2 Degree=3 IsPeriodic=0
    g148: BSplineCurve PolesCount=4 KnotsCount=2 Degree=3 IsPeriodic=0
    g149: BSplineCurve PolesCount=4 KnotsCount=2 Degree=3 IsPeriodic=0
    g150: BSplineCurve PolesCount=4 KnotsCount=2 Degree=3 IsPeriodic=0
    g151: BSplineCurve PolesCount=4 KnotsCount=2 Degree=3 IsPeriodic=0
    g152: BSplineCurve PolesCount=4 KnotsCount=2 Degree=3 IsPeriodic=0
    g153: BSplineCurve PolesCount=4 KnotsCount=2 Degree=3 IsPeriodic=0
    g154: BSplineCurve PolesCount=4 KnotsCount=2 Degree=3 IsPeriodic=0
    g155: BSplineCurve PolesCount=4 KnotsCount=2 Degree=3 IsPeriodic=0
    g156: BSplineCurve PolesCount=4 KnotsCount=2 Degree=3 IsPeriodic=0
    g157: BSplineCurve PolesCount=4 KnotsCount=2 Degree=3 IsPeriodic=0
    g158: BSplineCurve PolesCount=4 KnotsCount=2 Degree=3 IsPeriodic=0
    g159: BSplineCurve PolesCount=4 KnotsCount=2 Degree=3 IsPeriodic=0
  constraints (160):
    c: Coincident(g10,g11)
    c: Coincident(g4,g5)
    c: Coincident(g11,g12)
    c: Coincident(g0,g12)
    c: Coincident(g5,g6)
    c: Coincident(g9,g10)
    c: Coincident(g0,g1)
    c: Coincident(g8,g9)
    c: Coincident(g1,g2)
    c: Coincident(g3,g4)
    c: Coincident(g2,g3)
    c: Coincident(g7,g8)
    c: Coincident(g6,g7)
    c: Coincident(g79,g80)
    c: Coincident(g96,g97)
    c: Coincident(g109,g110)
    c: Coincident(g13,g26)
    c: Coincident(g110,g111)
    c: Coincident(g13,g14)
    c: Coincident(g136,g137)
    c: Coincident(g102,g103)
    c: Coincident(g82,g83)
    c: Coincident(g137,g138)
    c: Coincident(g103,g104)
    c: Coincident(g78,g79)
    c: Coincident(g83,g84)
    c: Coincident(g80,g81)
    c: Coincident(g25,g26)
    c: Coincident(g95,g96)
    c: Coincident(g108,g109)
    c: Coincident(g73,g81)
    c: Coincident(g14,g15)
    c: Coincident(g111,g112)
    c: Coincident(g127,g131)
    c: Coincident(g127,g128)
    c: Coincident(g87,g88)
    c: Coincident(g91,g92)
    c: Coincident(g112,g113)
    c: Coincident(g15,g16)
    c: Coincident(g130,g131)
    c: Coincident(g97,g98)
    c: Coincident(g88,g89)
    c: Coincident(g84,g85)
    c: Coincident(g92,g93)
    c: Coincident(g113,g114)
    c: Coincident(g16,g17)
    c: Coincident(g17,g18)
    c: Coincident(g114,g115)
    c: Coincident(g82,g100)
    c: Coincident(g129,g130)
    c: Coincident(g128,g129)
    c: Coincident(g73,g74)
    c: Coincident(g107,g108)
    c: Coincident(g135,g136)
    c: Coincident(g18,g19)
    c: Coincident(g19,g20)
    c: Coincident(g106,g107)
    c: Coincident(g24,g25)
    c: Coincident(g99,g100)
    c: Coincident(g106,g120)
    c: Coincident(g74,g75)
    c: Coincident(g75,g76)
    c: Coincident(g138,g139)
    c: Coincident(g119,g120)
    c: Coincident(g139,g140)
    c: Coincident(g132,g140)
    c: Coincident(g20,g21)
    c: Coincident(g98,g99)
    c: Coincident(g118,g119)
    c: Coincident(g132,g133)
    c: Coincident(g21,g22)
    c: Coincident(g115,g116)
    c: Coincident(g90,g91)
    c: Coincident(g89,g90)
    c: Coincident(g77,g78)
    c: Coincident(g134,g135)
    c: Coincident(g85,g86)
    c: Coincident(g86,g87)
    c: Coincident(g23,g24)
    c: Coincident(g104,g105)
    c: Coincident(g101,g102)
    c: Coincident(g94,g95)
    c: Coincident(g117,g118)
    c: Coincident(g101,g105)
    c: Coincident(g22,g23)
    c: Coincident(g93,g94)
    c: Coincident(g76,g77)
    c: Coincident(g133,g134)
    c: Coincident(g116,g117)
    c: Coincident(g148,g149)
    c: Coincident(g157,g158)
    c: Coincident(g158,g159)
    c: Coincident(g147,g148)
    c: Coincident(g146,g147)
    c: Coincident(g156,g157)
    c: Coincident(g149,g150)
    c: Coincident(g57,g58)
    c: Coincident(g155,g156)
    c: Coincident(g46,g47)
    c: Coincident(g56,g57)
    c: Coincident(g47,g48)
    c: Coincident(g48,g49)
    c: Coincident(g45,g46)
    c: Coincident(g150,g151)
    c: Coincident(g55,g56)
    c: Coincident(g49,g50)
    c: Coincident(g122,g123)
    c: Coincident(g43,g44)
    c: Coincident(g44,g45)
    c: Coincident(g54,g55)
    c: Coincident(g123,g124)
    c: Coincident(g42,g43)
    c: Coincident(g50,g51)
    c: Coincident(g124,g125)
    c: Coincident(g53,g54)
    c: Coincident(g40,g41)
    c: Coincident(g52,g53)
    c: Coincident(g51,g52)
    c: Coincident(g58,g59)
    c: Coincident(g121,g122)
    c: Coincident(g39,g40)
    c: Coincident(g41,g42)
    c: Coincident(g38,g39)
    c: Coincident(g125,g126)
    c: Coincident(g121,g126)
    c: Coincident(g32,g33)
    c: Coincident(g31,g32)
    c: Coincident(g153,g159)
    c: Coincident(g37,g38)
    c: Coincident(g59,g60)
    c: Coincident(g67,g68)
    c: Coincident(g154,g155)
    c: Coincident(g66,g67)
    c: Coincident(g36,g37)
    c: Coincident(g60,g61)
    c: Coincident(g153,g154)
    c: Coincident(g65,g66)
    c: Coincident(g68,g69)
    c: Coincident(g71,g72)
    c: Coincident(g141,g144)
    c: Coincident(g33,g34)
    c: Coincident(g64,g65)
    c: Coincident(g145,g146)
    c: Coincident(g141,g142)
    c: Coincident(g63,g64)
    c: Coincident(g145,g152)
    c: Coincident(g143,g144)
    c: Coincident(g61,g62)
    c: Coincident(g34,g35)
    c: Coincident(g29,g30)
    c: Coincident(g35,g36)
    c: Coincident(g62,g63)
    c: Coincident(g27,g30)
    c: Coincident(g69,g70)
    c: Coincident(g70,g71)
    c: Coincident(g142,g143)
    c: Coincident(g28,g29)
    c: Coincident(g151,g152)
    c: Coincident(g27,g28)
    c: Coincident(g31,g72)
FEATURE [Part::Part2DObjectPython] Clone2D004  label="MirroredSketch001 (2D)003"  # Draft 2D object (typed FeaturePython)
  AttachmentOffset = pos=(4.3,23,0) rot=(0,0,-1;1.5708rad)
  AttachmentSupport = -> [Pad013]
  ForceCompound = false
  Fuse = false
  MapMode = 5
  Objects = -> [MirroredSketch003]
  Placement = pos=(-4.3,-1.77,23) rot=(-0.57735,0.57735,0.57735;2.0944rad)
  Scale = (0.65,0.65,0.65)
FEATURE [PartDesign::Pocket] Pocket011
  BaseFeature = -> Pad013
  Direction = (0,-1,2e-16)
  Length = 2
  Length2 = 5
  Profile = -> Clone2D004
  ReferenceAxis = -> Clone2D004 [N_Axis]
  Refine = true
  SideType = 0
  Suppressed = false
  Type = 0
  Type2 = 0
FEATURE [Sketcher::SketchObject] Sketch029
  ArcFitTolerance = 1e-06
  AttachmentSupport = -> [Pad013]
  ExternalGeometry = -> [Pad013]
  ExternalTypes = [0,0]
  FullyConstrained = true
  MakeInternals = false
  MapMode = 5
  Placement = pos=(0,0,3) rot=(0,0,1;0rad)
  _ExternalGeoVersion = 0
  sketch-geometry (4):
    g0: LineSegment StartX=-13.5 StartY=-5.575 StartZ=0 EndX=13.5 EndY=-5.575 EndZ=0
    g1: LineSegment StartX=13.5 StartY=-5.575 StartZ=0 EndX=13.5 EndY=-2.575 EndZ=0
    g2: LineSegment StartX=13.5 StartY=-2.575 StartZ=0 EndX=-13.5 EndY=-2.575 EndZ=0
    g3: LineSegment StartX=-13.5 StartY=-2.575 StartZ=0 EndX=-13.5 EndY=-5.575 EndZ=0
  constraints (11):
    c: Coincident(g0,g1)
    c: Coincident(g1,g2)
    c: Coincident(g2,g3)
    c: Coincident(g3,g0)
    c: Horizontal(g2)
    c: Vertical(g1)
    c: Vertical(g3)
    c: DistanceY(g1,g1) = 3
    c: Horizontal(g0)
    c: Coincident(g0,g-3)
    c: PointOnObject(g2,g-4)
FEATURE [PartDesign::AdditiveLoft] AdditiveLoft006
  BaseFeature = -> Pocket011
  Closed = false
  Profile = -> Sketch029
  Refine = true
  Ruled = false
  Sections = -> [Pocket011]
  Suppressed = false
FEATURE [PartDesign::Chamfer] Chamfer004
  Angle = 45
  Base = -> AdditiveLoft006 [Edge468,Edge489]
  BaseFeature = -> AdditiveLoft006
  ChamferType = 0
  FlipDirection = false
  Refine = true
  Size = 2
  Size2 = 1
  SupportTransform = false
  Suppressed = false
  UseAllEdges = false
FEATURE [Sketcher::SketchObject] Sketch030
  ArcFitTolerance = 1e-06
  AttachmentSupport = -> [Chamfer004]
  ExternalGeometry = -> [Chamfer004]
  ExternalTypes = [0,0]
  FullyConstrained = true
  MakeInternals = false
  MapMode = 5
  Placement = pos=(0,0,43.3) rot=(0,0,1;0rad)
  _ExternalGeoVersion = 0
  sketch-geometry (2):
    g0: Circle CenterX=-31.8 CenterY=-2.27 CenterZ=0 NormalX=0 NormalY=0 NormalZ=1 AngleXU=0 Radius=1.5
    g1: Circle CenterX=-0.2 CenterY=-2.27 CenterZ=0 NormalX=0 NormalY=0 NormalZ=1 AngleXU=0 Radius=1.5
  constraints (4):
    c: Coincident(g0,g-4)
    c: Coincident(g1,g-3)
    c: Equal(g1,g0)
    c: Diameter(g0) = 3
FEATURE [PartDesign::Pocket] Pocket012
  BaseFeature = -> Chamfer004
  Direction = (0,0,-1)
  Length = 11
  Length2 = 5
  Profile = -> Sketch030
  ReferenceAxis = -> Sketch030 [N_Axis]
  Refine = true
  SideType = 0
  Suppressed = false
  Type = 0
  Type2 = 0
FEATURE [PartDesign::Chamfer] Chamfer005
  Angle = 45
  Base = -> Pocket012 [Edge194,Edge193]
  BaseFeature = -> Pocket012
  ChamferType = 0
  FlipDirection = false
  Refine = true
  Size = 1
  Size2 = 1
  SupportTransform = false
  Suppressed = false
  UseAllEdges = false
FEATURE [Sketcher::SketchObject] Sketch031
  ArcFitTolerance = 1e-06
  AttachmentSupport = -> [Chamfer005]
  ExternalGeometry = -> [Chamfer005]
  ExternalTypes = [0,0]
  FullyConstrained = true
  MakeInternals = false
  MapMode = 5
  Placement = pos=(0,0,3) rot=(0,0,1;0rad)
  _ExternalGeoVersion = 0
  sketch-geometry (4):
    g0: LineSegment StartX=-5 StartY=-2.575 StartZ=0 EndX=5 EndY=-2.575 EndZ=0
    g1: LineSegment StartX=5 StartY=-2.575 StartZ=0 EndX=5 EndY=5.575 EndZ=0
    g2: LineSegment StartX=5 StartY=5.575 StartZ=0 EndX=-5 EndY=5.575 EndZ=0
    g3: LineSegment StartX=-5 StartY=5.575 StartZ=0 EndX=-5 EndY=-2.575 EndZ=0
  constraints (11):
    c: Coincident(g0,g1)
    c: Coincident(g1,g2)
    c: Coincident(g2,g3)
    c: Coincident(g3,g0)
    c: Horizontal(g0)
    c: Vertical(g1)
    c: Vertical(g3)
    c: PointOnObject(g0,g-3)
    c: PointOnObject(g1,g-4)
    c: DistanceX(g2,g2) = 10
    c: Symmetric(g1,g2,g-2)
FEATURE [Sketcher::SketchObject] Sketch032
  ArcFitTolerance = 1e-06
  AttachmentSupport = -> [Chamfer005]
  ExternalGeometry = -> [Chamfer005]
  ExternalTypes = [0]
  FullyConstrained = true
  MakeInternals = false
  MapMode = 5
  Placement = pos=(1e-16,-2.70174,0.118847) rot=(0,0.722477,0.691395;3.14159rad)
  _ExternalGeoVersion = 0
  sketch-geometry (4):
    g0: LineSegment StartX=-5.5 StartY=10.9839 StartZ=0 EndX=-5.5 EndY=10.8839 EndZ=0
    g1: LineSegment StartX=-5.5 StartY=10.8839 StartZ=0 EndX=4.5 EndY=10.8839 EndZ=0
    g2: LineSegment StartX=4.5 StartY=10.8839 StartZ=0 EndX=4.5 EndY=10.9839 EndZ=0
    g3: LineSegment StartX=4.5 StartY=10.9839 StartZ=0 EndX=-5.5 EndY=10.9839 EndZ=0
  constraints (12):
    c: Coincident(g0,g1)
    c: Coincident(g1,g2)
    c: Coincident(g2,g3)
    c: Coincident(g3,g0)
    c: Vertical(g0)
    c: Vertical(g2)
    c: Horizontal(g1)
    c: Horizontal(g3)
    c: DistanceX(g3,g3) = 10
    c: DistanceY(g2,g2) = 0.1
    c: DistanceY(g-3,g0) = 8
    c: DistanceX(g-3,g0) = 8
FEATURE [PartDesign::AdditiveLoft] AdditiveLoft007
  BaseFeature = -> Chamfer005
  Closed = false
  Profile = -> Sketch031
  Refine = true
  Ruled = false
  Sections = -> [Sketch032]
  Suppressed = false
FEATURE [Sketcher::SketchObject] Sketch026
  ArcFitTolerance = 1e-06
  AttachmentSupport = -> [AdditiveLoft007]
  ExternalGeometry = -> [AdditiveLoft007]
  ExternalTypes = [0,0]
  FullyConstrained = false
  MakeInternals = false
  MapMode = 5
  Placement = pos=(0,-6.27,0) rot=(1,0,0;1.5708rad)
  _ExternalGeoVersion = 0
  sketch-geometry (374):
    g0: LineSegment [constr] StartX=-3.2 StartY=42.193 StartZ=0 EndX=-28.8 EndY=42.193 EndZ=0
    g1: LineSegment StartX=-4.02709 StartY=42.1612 StartZ=0 EndX=-3.2 EndY=42.1612 EndZ=0
    g2: LineSegment StartX=-3.2 StartY=42.1612 StartZ=0 EndX=-3.2 EndY=39.2385 EndZ=0
    g3: LineSegment StartX=-3.2 StartY=39.2385 StartZ=0 EndX=-4.02709 EndY=39.2385 EndZ=0
    g4: BSplineCurve PolesCount=3 KnotsCount=2 Degree=2 IsPeriodic=0
    g5: BSplineCurve PolesCount=3 KnotsCount=2 Degree=2 IsPeriodic=0
    g6: BSplineCurve PolesCount=3 KnotsCount=2 Degree=2 IsPeriodic=0
    g7: BSplineCurve PolesCount=3 KnotsCount=2 Degree=2 IsPeriodic=0
    g8: BSplineCurve PolesCount=3 KnotsCount=2 Degree=2 IsPeriodic=0
    g9: BSplineCurve PolesCount=3 KnotsCount=2 Degree=2 IsPeriodic=0
    g10: BSplineCurve PolesCount=3 KnotsCount=2 Degree=2 IsPeriodic=0
    g11: BSplineCurve PolesCount=3 KnotsCount=2 Degree=2 IsPeriodic=0
    g12: BSplineCurve PolesCount=3 KnotsCount=2 Degree=2 IsPeriodic=0
    g13: BSplineCurve PolesCount=3 KnotsCount=2 Degree=2 IsPeriodic=0
    g14: BSplineCurve PolesCount=3 KnotsCount=2 Degree=2 IsPeriodic=0
    g15: BSplineCurve PolesCount=3 KnotsCount=2 Degree=2 IsPeriodic=0
    g16: BSplineCurve PolesCount=3 KnotsCount=2 Degree=2 IsPeriodic=0
    g17: BSplineCurve PolesCount=3 KnotsCount=2 Degree=2 IsPeriodic=0
    g18: BSplineCurve PolesCount=3 KnotsCount=2 Degree=2 IsPeriodic=0
    g19: BSplineCurve PolesCount=3 KnotsCount=2 Degree=2 IsPeriodic=0
    g20: BSplineCurve PolesCount=3 KnotsCount=2 Degree=2 IsPeriodic=0
    g21: BSplineCurve PolesCount=3 KnotsCount=2 Degree=2 IsPeriodic=0
    g22: BSplineCurve PolesCount=3 KnotsCount=2 Degree=2 IsPeriodic=0
    g23: BSplineCurve PolesCount=3 KnotsCount=2 Degree=2 IsPeriodic=0
    g24: LineSegment StartX=-3.67319 StartY=40.4474 StartZ=0 EndX=-4.02709 EndY=40.4474 EndZ=0
    g25: BSplineCurve PolesCount=3 KnotsCount=2 Degree=2 IsPeriodic=0
    g26: BSplineCurve PolesCount=3 KnotsCount=2 Degree=2 IsPeriodic=0
    g27: BSplineCurve PolesCount=3 KnotsCount=2 Degree=2 IsPeriodic=0
    g28: BSplineCurve PolesCount=3 KnotsCount=2 Degree=2 IsPeriodic=0
    g29: BSplineCurve PolesCount=3 KnotsCount=2 Degree=2 IsPeriodic=0
    g30: BSplineCurve PolesCount=3 KnotsCount=2 Degree=2 IsPeriodic=0
    g31: BSplineCurve PolesCount=3 KnotsCount=2 Degree=2 IsPeriodic=0
    g32: BSplineCurve PolesCount=3 KnotsCount=2 Degree=2 IsPeriodic=0
    g33: LineSegment StartX=-4.02709 StartY=39.6402 StartZ=0 EndX=-3.67319 EndY=39.6402 EndZ=0
    g34: LineSegment StartX=-3.67319 StartY=39.6402 StartZ=0 EndX=-3.67319 EndY=40.4474 EndZ=0
    g35: LineSegment StartX=-3.67319 StartY=41.7596 StartZ=0 EndX=-4.02709 EndY=41.7596 EndZ=0
    g36: BSplineCurve PolesCount=3 KnotsCount=2 Degree=2 IsPeriodic=0
    g37: BSplineCurve PolesCount=3 KnotsCount=2 Degree=2 IsPeriodic=0
    g38: BSplineCurve PolesCount=3 KnotsCount=2 Degree=2 IsPeriodic=0
    g39: BSplineCurve PolesCount=3 KnotsCount=2 Degree=2 IsPeriodic=0
    g40: BSplineCurve PolesCount=3 KnotsCount=2 Degree=2 IsPeriodic=0
    g41: BSplineCurve PolesCount=3 KnotsCount=2 Degree=2 IsPeriodic=0
    g42: BSplineCurve PolesCount=3 KnotsCount=2 Degree=2 IsPeriodic=0
    g43: BSplineCurve PolesCount=3 KnotsCount=2 Degree=2 IsPeriodic=0
    g44: BSplineCurve PolesCount=3 KnotsCount=2 Degree=2 IsPeriodic=0
    g45: BSplineCurve PolesCount=3 KnotsCount=2 Degree=2 IsPeriodic=0
    g46: BSplineCurve PolesCount=3 KnotsCount=2 Degree=2 IsPeriodic=0
    g47: BSplineCurve PolesCount=3 KnotsCount=2 Degree=2 IsPeriodic=0
    g48: LineSegment StartX=-4.02709 StartY=40.849 StartZ=0 EndX=-3.67319 EndY=40.849 EndZ=0
    g49: LineSegment StartX=-3.67319 StartY=40.849 StartZ=0 EndX=-3.67319 EndY=41.7596 EndZ=0
    g50: BSplineCurve PolesCount=3 KnotsCount=2 Degree=2 IsPeriodic=0
    g51: BSplineCurve PolesCount=3 KnotsCount=2 Degree=2 IsPeriodic=0
    g52: BSplineCurve PolesCount=3 KnotsCount=2 Degree=2 IsPeriodic=0
    g53: BSplineCurve PolesCount=3 KnotsCount=2 Degree=2 IsPeriodic=0
    g54: BSplineCurve PolesCount=3 KnotsCount=2 Degree=2 IsPeriodic=0
    g55: BSplineCurve PolesCount=3 KnotsCount=2 Degree=2 IsPeriodic=0
    g56: LineSegment StartX=-5.55402 StartY=41.3262 StartZ=0 EndX=-5.55402 EndY=40.9285 EndZ=0
    g57: BSplineCurve PolesCount=3 KnotsCount=2 Degree=2 IsPeriodic=0
    g58: BSplineCurve PolesCount=3 KnotsCount=2 Degree=2 IsPeriodic=0
    g59: BSplineCurve PolesCount=3 KnotsCount=2 Degree=2 IsPeriodic=0
    g60: BSplineCurve PolesCount=3 KnotsCount=2 Degree=2 IsPeriodic=0
    g61: BSplineCurve PolesCount=3 KnotsCount=2 Degree=2 IsPeriodic=0
    g62: BSplineCurve PolesCount=3 KnotsCount=2 Degree=2 IsPeriodic=0
    g63: BSplineCurve PolesCount=3 KnotsCount=2 Degree=2 IsPeriodic=0
    g64: BSplineCurve PolesCount=3 KnotsCount=2 Degree=2 IsPeriodic=0
    g65: BSplineCurve PolesCount=3 KnotsCount=2 Degree=2 IsPeriodic=0
    g66: BSplineCurve PolesCount=3 KnotsCount=2 Degree=2 IsPeriodic=0
    g67: BSplineCurve PolesCount=3 KnotsCount=2 Degree=2 IsPeriodic=0
    g68: BSplineCurve PolesCount=3 KnotsCount=2 Degree=2 IsPeriodic=0
    g69: LineSegment StartX=-7.3593 StartY=40.9285 StartZ=0 EndX=-7.3593 EndY=41.3262 EndZ=0
    g70: LineSegment StartX=-7.3593 StartY=41.3262 StartZ=0 EndX=-6.01926 EndY=41.3262 EndZ=0
    g71: BSplineCurve PolesCount=3 KnotsCount=2 Degree=2 IsPeriodic=0
    g72: BSplineCurve PolesCount=3 KnotsCount=2 Degree=2 IsPeriodic=0
    g73: BSplineCurve PolesCount=3 KnotsCount=2 Degree=2 IsPeriodic=0
    g74: BSplineCurve PolesCount=3 KnotsCount=2 Degree=2 IsPeriodic=0
    g75: BSplineCurve PolesCount=3 KnotsCount=2 Degree=2 IsPeriodic=0
    g76: BSplineCurve PolesCount=3 KnotsCount=2 Degree=2 IsPeriodic=0
    g77: BSplineCurve PolesCount=3 KnotsCount=2 Degree=2 IsPeriodic=0
    g78: BSplineCurve PolesCount=3 KnotsCount=2 Degree=2 IsPeriodic=0
    g79: LineSegment StartX=-6.88611 StartY=41.5488 StartZ=0 EndX=-7.35135 EndY=41.5488 EndZ=0
    g80: BSplineCurve PolesCount=3 KnotsCount=2 Degree=2 IsPeriodic=0
    g81: BSplineCurve PolesCount=3 KnotsCount=2 Degree=2 IsPeriodic=0
    g82: BSplineCurve PolesCount=3 KnotsCount=2 Degree=2 IsPeriodic=0
    g83: BSplineCurve PolesCount=3 KnotsCount=2 Degree=2 IsPeriodic=0
    g84: BSplineCurve PolesCount=3 KnotsCount=2 Degree=2 IsPeriodic=0
    g85: BSplineCurve PolesCount=3 KnotsCount=2 Degree=2 IsPeriodic=0
    g86: LineSegment StartX=-6.01926 StartY=40.9285 StartZ=0 EndX=-6.89407 EndY=40.9285 EndZ=0
    g87: BSplineCurve PolesCount=3 KnotsCount=2 Degree=2 IsPeriodic=0
    g88: BSplineCurve PolesCount=3 KnotsCount=2 Degree=2 IsPeriodic=0
    g89: BSplineCurve PolesCount=3 KnotsCount=2 Degree=2 IsPeriodic=0
    g90: BSplineCurve PolesCount=3 KnotsCount=2 Degree=2 IsPeriodic=0
    g91: BSplineCurve PolesCount=3 KnotsCount=2 Degree=2 IsPeriodic=0
    g92: BSplineCurve PolesCount=3 KnotsCount=2 Degree=2 IsPeriodic=0
    g93: BSplineCurve PolesCount=3 KnotsCount=2 Degree=2 IsPeriodic=0
    g94: BSplineCurve PolesCount=3 KnotsCount=2 Degree=2 IsPeriodic=0
    g95: BSplineCurve PolesCount=3 KnotsCount=2 Degree=2 IsPeriodic=0
    g96: BSplineCurve PolesCount=3 KnotsCount=2 Degree=2 IsPeriodic=0
    g97: BSplineCurve PolesCount=3 KnotsCount=2 Degree=2 IsPeriodic=0
    g98: BSplineCurve PolesCount=3 KnotsCount=2 Degree=2 IsPeriodic=0
    g99: BSplineCurve PolesCount=3 KnotsCount=2 Degree=2 IsPeriodic=0
    g100: BSplineCurve PolesCount=3 KnotsCount=2 Degree=2 IsPeriodic=0
    g101: BSplineCurve PolesCount=3 KnotsCount=2 Degree=2 IsPeriodic=0
    g102: BSplineCurve PolesCount=3 KnotsCount=2 Degree=2 IsPeriodic=0
    g103: BSplineCurve PolesCount=3 KnotsCount=2 Degree=2 IsPeriodic=0
    g104: BSplineCurve PolesCount=3 KnotsCount=2 Degree=2 IsPeriodic=0
    g105: BSplineCurve PolesCount=3 KnotsCount=2 Degree=2 IsPeriodic=0
    g106: BSplineCurve PolesCount=3 KnotsCount=2 Degree=2 IsPeriodic=0
    g107: LineSegment StartX=-8.92998 StartY=40.8967 StartZ=0 EndX=-9.24809 EndY=40.8967 EndZ=0
    g108: LineSegment StartX=-9.24809 StartY=40.8967 StartZ=0 EndX=-9.24809 EndY=40.7933 EndZ=0
    g109: BSplineCurve PolesCount=3 KnotsCount=2 Degree=2 IsPeriodic=0
    g110: BSplineCurve PolesCount=3 KnotsCount=2 Degree=2 IsPeriodic=0
    g111: BSplineCurve PolesCount=3 KnotsCount=2 Degree=2 IsPeriodic=0
    g112: BSplineCurve PolesCount=3 KnotsCount=2 Degree=2 IsPeriodic=0
    g113: BSplineCurve PolesCount=3 KnotsCount=2 Degree=2 IsPeriodic=0
    g114: BSplineCurve PolesCount=3 KnotsCount=2 Degree=2 IsPeriodic=0
    g115: BSplineCurve PolesCount=3 KnotsCount=2 Degree=2 IsPeriodic=0
    g116: BSplineCurve PolesCount=3 KnotsCount=2 Degree=2 IsPeriodic=0
    g117: LineSegment StartX=-8.42895 StartY=40.7019 StartZ=0 EndX=-8.42895 EndY=40.7058 EndZ=0
    g118: LineSegment StartX=-8.42895 StartY=40.7058 StartZ=0 EndX=-7.96372 EndY=40.7058 EndZ=0
    g119: LineSegment StartX=-7.96372 StartY=40.7058 StartZ=0 EndX=-7.96372 EndY=40.6939 EndZ=0
    g120: BSplineCurve PolesCount=3 KnotsCount=2 Degree=2 IsPeriodic=0
    g121: BSplineCurve PolesCount=3 KnotsCount=2 Degree=2 IsPeriodic=0
    g122: BSplineCurve PolesCount=3 KnotsCount=2 Degree=2 IsPeriodic=0
    g123: BSplineCurve PolesCount=3 KnotsCount=2 Degree=2 IsPeriodic=0
    g124: BSplineCurve PolesCount=3 KnotsCount=2 Degree=2 IsPeriodic=0
    g125: BSplineCurve PolesCount=3 KnotsCount=2 Degree=2 IsPeriodic=0
    g126: BSplineCurve PolesCount=3 KnotsCount=2 Degree=2 IsPeriodic=0
    g127: BSplineCurve PolesCount=3 KnotsCount=2 Degree=2 IsPeriodic=0
    g128: BSplineCurve PolesCount=3 KnotsCount=2 Degree=2 IsPeriodic=0
    g129: BSplineCurve PolesCount=3 KnotsCount=2 Degree=2 IsPeriodic=0
    g130: BSplineCurve PolesCount=3 KnotsCount=2 Degree=2 IsPeriodic=0
    g131: BSplineCurve PolesCount=3 KnotsCount=2 Degree=2 IsPeriodic=0
    g132: LineSegment StartX=-9.71333 StartY=40.7933 StartZ=0 EndX=-9.71333 EndY=42.1612 EndZ=0
    g133: LineSegment StartX=-9.71333 StartY=42.1612 StartZ=0 EndX=-9.24809 EndY=42.1612 EndZ=0
    g134: LineSegment StartX=-9.24809 StartY=42.1612 StartZ=0 EndX=-9.24809 EndY=41.8153 EndZ=0
    g135: BSplineCurve PolesCount=3 KnotsCount=2 Degree=2 IsPeriodic=0
    g136: BSplineCurve PolesCount=3 KnotsCount=2 Degree=2 IsPeriodic=0
    g137: BSplineCurve PolesCount=3 KnotsCount=2 Degree=2 IsPeriodic=0
    g138: BSplineCurve PolesCount=3 KnotsCount=2 Degree=2 IsPeriodic=0
    g139: BSplineCurve PolesCount=3 KnotsCount=2 Degree=2 IsPeriodic=0
    g140: BSplineCurve PolesCount=3 KnotsCount=2 Degree=2 IsPeriodic=0
    g141: BSplineCurve PolesCount=3 KnotsCount=2 Degree=2 IsPeriodic=0
    g142: BSplineCurve PolesCount=3 KnotsCount=2 Degree=2 IsPeriodic=0
    g143: LineSegment StartX=-9.24809 StartY=41.4097 StartZ=0 EndX=-9.24809 EndY=41.2904 EndZ=0
    g144: LineSegment StartX=-9.24809 StartY=41.2904 StartZ=0 EndX=-8.92998 EndY=41.2904 EndZ=0
    g145: BSplineCurve PolesCount=3 KnotsCount=2 Degree=2 IsPeriodic=0
    g146: BSplineCurve PolesCount=3 KnotsCount=2 Degree=2 IsPeriodic=0
    g147: BSplineCurve PolesCount=3 KnotsCount=2 Degree=2 IsPeriodic=0
    g148: BSplineCurve PolesCount=3 KnotsCount=2 Degree=2 IsPeriodic=0
    g149: BSplineCurve PolesCount=3 KnotsCount=2 Degree=2 IsPeriodic=0
    g150: BSplineCurve PolesCount=3 KnotsCount=2 Degree=2 IsPeriodic=0
    g151: BSplineCurve PolesCount=3 KnotsCount=2 Degree=2 IsPeriodic=0
    g152: BSplineCurve PolesCount=3 KnotsCount=2 Degree=2 IsPeriodic=0
    g153: BSplineCurve PolesCount=3 KnotsCount=2 Degree=2 IsPeriodic=0
    g154: BSplineCurve PolesCount=3 KnotsCount=2 Degree=2 IsPeriodic=0
    g155: BSplineCurve PolesCount=3 KnotsCount=2 Degree=2 IsPeriodic=0
    g156: BSplineCurve PolesCount=3 KnotsCount=2 Degree=2 IsPeriodic=0
    g157: BSplineCurve PolesCount=3 KnotsCount=2 Degree=2 IsPeriodic=0
    g158: BSplineCurve PolesCount=3 KnotsCount=2 Degree=2 IsPeriodic=0
    g159: BSplineCurve PolesCount=3 KnotsCount=2 Degree=2 IsPeriodic=0
    g160: BSplineCurve PolesCount=3 KnotsCount=2 Degree=2 IsPeriodic=0
    g161: LineSegment StartX=-10.3257 StartY=41.3262 StartZ=0 EndX=-10.3257 EndY=40.9285 EndZ=0
    g162: BSplineCurve PolesCount=3 KnotsCount=2 Degree=2 IsPeriodic=0
    g163: BSplineCurve PolesCount=3 KnotsCount=2 Degree=2 IsPeriodic=0
    g164: BSplineCurve PolesCount=3 KnotsCount=2 Degree=2 IsPeriodic=0
    g165: BSplineCurve PolesCount=3 KnotsCount=2 Degree=2 IsPeriodic=0
    g166: BSplineCurve PolesCount=3 KnotsCount=2 Degree=2 IsPeriodic=0
    g167: BSplineCurve PolesCount=3 KnotsCount=2 Degree=2 IsPeriodic=0
    g168: BSplineCurve PolesCount=3 KnotsCount=2 Degree=2 IsPeriodic=0
    g169: BSplineCurve PolesCount=3 KnotsCount=2 Degree=2 IsPeriodic=0
    g170: BSplineCurve PolesCount=3 KnotsCount=2 Degree=2 IsPeriodic=0
    g171: BSplineCurve PolesCount=3 KnotsCount=2 Degree=2 IsPeriodic=0
    g172: BSplineCurve PolesCount=3 KnotsCount=2 Degree=2 IsPeriodic=0
    g173: BSplineCurve PolesCount=3 KnotsCount=2 Degree=2 IsPeriodic=0
    g174: LineSegment StartX=-12.1071 StartY=40.8251 StartZ=0 EndX=-12.1071 EndY=40.845 EndZ=0
    g175: LineSegment StartX=-12.1071 StartY=40.845 StartZ=0 EndX=-11.6339 EndY=40.845 EndZ=0
    g176: LineSegment StartX=-11.6339 StartY=40.845 StartZ=0 EndX=-11.6339 EndY=40.8371 EndZ=0
    g177: BSplineCurve PolesCount=3 KnotsCount=2 Degree=2 IsPeriodic=0
    g178: BSplineCurve PolesCount=3 KnotsCount=2 Degree=2 IsPeriodic=0
    g179: BSplineCurve PolesCount=3 KnotsCount=2 Degree=2 IsPeriodic=0
    g180: BSplineCurve PolesCount=3 KnotsCount=2 Degree=2 IsPeriodic=0
    g181: BSplineCurve PolesCount=3 KnotsCount=2 Degree=2 IsPeriodic=0
    g182: BSplineCurve PolesCount=3 KnotsCount=2 Degree=2 IsPeriodic=0
    g183: BSplineCurve PolesCount=3 KnotsCount=2 Degree=2 IsPeriodic=0
    g184: BSplineCurve PolesCount=3 KnotsCount=2 Degree=2 IsPeriodic=0
    g185: LineSegment StartX=-10.7989 StartY=40.9285 StartZ=0 EndX=-10.7989 EndY=41.3262 EndZ=0
    g186: BSplineCurve PolesCount=3 KnotsCount=2 Degree=2 IsPeriodic=0
    g187: BSplineCurve PolesCount=3 KnotsCount=2 Degree=2 IsPeriodic=0
    g188: BSplineCurve PolesCount=3 KnotsCount=2 Degree=2 IsPeriodic=0
    g189: BSplineCurve PolesCount=3 KnotsCount=2 Degree=2 IsPeriodic=0
    g190: BSplineCurve PolesCount=3 KnotsCount=2 Degree=2 IsPeriodic=0
    g191: BSplineCurve PolesCount=3 KnotsCount=2 Degree=2 IsPeriodic=0
    g192: BSplineCurve PolesCount=3 KnotsCount=2 Degree=2 IsPeriodic=0
    g193: BSplineCurve PolesCount=3 KnotsCount=2 Degree=2 IsPeriodic=0
    g194: LineSegment StartX=-11.6339 StartY=41.4176 StartZ=0 EndX=-11.6339 EndY=41.4097 EndZ=0
    g195: LineSegment StartX=-11.6339 StartY=41.4097 StartZ=0 EndX=-12.1071 EndY=41.4097 EndZ=0
    g196: LineSegment StartX=-12.1071 StartY=41.4097 StartZ=0 EndX=-12.1071 EndY=41.4295 EndZ=0
    g197: BSplineCurve PolesCount=3 KnotsCount=2 Degree=2 IsPeriodic=0
    g198: BSplineCurve PolesCount=3 KnotsCount=2 Degree=2 IsPeriodic=0
    g199: BSplineCurve PolesCount=3 KnotsCount=2 Degree=2 IsPeriodic=0
    g200: BSplineCurve PolesCount=3 KnotsCount=2 Degree=2 IsPeriodic=0
    g201: BSplineCurve PolesCount=3 KnotsCount=2 Degree=2 IsPeriodic=0
    g202: BSplineCurve PolesCount=3 KnotsCount=2 Degree=2 IsPeriodic=0
    g203: BSplineCurve PolesCount=3 KnotsCount=2 Degree=2 IsPeriodic=0
    g204: BSplineCurve PolesCount=3 KnotsCount=2 Degree=2 IsPeriodic=0
    g205: BSplineCurve PolesCount=3 KnotsCount=2 Degree=2 IsPeriodic=0
    g206: BSplineCurve PolesCount=3 KnotsCount=2 Degree=2 IsPeriodic=0
    g207: BSplineCurve PolesCount=3 KnotsCount=2 Degree=2 IsPeriodic=0
    g208: BSplineCurve PolesCount=3 KnotsCount=2 Degree=2 IsPeriodic=0
    g209: LineSegment StartX=-12.7115 StartY=41.3262 StartZ=0 EndX=-12.7115 EndY=40.9285 EndZ=0
    g210: BSplineCurve PolesCount=3 KnotsCount=2 Degree=2 IsPeriodic=0
    g211: BSplineCurve PolesCount=3 KnotsCount=2 Degree=2 IsPeriodic=0
    g212: BSplineCurve PolesCount=3 KnotsCount=2 Degree=2 IsPeriodic=0
    g213: BSplineCurve PolesCount=3 KnotsCount=2 Degree=2 IsPeriodic=0
    g214: BSplineCurve PolesCount=3 KnotsCount=2 Degree=2 IsPeriodic=0
    g215: BSplineCurve PolesCount=3 KnotsCount=2 Degree=2 IsPeriodic=0
    g216: BSplineCurve PolesCount=3 KnotsCount=2 Degree=2 IsPeriodic=0
    g217: BSplineCurve PolesCount=3 KnotsCount=2 Degree=2 IsPeriodic=0
    g218: BSplineCurve PolesCount=3 KnotsCount=2 Degree=2 IsPeriodic=0
    g219: BSplineCurve PolesCount=3 KnotsCount=2 Degree=2 IsPeriodic=0
    g220: BSplineCurve PolesCount=3 KnotsCount=2 Degree=2 IsPeriodic=0
    g221: BSplineCurve PolesCount=3 KnotsCount=2 Degree=2 IsPeriodic=0
    g222: LineSegment StartX=-14.5168 StartY=40.9285 StartZ=0 EndX=-14.5168 EndY=41.3262 EndZ=0
    g223: BSplineCurve PolesCount=3 KnotsCount=2 Degree=2 IsPeriodic=0
    g224: BSplineCurve PolesCount=3 KnotsCount=2 Degree=2 IsPeriodic=0
    g225: BSplineCurve PolesCount=3 KnotsCount=2 Degree=2 IsPeriodic=0
    g226: BSplineCurve PolesCount=3 KnotsCount=2 Degree=2 IsPeriodic=0
    g227: BSplineCurve PolesCount=3 KnotsCount=2 Degree=2 IsPeriodic=0
    g228: BSplineCurve PolesCount=3 KnotsCount=2 Degree=2 IsPeriodic=0
    g229: BSplineCurve PolesCount=3 KnotsCount=2 Degree=2 IsPeriodic=0
    g230: BSplineCurve PolesCount=3 KnotsCount=2 Degree=2 IsPeriodic=0
    g231: BSplineCurve PolesCount=3 KnotsCount=2 Degree=2 IsPeriodic=0
    g232: BSplineCurve PolesCount=3 KnotsCount=2 Degree=2 IsPeriodic=0
    g233: LineSegment StartX=-14.0436 StartY=41.3262 StartZ=0 EndX=-14.0436 EndY=40.9285 EndZ=0
    g234: BSplineCurve PolesCount=3 KnotsCount=2 Degree=2 IsPeriodic=0
    g235: BSplineCurve PolesCount=3 KnotsCount=2 Degree=2 IsPeriodic=0
    g236: BSplineCurve PolesCount=3 KnotsCount=2 Degree=2 IsPeriodic=0
    g237: BSplineCurve PolesCount=3 KnotsCount=2 Degree=2 IsPeriodic=0
    g238: BSplineCurve PolesCount=3 KnotsCount=2 Degree=2 IsPeriodic=0
    g239: BSplineCurve PolesCount=3 KnotsCount=2 Degree=2 IsPeriodic=0
    g240: BSplineCurve PolesCount=3 KnotsCount=2 Degree=2 IsPeriodic=0
    g241: BSplineCurve PolesCount=3 KnotsCount=2 Degree=2 IsPeriodic=0
    g242: LineSegment StartX=-13.1847 StartY=40.9285 StartZ=0 EndX=-13.1847 EndY=41.3262 EndZ=0
    g243: BSplineCurve PolesCount=3 KnotsCount=2 Degree=2 IsPeriodic=0
    g244: BSplineCurve PolesCount=3 KnotsCount=2 Degree=2 IsPeriodic=0
    g245: BSplineCurve PolesCount=3 KnotsCount=2 Degree=2 IsPeriodic=0
    g246: BSplineCurve PolesCount=3 KnotsCount=2 Degree=2 IsPeriodic=0
    g247: LineSegment StartX=-15.1292 StartY=42.1612 StartZ=0 EndX=-15.1292 EndY=40.0935 EndZ=0
    g248: LineSegment StartX=-15.1292 StartY=40.0935 StartZ=0 EndX=-15.6024 EndY=40.0935 EndZ=0
    g249: LineSegment StartX=-15.6024 StartY=40.0935 StartZ=0 EndX=-15.6024 EndY=40.4752 EndZ=0
    g250: BSplineCurve PolesCount=3 KnotsCount=2 Degree=2 IsPeriodic=0
    g251: BSplineCurve PolesCount=3 KnotsCount=2 Degree=2 IsPeriodic=0
    g252: BSplineCurve PolesCount=3 KnotsCount=2 Degree=2 IsPeriodic=0
    g253: BSplineCurve PolesCount=3 KnotsCount=2 Degree=2 IsPeriodic=0
    g254: BSplineCurve PolesCount=3 KnotsCount=2 Degree=2 IsPeriodic=0
    g255: BSplineCurve PolesCount=3 KnotsCount=2 Degree=2 IsPeriodic=0
    g256: BSplineCurve PolesCount=3 KnotsCount=2 Degree=2 IsPeriodic=0
    g257: BSplineCurve PolesCount=3 KnotsCount=2 Degree=2 IsPeriodic=0
    g258: BSplineCurve PolesCount=3 KnotsCount=2 Degree=2 IsPeriodic=0
    g259: BSplineCurve PolesCount=3 KnotsCount=2 Degree=2 IsPeriodic=0
    g260: LineSegment StartX=-16.8708 StartY=40.9285 StartZ=0 EndX=-16.8708 EndY=42.1612 EndZ=0
    g261: LineSegment StartX=-16.8708 StartY=42.1612 StartZ=0 EndX=-16.3976 EndY=42.1612 EndZ=0
    g262: LineSegment StartX=-16.3976 StartY=42.1612 StartZ=0 EndX=-16.3976 EndY=40.9285 EndZ=0
    g263: BSplineCurve PolesCount=3 KnotsCount=2 Degree=2 IsPeriodic=0
    g264: BSplineCurve PolesCount=3 KnotsCount=2 Degree=2 IsPeriodic=0
    g265: BSplineCurve PolesCount=3 KnotsCount=2 Degree=2 IsPeriodic=0
    g266: BSplineCurve PolesCount=3 KnotsCount=2 Degree=2 IsPeriodic=0
    g267: BSplineCurve PolesCount=3 KnotsCount=2 Degree=2 IsPeriodic=0
    g268: BSplineCurve PolesCount=3 KnotsCount=2 Degree=2 IsPeriodic=0
    g269: BSplineCurve PolesCount=3 KnotsCount=2 Degree=2 IsPeriodic=0
    g270: BSplineCurve PolesCount=3 KnotsCount=2 Degree=2 IsPeriodic=0
    g271: LineSegment StartX=-15.6024 StartY=40.9285 StartZ=0 EndX=-15.6024 EndY=42.1612 EndZ=0
    g272: LineSegment StartX=-15.6024 StartY=42.1612 StartZ=0 EndX=-15.1292 EndY=42.1612 EndZ=0
    g273: LineSegment StartX=-21.225 StartY=42.1612 StartZ=0 EndX=-20.6404 EndY=41.0319 EndZ=0
    g274: LineSegment StartX=-20.6404 StartY=41.0319 StartZ=0 EndX=-20.374 EndY=41.0319 EndZ=0
    g275: LineSegment StartX=-20.374 StartY=41.0319 StartZ=0 EndX=-20.374 EndY=42.1612 EndZ=0
    g276: LineSegment StartX=-20.374 StartY=42.1612 StartZ=0 EndX=-19.9008 EndY=42.1612 EndZ=0
    g277: LineSegment StartX=-19.9008 StartY=42.1612 StartZ=0 EndX=-19.9008 EndY=39.2385 EndZ=0
    g278: LineSegment StartX=-19.9008 StartY=39.2385 StartZ=0 EndX=-20.8472 EndY=39.2385 EndZ=0
    g279: BSplineCurve PolesCount=3 KnotsCount=2 Degree=2 IsPeriodic=0
    g280: BSplineCurve PolesCount=3 KnotsCount=2 Degree=2 IsPeriodic=0
    g281: BSplineCurve PolesCount=3 KnotsCount=2 Degree=2 IsPeriodic=0
    g282: BSplineCurve PolesCount=3 KnotsCount=2 Degree=2 IsPeriodic=0
    g283: BSplineCurve PolesCount=3 KnotsCount=2 Degree=2 IsPeriodic=0
    g284: BSplineCurve PolesCount=3 KnotsCount=2 Degree=2 IsPeriodic=0
    g285: BSplineCurve PolesCount=3 KnotsCount=2 Degree=2 IsPeriodic=0
    g286: BSplineCurve PolesCount=3 KnotsCount=2 Degree=2 IsPeriodic=0
    g287: BSplineCurve PolesCount=3 KnotsCount=2 Degree=2 IsPeriodic=0
    g288: BSplineCurve PolesCount=3 KnotsCount=2 Degree=2 IsPeriodic=0
    g289: LineSegment StartX=-21.1335 StartY=40.9961 StartZ=0 EndX=-21.7379 EndY=42.1612 EndZ=0
    g290: LineSegment StartX=-21.7379 StartY=42.1612 StartZ=0 EndX=-21.225 EndY=42.1612 EndZ=0
    g291: LineSegment StartX=-20.374 StartY=40.6303 StartZ=0 EndX=-20.8472 EndY=40.6303 EndZ=0
    g292: BSplineCurve PolesCount=3 KnotsCount=2 Degree=2 IsPeriodic=0
    g293: BSplineCurve PolesCount=3 KnotsCount=2 Degree=2 IsPeriodic=0
    g294: BSplineCurve PolesCount=3 KnotsCount=2 Degree=2 IsPeriodic=0
    g295: BSplineCurve PolesCount=3 KnotsCount=2 Degree=2 IsPeriodic=0
    g296: BSplineCurve PolesCount=3 KnotsCount=2 Degree=2 IsPeriodic=0
    g297: BSplineCurve PolesCount=3 KnotsCount=2 Degree=2 IsPeriodic=0
    g298: BSplineCurve PolesCount=3 KnotsCount=2 Degree=2 IsPeriodic=0
    g299: BSplineCurve PolesCount=3 KnotsCount=2 Degree=2 IsPeriodic=0
    g300: BSplineCurve PolesCount=3 KnotsCount=2 Degree=2 IsPeriodic=0
    g301: BSplineCurve PolesCount=3 KnotsCount=2 Degree=2 IsPeriodic=0
    g302: BSplineCurve PolesCount=3 KnotsCount=2 Degree=2 IsPeriodic=0
    g303: BSplineCurve PolesCount=3 KnotsCount=2 Degree=2 IsPeriodic=0
    g304: LineSegment StartX=-20.8472 StartY=39.6402 StartZ=0 EndX=-20.374 EndY=39.6402 EndZ=0
    g305: LineSegment StartX=-20.374 StartY=39.6402 StartZ=0 EndX=-20.374 EndY=40.6303 EndZ=0
    g306: BSplineCurve PolesCount=3 KnotsCount=2 Degree=2 IsPeriodic=0
    g307: BSplineCurve PolesCount=3 KnotsCount=2 Degree=2 IsPeriodic=0
    g308: BSplineCurve PolesCount=3 KnotsCount=2 Degree=2 IsPeriodic=0
    g309: BSplineCurve PolesCount=3 KnotsCount=2 Degree=2 IsPeriodic=0
    g310: BSplineCurve PolesCount=3 KnotsCount=2 Degree=2 IsPeriodic=0
    g311: BSplineCurve PolesCount=3 KnotsCount=2 Degree=2 IsPeriodic=0
    g312: LineSegment StartX=-22.2549 StartY=41.3262 StartZ=0 EndX=-22.2549 EndY=40.9285 EndZ=0
    g313: BSplineCurve PolesCount=3 KnotsCount=2 Degree=2 IsPeriodic=0
    g314: BSplineCurve PolesCount=3 KnotsCount=2 Degree=2 IsPeriodic=0
    g315: BSplineCurve PolesCount=3 KnotsCount=2 Degree=2 IsPeriodic=0
    g316: BSplineCurve PolesCount=3 KnotsCount=2 Degree=2 IsPeriodic=0
    g317: BSplineCurve PolesCount=3 KnotsCount=2 Degree=2 IsPeriodic=0
    g318: BSplineCurve PolesCount=3 KnotsCount=2 Degree=2 IsPeriodic=0
    g319: BSplineCurve PolesCount=3 KnotsCount=2 Degree=2 IsPeriodic=0
    g320: BSplineCurve PolesCount=3 KnotsCount=2 Degree=2 IsPeriodic=0
    g321: BSplineCurve PolesCount=3 KnotsCount=2 Degree=2 IsPeriodic=0
    g322: BSplineCurve PolesCount=3 KnotsCount=2 Degree=2 IsPeriodic=0
    g323: BSplineCurve PolesCount=3 KnotsCount=2 Degree=2 IsPeriodic=0
    g324: BSplineCurve PolesCount=3 KnotsCount=2 Degree=2 IsPeriodic=0
    g325: LineSegment StartX=-24.0601 StartY=40.9285 StartZ=0 EndX=-24.0601 EndY=41.3262 EndZ=0
    g326: LineSegment StartX=-24.0601 StartY=41.3262 StartZ=0 EndX=-22.7201 EndY=41.3262 EndZ=0
    g327: BSplineCurve PolesCount=3 KnotsCount=2 Degree=2 IsPeriodic=0
    g328: BSplineCurve PolesCount=3 KnotsCount=2 Degree=2 IsPeriodic=0
    g329: BSplineCurve PolesCount=3 KnotsCount=2 Degree=2 IsPeriodic=0
    g330: BSplineCurve PolesCount=3 KnotsCount=2 Degree=2 IsPeriodic=0
    g331: BSplineCurve PolesCount=3 KnotsCount=2 Degree=2 IsPeriodic=0
    g332: BSplineCurve PolesCount=3 KnotsCount=2 Degree=2 IsPeriodic=0
    g333: BSplineCurve PolesCount=3 KnotsCount=2 Degree=2 IsPeriodic=0
    g334: BSplineCurve PolesCount=3 KnotsCount=2 Degree=2 IsPeriodic=0
    g335: LineSegment StartX=-23.587 StartY=41.5488 StartZ=0 EndX=-24.0522 EndY=41.5488 EndZ=0
    g336: BSplineCurve PolesCount=3 KnotsCount=2 Degree=2 IsPeriodic=0
    g337: BSplineCurve PolesCount=3 KnotsCount=2 Degree=2 IsPeriodic=0
    g338: BSplineCurve PolesCount=3 KnotsCount=2 Degree=2 IsPeriodic=0
    g339: BSplineCurve PolesCount=3 KnotsCount=2 Degree=2 IsPeriodic=0
    g340: BSplineCurve PolesCount=3 KnotsCount=2 Degree=2 IsPeriodic=0
    g341: BSplineCurve PolesCount=3 KnotsCount=2 Degree=2 IsPeriodic=0
    g342: LineSegment StartX=-22.7201 StartY=40.9285 StartZ=0 EndX=-23.5949 EndY=40.9285 EndZ=0
    g343: BSplineCurve PolesCount=3 KnotsCount=2 Degree=2 IsPeriodic=0
    g344: BSplineCurve PolesCount=3 KnotsCount=2 Degree=2 IsPeriodic=0
    g345: BSplineCurve PolesCount=3 KnotsCount=2 Degree=2 IsPeriodic=0
    g346: BSplineCurve PolesCount=3 KnotsCount=2 Degree=2 IsPeriodic=0
    g347: BSplineCurve PolesCount=3 KnotsCount=2 Degree=2 IsPeriodic=0
    g348: BSplineCurve PolesCount=3 KnotsCount=2 Degree=2 IsPeriodic=0
    g349: BSplineCurve PolesCount=3 KnotsCount=2 Degree=2 IsPeriodic=0
    g350: BSplineCurve PolesCount=3 KnotsCount=2 Degree=2 IsPeriodic=0
    g351: LineSegment StartX=-25.2729 StartY=42.1612 StartZ=0 EndX=-24.5492 EndY=40.0935 EndZ=0
    g352: LineSegment StartX=-24.5492 StartY=40.0935 StartZ=0 EndX=-25.0542 EndY=40.0935 EndZ=0
    g353: LineSegment StartX=-25.0542 StartY=40.0935 StartZ=0 EndX=-25.4797 EndY=41.4733 EndZ=0
    g354: BSplineCurve PolesCount=2 KnotsCount=2 Degree=1 IsPeriodic=0
    g355: BSplineCurve PolesCount=2 KnotsCount=2 Degree=1 IsPeriodic=0
    g356: BSplineCurve PolesCount=2 KnotsCount=2 Degree=1 IsPeriodic=0
    g357: BSplineCurve PolesCount=2 KnotsCount=2 Degree=1 IsPeriodic=0
    g358: LineSegment StartX=-25.607 StartY=41.4733 StartZ=0 EndX=-26.0324 EndY=40.0935 EndZ=0
    g359: LineSegment StartX=-26.0324 StartY=40.0935 StartZ=0 EndX=-26.5374 EndY=40.0935 EndZ=0
    g360: LineSegment StartX=-26.5374 StartY=40.0935 StartZ=0 EndX=-25.8137 EndY=42.1612 EndZ=0
    g361: LineSegment StartX=-25.8137 StartY=42.1612 StartZ=0 EndX=-25.2729 EndY=42.1612 EndZ=0
    g362: LineSegment StartX=-27.0583 StartY=42.1612 StartZ=0 EndX=-27.0583 EndY=39.2385 EndZ=0
    g363: LineSegment StartX=-27.0583 StartY=39.2385 StartZ=0 EndX=-27.5315 EndY=39.2385 EndZ=0
    g364: LineSegment StartX=-27.5315 StartY=39.2385 StartZ=0 EndX=-27.5315 EndY=40.4633 EndZ=0
    g365: LineSegment StartX=-27.5315 StartY=40.4633 StartZ=0 EndX=-28.3268 EndY=40.4633 EndZ=0
    g366: LineSegment StartX=-28.3268 StartY=40.4633 StartZ=0 EndX=-28.3268 EndY=39.2385 EndZ=0
    g367: LineSegment StartX=-28.3268 StartY=39.2385 StartZ=0 EndX=-28.8 EndY=39.2385 EndZ=0
    g368: LineSegment StartX=-28.8 StartY=39.2385 StartZ=0 EndX=-28.8 EndY=42.1612 EndZ=0
    g369: LineSegment StartX=-28.8 StartY=42.1612 StartZ=0 EndX=-28.3268 EndY=42.1612 EndZ=0
    g370: LineSegment StartX=-28.3268 StartY=42.1612 StartZ=0 EndX=-28.3268 EndY=40.8649 EndZ=0
    g371: LineSegment StartX=-28.3268 StartY=40.8649 StartZ=0 EndX=-27.5315 EndY=40.8649 EndZ=0
    g372: LineSegment StartX=-27.5315 StartY=40.8649 StartZ=0 EndX=-27.5315 EndY=42.1612 EndZ=0
    g373: LineSegment StartX=-27.5315 StartY=42.1612 StartZ=0 EndX=-27.0583 EndY=42.1612 EndZ=0
  constraints (4):
    c: Horizontal(g0)
    c: DistanceX(g0,g-4) = 3
    c: DistanceX(g-3,g0) = 3
    c: T21(g0,g1,g2)
FEATURE [PartDesign::Pocket] Pocket010
  BaseFeature = -> AdditiveLoft007
  Direction = (0,1,-2e-16)
  Length = 1
  Length2 = 5
  Profile = -> Sketch026
  ReferenceAxis = -> Sketch026 [N_Axis]
  Refine = true
  SideType = 0
  Suppressed = false
  Type = 0
  Type2 = 0
FEATURE [PartDesign::Body] Body004  label="BeaconRevH"
  AllowCompound = true
  Group = -> [Sketch027,Sketch028,Pad012,Pad013,Sketch029,MirroredSketch003,Clone2D004,Pocket011,AdditiveLoft006,Chamfer004,Sketch030,Pocket012,Chamfer005,Sketch031,Sketch032,AdditiveLoft007,Sketch026,Pocket010]
  Origin = -> Origin012
  Placement = pos=(0,0,0) rot=(0,0,1;6.13955rad)
  Tip = -> Pocket010
FEATURE [App::Point] Origin015  label="Origin017"
  Role = Origin
FEATURE [Sketcher::SketchObject] Sketch034
  ArcFitTolerance = 1e-06
  AttachmentOffset = pos=(-16,-2.6,43.3) rot=(0,0,1;0rad)
  AttachmentSupport = -> [Origin014]
  ExternalTypes = [0,0]
  FullyConstrained = true
  MakeInternals = false
  MapMode = 5
  Placement = pos=(-16,-2.6,43.3) rot=(0,0,1;0rad)
  _ExternalGeoVersion = 0
  sketch-geometry (4):
    g0: ArcOfCircle CenterX=-15.8 CenterY=0 CenterZ=0 NormalX=0 NormalY=0 NormalZ=1 AngleXU=0 Radius=4 StartAngle=0.125328 EndAngle=4.71239
    g1: ArcOfCircle CenterX=15.8 CenterY=0 CenterZ=0 NormalX=0 NormalY=0 NormalZ=1 AngleXU=0 Radius=4 StartAngle=4.71239 EndAngle=9.29945
    g2: LineSegment StartX=-15.8 StartY=-4 StartZ=0 EndX=15.8 EndY=-4 EndZ=0
    g3: LineSegment StartX=-11.8314 StartY=0.5 StartZ=0 EndX=11.8314 EndY=0.5 EndZ=0
  constraints (12):
    c: DistanceX(g0,g1) = 31.6
    c: Vertical(g2,g1)
    c: Symmetric(g0,g1,g-2)
    c: Symmetric(g2,g2,g-2)
    c: Horizontal(g3)
    c: PointOnObject(g0,g-1)
    c: DistanceY(g2,g3) = 4.5
    c: DistanceY(g2,g0) = 4
    c: Coincident(g3,g1)
    c: Coincident(g1,g2)
    c: Coincident(g3,g0)
    c: Coincident(g0,g2)
FEATURE [PartDesign::Pad] Pad014
  Direction = (0,0,1)
  Length = 22
  Length2 = 10
  Profile = -> Sketch034
  ReferenceAxis = -> Sketch034 [N_Axis]
  Refine = true
  Reversed = true
  SideType = 0
  Suppressed = false
  Type = 0
  Type2 = 0
FEATURE [Sketcher::SketchObject] Sketch035
  ArcFitTolerance = 1e-06
  AttachmentSupport = -> [Origin014]
  ExternalTypes = [0]
  FullyConstrained = true
  MakeInternals = false
  MapMode = 5
  _ExternalGeoVersion = 0
  expr: Constraints[11] = 5 + 3.5 / 2
  sketch-geometry (6):
    g0: LineSegment StartX=-13.5 StartY=-5.575 StartZ=0 EndX=13.5 EndY=-5.575 EndZ=0
    g1: LineSegment StartX=13.5 StartY=-5.575 StartZ=0 EndX=13.5 EndY=5.575 EndZ=0
    g2: Circle CenterX=-9 CenterY=1.175 CenterZ=0 NormalX=0 NormalY=0 NormalZ=1 AngleXU=0 Radius=1.75
    g3: Circle CenterX=9 CenterY=1.175 CenterZ=0 NormalX=0 NormalY=0 NormalZ=1 AngleXU=0 Radius=1.75
    g4: LineSegment StartX=-13.5 StartY=-5.575 StartZ=0 EndX=-13.5 EndY=5.575 EndZ=0
    g5: LineSegment StartX=-13.5 StartY=5.575 StartZ=0 EndX=13.5 EndY=5.575 EndZ=0
  constraints (16):
    c: Equal(g3,g2)
    c: Diameter(g3) = 3.5
    c: Symmetric(g2,g3,g-2)
    c: Coincident(g4,g0)
    c: Vertical(g4)
    c: Coincident(g5,g4)
    c: Coincident(g5,g1)
    c: Horizontal(g5)
    c: DistanceY(g4,g4) = 11.15
    c: Symmetric(g4,g0,g-1)
    c: DistanceX(g5,g5) = 27
    c: DistanceY(g0,g2) = 6.75
    c: DistanceX(g2,g3) = 18
    c: Horizontal(g0)
    c: Vertical(g1)
    c: Coincident(g1,g0)
FEATURE [PartDesign::Pad] Pad015
  BaseFeature = -> Pad014
  Direction = (0,0,1)
  Length = 3
  Length2 = 10
  Profile = -> Sketch035
  ReferenceAxis = -> Sketch035 [N_Axis]
  Refine = true
  SideType = 0
  Suppressed = false
  Type = 0
  Type2 = 0
FEATURE [Sketcher::SketchObject] MirroredSketch004
  ArcFitTolerance = 1e-06
  AttachmentOffset = pos=(14,-18,0) rot=(0,0,1;0rad)
  AttachmentSupport = -> [Pad015]
  ExternalTypes = [0]
  FullyConstrained = false
  MakeInternals = false
  MapMode = 5
  Placement = pos=(-14,-2.1,-18) rot=(0,0.707107,0.707107;3.14159rad)
  _ExternalGeoVersion = 0
  sketch-geometry (160):
    g0: BSplineCurve PolesCount=4 KnotsCount=2 Degree=3 IsPeriodic=0
    g1: BSplineCurve PolesCount=4 KnotsCount=2 Degree=3 IsPeriodic=0
    g2: BSplineCurve PolesCount=4 KnotsCount=2 Degree=3 IsPeriodic=0
    g3: BSplineCurve PolesCount=4 KnotsCount=2 Degree=3 IsPeriodic=0
    g4: BSplineCurve PolesCount=4 KnotsCount=2 Degree=3 IsPeriodic=0
    g5: BSplineCurve PolesCount=4 KnotsCount=2 Degree=3 IsPeriodic=0
    g6: BSplineCurve PolesCount=4 KnotsCount=2 Degree=3 IsPeriodic=0
    g7: BSplineCurve PolesCount=4 KnotsCount=2 Degree=3 IsPeriodic=0
    g8: BSplineCurve PolesCount=4 KnotsCount=2 Degree=3 IsPeriodic=0
    g9: BSplineCurve PolesCount=4 KnotsCount=2 Degree=3 IsPeriodic=0
    g10: BSplineCurve PolesCount=4 KnotsCount=2 Degree=3 IsPeriodic=0
    g11: BSplineCurve PolesCount=4 KnotsCount=2 Degree=3 IsPeriodic=0
    g12: BSplineCurve PolesCount=4 KnotsCount=2 Degree=3 IsPeriodic=0
    g13: BSplineCurve PolesCount=4 KnotsCount=2 Degree=3 IsPeriodic=0
    g14: BSplineCurve PolesCount=4 KnotsCount=2 Degree=3 IsPeriodic=0
    g15: BSplineCurve PolesCount=4 KnotsCount=2 Degree=3 IsPeriodic=0
    g16: BSplineCurve PolesCount=4 KnotsCount=2 Degree=3 IsPeriodic=0
    g17: BSplineCurve PolesCount=4 KnotsCount=2 Degree=3 IsPeriodic=0
    g18: BSplineCurve PolesCount=4 KnotsCount=2 Degree=3 IsPeriodic=0
    g19: BSplineCurve PolesCount=4 KnotsCount=2 Degree=3 IsPeriodic=0
    g20: BSplineCurve PolesCount=4 KnotsCount=2 Degree=3 IsPeriodic=0
    g21: BSplineCurve PolesCount=4 KnotsCount=2 Degree=3 IsPeriodic=0
    g22: BSplineCurve PolesCount=4 KnotsCount=2 Degree=3 IsPeriodic=0
    g23: BSplineCurve PolesCount=4 KnotsCount=2 Degree=3 IsPeriodic=0
    g24: BSplineCurve PolesCount=4 KnotsCount=2 Degree=3 IsPeriodic=0
    g25: BSplineCurve PolesCount=4 KnotsCount=2 Degree=3 IsPeriodic=0
    g26: BSplineCurve PolesCount=4 KnotsCount=2 Degree=3 IsPeriodic=0
    g27: BSplineCurve PolesCount=4 KnotsCount=2 Degree=3 IsPeriodic=0
    g28: BSplineCurve PolesCount=4 KnotsCount=2 Degree=3 IsPeriodic=0
    g29: BSplineCurve PolesCount=4 KnotsCount=2 Degree=3 IsPeriodic=0
    g30: BSplineCurve PolesCount=4 KnotsCount=2 Degree=3 IsPeriodic=0
    g31: BSplineCurve PolesCount=4 KnotsCount=2 Degree=3 IsPeriodic=0
    g32: BSplineCurve PolesCount=4 KnotsCount=2 Degree=3 IsPeriodic=0
    g33: BSplineCurve PolesCount=4 KnotsCount=2 Degree=3 IsPeriodic=0
    g34: BSplineCurve PolesCount=4 KnotsCount=2 Degree=3 IsPeriodic=0
    g35: BSplineCurve PolesCount=4 KnotsCount=2 Degree=3 IsPeriodic=0
    g36: BSplineCurve PolesCount=4 KnotsCount=2 Degree=3 IsPeriodic=0
    g37: BSplineCurve PolesCount=4 KnotsCount=2 Degree=3 IsPeriodic=0
    g38: BSplineCurve PolesCount=4 KnotsCount=2 Degree=3 IsPeriodic=0
    g39: BSplineCurve PolesCount=4 KnotsCount=2 Degree=3 IsPeriodic=0
    g40: BSplineCurve PolesCount=4 KnotsCount=2 Degree=3 IsPeriodic=0
    g41: BSplineCurve PolesCount=4 KnotsCount=2 Degree=3 IsPeriodic=0
    g42: BSplineCurve PolesCount=4 KnotsCount=2 Degree=3 IsPeriodic=0
    g43: BSplineCurve PolesCount=4 KnotsCount=2 Degree=3 IsPeriodic=0
    g44: BSplineCurve PolesCount=4 KnotsCount=2 Degree=3 IsPeriodic=0
    g45: BSplineCurve PolesCount=4 KnotsCount=2 Degree=3 IsPeriodic=0
    g46: BSplineCurve PolesCount=4 KnotsCount=2 Degree=3 IsPeriodic=0
    g47: BSplineCurve PolesCount=4 KnotsCount=2 Degree=3 IsPeriodic=0
    g48: BSplineCurve PolesCount=4 KnotsCount=2 Degree=3 IsPeriodic=0
    g49: BSplineCurve PolesCount=4 KnotsCount=2 Degree=3 IsPeriodic=0
    g50: BSplineCurve PolesCount=4 KnotsCount=2 Degree=3 IsPeriodic=0
    g51: BSplineCurve PolesCount=4 KnotsCount=2 Degree=3 IsPeriodic=0
    g52: BSplineCurve PolesCount=4 KnotsCount=2 Degree=3 IsPeriodic=0
    g53: BSplineCurve PolesCount=4 KnotsCount=2 Degree=3 IsPeriodic=0
    g54: BSplineCurve PolesCount=4 KnotsCount=2 Degree=3 IsPeriodic=0
    g55: BSplineCurve PolesCount=4 KnotsCount=2 Degree=3 IsPeriodic=0
    g56: BSplineCurve PolesCount=4 KnotsCount=2 Degree=3 IsPeriodic=0
    g57: BSplineCurve PolesCount=4 KnotsCount=2 Degree=3 IsPeriodic=0
    g58: BSplineCurve PolesCount=4 KnotsCount=2 Degree=3 IsPeriodic=0
    g59: BSplineCurve PolesCount=4 KnotsCount=2 Degree=3 IsPeriodic=0
    g60: BSplineCurve PolesCount=4 KnotsCount=2 Degree=3 IsPeriodic=0
    g61: BSplineCurve PolesCount=4 KnotsCount=2 Degree=3 IsPeriodic=0
    g62: BSplineCurve PolesCount=4 KnotsCount=2 Degree=3 IsPeriodic=0
    g63: BSplineCurve PolesCount=4 KnotsCount=2 Degree=3 IsPeriodic=0
    g64: BSplineCurve PolesCount=4 KnotsCount=2 Degree=3 IsPeriodic=0
    g65: BSplineCurve PolesCount=4 KnotsCount=2 Degree=3 IsPeriodic=0
    g66: BSplineCurve PolesCount=4 KnotsCount=2 Degree=3 IsPeriodic=0
    g67: BSplineCurve PolesCount=4 KnotsCount=2 Degree=3 IsPeriodic=0
    g68: BSplineCurve PolesCount=4 KnotsCount=2 Degree=3 IsPeriodic=0
    g69: BSplineCurve PolesCount=4 KnotsCount=2 Degree=3 IsPeriodic=0
    g70: BSplineCurve PolesCount=4 KnotsCount=2 Degree=3 IsPeriodic=0
    g71: BSplineCurve PolesCount=4 KnotsCount=2 Degree=3 IsPeriodic=0
    g72: BSplineCurve PolesCount=4 KnotsCount=2 Degree=3 IsPeriodic=0
    g73: BSplineCurve PolesCount=4 KnotsCount=2 Degree=3 IsPeriodic=0
    g74: BSplineCurve PolesCount=4 KnotsCount=2 Degree=3 IsPeriodic=0
    g75: BSplineCurve PolesCount=4 KnotsCount=2 Degree=3 IsPeriodic=0
    g76: BSplineCurve PolesCount=4 KnotsCount=2 Degree=3 IsPeriodic=0
    g77: BSplineCurve PolesCount=4 KnotsCount=2 Degree=3 IsPeriodic=0
    g78: BSplineCurve PolesCount=4 KnotsCount=2 Degree=3 IsPeriodic=0
    g79: BSplineCurve PolesCount=4 KnotsCount=2 Degree=3 IsPeriodic=0
    g80: BSplineCurve PolesCount=4 KnotsCount=2 Degree=3 IsPeriodic=0
    g81: BSplineCurve PolesCount=4 KnotsCount=2 Degree=3 IsPeriodic=0
    g82: BSplineCurve PolesCount=4 KnotsCount=2 Degree=3 IsPeriodic=0
    g83: BSplineCurve PolesCount=4 KnotsCount=2 Degree=3 IsPeriodic=0
    g84: BSplineCurve PolesCount=4 KnotsCount=2 Degree=3 IsPeriodic=0
    g85: BSplineCurve PolesCount=4 KnotsCount=2 Degree=3 IsPeriodic=0
    g86: BSplineCurve PolesCount=4 KnotsCount=2 Degree=3 IsPeriodic=0
    g87: BSplineCurve PolesCount=4 KnotsCount=2 Degree=3 IsPeriodic=0
    g88: BSplineCurve PolesCount=4 KnotsCount=2 Degree=3 IsPeriodic=0
    g89: BSplineCurve PolesCount=4 KnotsCount=2 Degree=3 IsPeriodic=0
    g90: BSplineCurve PolesCount=4 KnotsCount=2 Degree=3 IsPeriodic=0
    g91: BSplineCurve PolesCount=4 KnotsCount=2 Degree=3 IsPeriodic=0
    g92: BSplineCurve PolesCount=4 KnotsCount=2 Degree=3 IsPeriodic=0
    g93: BSplineCurve PolesCount=4 KnotsCount=2 Degree=3 IsPeriodic=0
    g94: BSplineCurve PolesCount=4 KnotsCount=2 Degree=3 IsPeriodic=0
    g95: BSplineCurve PolesCount=4 KnotsCount=2 Degree=3 IsPeriodic=0
    g96: BSplineCurve PolesCount=4 KnotsCount=2 Degree=3 IsPeriodic=0
    g97: BSplineCurve PolesCount=4 KnotsCount=2 Degree=3 IsPeriodic=0
    g98: BSplineCurve PolesCount=4 KnotsCount=2 Degree=3 IsPeriodic=0
    g99: BSplineCurve PolesCount=4 KnotsCount=2 Degree=3 IsPeriodic=0
    g100: BSplineCurve PolesCount=4 KnotsCount=2 Degree=3 IsPeriodic=0
    g101: BSplineCurve PolesCount=4 KnotsCount=2 Degree=3 IsPeriodic=0
    g102: BSplineCurve PolesCount=4 KnotsCount=2 Degree=3 IsPeriodic=0
    g103: BSplineCurve PolesCount=4 KnotsCount=2 Degree=3 IsPeriodic=0
    g104: BSplineCurve PolesCount=4 KnotsCount=2 Degree=3 IsPeriodic=0
    g105: BSplineCurve PolesCount=2 KnotsCount=2 Degree=1 IsPeriodic=0
    g106: BSplineCurve PolesCount=4 KnotsCount=2 Degree=3 IsPeriodic=0
    g107: BSplineCurve PolesCount=4 KnotsCount=2 Degree=3 IsPeriodic=0
    g108: BSplineCurve PolesCount=4 KnotsCount=2 Degree=3 IsPeriodic=0
    g109: BSplineCurve PolesCount=4 KnotsCount=2 Degree=3 IsPeriodic=0
    g110: BSplineCurve PolesCount=4 KnotsCount=2 Degree=3 IsPeriodic=0
    g111: BSplineCurve PolesCount=4 KnotsCount=2 Degree=3 IsPeriodic=0
    g112: BSplineCurve PolesCount=4 KnotsCount=2 Degree=3 IsPeriodic=0
    g113: BSplineCurve PolesCount=4 KnotsCount=2 Degree=3 IsPeriodic=0
    g114: BSplineCurve PolesCount=4 KnotsCount=2 Degree=3 IsPeriodic=0
    g115: BSplineCurve PolesCount=4 KnotsCount=2 Degree=3 IsPeriodic=0
    g116: BSplineCurve PolesCount=4 KnotsCount=2 Degree=3 IsPeriodic=0
    g117: BSplineCurve PolesCount=4 KnotsCount=2 Degree=3 IsPeriodic=0
    g118: BSplineCurve PolesCount=4 KnotsCount=2 Degree=3 IsPeriodic=0
    g119: BSplineCurve PolesCount=4 KnotsCount=2 Degree=3 IsPeriodic=0
    g120: BSplineCurve PolesCount=4 KnotsCount=2 Degree=3 IsPeriodic=0
    g121: BSplineCurve PolesCount=4 KnotsCount=2 Degree=3 IsPeriodic=0
    g122: BSplineCurve PolesCount=4 KnotsCount=2 Degree=3 IsPeriodic=0
    g123: BSplineCurve PolesCount=4 KnotsCount=2 Degree=3 IsPeriodic=0
    g124: BSplineCurve PolesCount=4 KnotsCount=2 Degree=3 IsPeriodic=0
    g125: BSplineCurve PolesCount=4 KnotsCount=2 Degree=3 IsPeriodic=0
    g126: BSplineCurve PolesCount=4 KnotsCount=2 Degree=3 IsPeriodic=0
    g127: BSplineCurve PolesCount=4 KnotsCount=2 Degree=3 IsPeriodic=0
    g128: BSplineCurve PolesCount=4 KnotsCount=2 Degree=3 IsPeriodic=0
    g129: BSplineCurve PolesCount=4 KnotsCount=2 Degree=3 IsPeriodic=0
    g130: BSplineCurve PolesCount=4 KnotsCount=2 Degree=3 IsPeriodic=0
    g131: BSplineCurve PolesCount=4 KnotsCount=2 Degree=3 IsPeriodic=0
    g132: BSplineCurve PolesCount=4 KnotsCount=2 Degree=3 IsPeriodic=0
    g133: BSplineCurve PolesCount=4 KnotsCount=2 Degree=3 IsPeriodic=0
    g134: BSplineCurve PolesCount=4 KnotsCount=2 Degree=3 IsPeriodic=0
    g135: BSplineCurve PolesCount=4 KnotsCount=2 Degree=3 IsPeriodic=0
    g136: BSplineCurve PolesCount=4 KnotsCount=2 Degree=3 IsPeriodic=0
    g137: BSplineCurve PolesCount=4 KnotsCount=2 Degree=3 IsPeriodic=0
    g138: BSplineCurve PolesCount=4 KnotsCount=2 Degree=3 IsPeriodic=0
    g139: BSplineCurve PolesCount=4 KnotsCount=2 Degree=3 IsPeriodic=0
    g140: BSplineCurve PolesCount=4 KnotsCount=2 Degree=3 IsPeriodic=0
    g141: BSplineCurve PolesCount=4 KnotsCount=2 Degree=3 IsPeriodic=0
    g142: BSplineCurve PolesCount=4 KnotsCount=2 Degree=3 IsPeriodic=0
    g143: BSplineCurve PolesCount=4 KnotsCount=2 Degree=3 IsPeriodic=0
    g144: BSplineCurve PolesCount=4 KnotsCount=2 Degree=3 IsPeriodic=0
    g145: BSplineCurve PolesCount=4 KnotsCount=2 Degree=3 IsPeriodic=0
    g146: BSplineCurve PolesCount=4 KnotsCount=2 Degree=3 IsPeriodic=0
    g147: BSplineCurve PolesCount=4 KnotsCount=2 Degree=3 IsPeriodic=0
    g148: BSplineCurve PolesCount=4 KnotsCount=2 Degree=3 IsPeriodic=0
    g149: BSplineCurve PolesCount=4 KnotsCount=2 Degree=3 IsPeriodic=0
    g150: BSplineCurve PolesCount=4 KnotsCount=2 Degree=3 IsPeriodic=0
    g151: BSplineCurve PolesCount=4 KnotsCount=2 Degree=3 IsPeriodic=0
    g152: BSplineCurve PolesCount=4 KnotsCount=2 Degree=3 IsPeriodic=0
    g153: BSplineCurve PolesCount=4 KnotsCount=2 Degree=3 IsPeriodic=0
    g154: BSplineCurve PolesCount=4 KnotsCount=2 Degree=3 IsPeriodic=0
    g155: BSplineCurve PolesCount=4 KnotsCount=2 Degree=3 IsPeriodic=0
    g156: BSplineCurve PolesCount=4 KnotsCount=2 Degree=3 IsPeriodic=0
    g157: BSplineCurve PolesCount=4 KnotsCount=2 Degree=3 IsPeriodic=0
    g158: BSplineCurve PolesCount=4 KnotsCount=2 Degree=3 IsPeriodic=0
    g159: BSplineCurve PolesCount=4 KnotsCount=2 Degree=3 IsPeriodic=0
  constraints (160):
    c: Coincident(g10,g11)
    c: Coincident(g4,g5)
    c: Coincident(g11,g12)
    c: Coincident(g0,g12)
    c: Coincident(g5,g6)
    c: Coincident(g9,g10)
    c: Coincident(g0,g1)
    c: Coincident(g8,g9)
    c: Coincident(g1,g2)
    c: Coincident(g3,g4)
    c: Coincident(g2,g3)
    c: Coincident(g7,g8)
    c: Coincident(g6,g7)
    c: Coincident(g79,g80)
    c: Coincident(g96,g97)
    c: Coincident(g109,g110)
    c: Coincident(g13,g26)
    c: Coincident(g110,g111)
    c: Coincident(g13,g14)
    c: Coincident(g136,g137)
    c: Coincident(g102,g103)
    c: Coincident(g82,g83)
    c: Coincident(g137,g138)
    c: Coincident(g103,g104)
    c: Coincident(g78,g79)
    c: Coincident(g83,g84)
    c: Coincident(g80,g81)
    c: Coincident(g25,g26)
    c: Coincident(g95,g96)
    c: Coincident(g108,g109)
    c: Coincident(g73,g81)
    c: Coincident(g14,g15)
    c: Coincident(g111,g112)
    c: Coincident(g127,g131)
    c: Coincident(g127,g128)
    c: Coincident(g87,g88)
    c: Coincident(g91,g92)
    c: Coincident(g112,g113)
    c: Coincident(g15,g16)
    c: Coincident(g130,g131)
    c: Coincident(g97,g98)
    c: Coincident(g88,g89)
    c: Coincident(g84,g85)
    c: Coincident(g92,g93)
    c: Coincident(g113,g114)
    c: Coincident(g16,g17)
    c: Coincident(g17,g18)
    c: Coincident(g114,g115)
    c: Coincident(g82,g100)
    c: Coincident(g129,g130)
    c: Coincident(g128,g129)
    c: Coincident(g73,g74)
    c: Coincident(g107,g108)
    c: Coincident(g135,g136)
    c: Coincident(g18,g19)
    c: Coincident(g19,g20)
    c: Coincident(g106,g107)
    c: Coincident(g24,g25)
    c: Coincident(g99,g100)
    c: Coincident(g106,g120)
    c: Coincident(g74,g75)
    c: Coincident(g75,g76)
    c: Coincident(g138,g139)
    c: Coincident(g119,g120)
    c: Coincident(g139,g140)
    c: Coincident(g132,g140)
    c: Coincident(g20,g21)
    c: Coincident(g98,g99)
    c: Coincident(g118,g119)
    c: Coincident(g132,g133)
    c: Coincident(g21,g22)
    c: Coincident(g115,g116)
    c: Coincident(g90,g91)
    c: Coincident(g89,g90)
    c: Coincident(g77,g78)
    c: Coincident(g134,g135)
    c: Coincident(g85,g86)
    c: Coincident(g86,g87)
    c: Coincident(g23,g24)
    c: Coincident(g104,g105)
    c: Coincident(g101,g102)
    c: Coincident(g94,g95)
    c: Coincident(g117,g118)
    c: Coincident(g101,g105)
    c: Coincident(g22,g23)
    c: Coincident(g93,g94)
    c: Coincident(g76,g77)
    c: Coincident(g133,g134)
    c: Coincident(g116,g117)
    c: Coincident(g148,g149)
    c: Coincident(g157,g158)
    c: Coincident(g158,g159)
    c: Coincident(g147,g148)
    c: Coincident(g146,g147)
    c: Coincident(g156,g157)
    c: Coincident(g149,g150)
    c: Coincident(g57,g58)
    c: Coincident(g155,g156)
    c: Coincident(g46,g47)
    c: Coincident(g56,g57)
    c: Coincident(g47,g48)
    c: Coincident(g48,g49)
    c: Coincident(g45,g46)
    c: Coincident(g150,g151)
    c: Coincident(g55,g56)
    c: Coincident(g49,g50)
    c: Coincident(g122,g123)
    c: Coincident(g43,g44)
    c: Coincident(g44,g45)
    c: Coincident(g54,g55)
    c: Coincident(g123,g124)
    c: Coincident(g42,g43)
    c: Coincident(g50,g51)
    c: Coincident(g124,g125)
    c: Coincident(g53,g54)
    c: Coincident(g40,g41)
    c: Coincident(g52,g53)
    c: Coincident(g51,g52)
    c: Coincident(g58,g59)
    c: Coincident(g121,g122)
    c: Coincident(g39,g40)
    c: Coincident(g41,g42)
    c: Coincident(g38,g39)
    c: Coincident(g125,g126)
    c: Coincident(g121,g126)
    c: Coincident(g32,g33)
    c: Coincident(g31,g32)
    c: Coincident(g153,g159)
    c: Coincident(g37,g38)
    c: Coincident(g59,g60)
    c: Coincident(g67,g68)
    c: Coincident(g154,g155)
    c: Coincident(g66,g67)
    c: Coincident(g36,g37)
    c: Coincident(g60,g61)
    c: Coincident(g153,g154)
    c: Coincident(g65,g66)
    c: Coincident(g68,g69)
    c: Coincident(g71,g72)
    c: Coincident(g141,g144)
    c: Coincident(g33,g34)
    c: Coincident(g64,g65)
    c: Coincident(g145,g146)
    c: Coincident(g141,g142)
    c: Coincident(g63,g64)
    c: Coincident(g145,g152)
    c: Coincident(g143,g144)
    c: Coincident(g61,g62)
    c: Coincident(g34,g35)
    c: Coincident(g29,g30)
    c: Coincident(g35,g36)
    c: Coincident(g62,g63)
    c: Coincident(g27,g30)
    c: Coincident(g69,g70)
    c: Coincident(g70,g71)
    c: Coincident(g142,g143)
    c: Coincident(g28,g29)
    c: Coincident(g151,g152)
    c: Coincident(g27,g28)
    c: Coincident(g31,g72)
FEATURE [Part::Part2DObjectPython] Clone2D005  label="MirroredSketch001 (2D)004"  # Draft 2D object (typed FeaturePython)
  AttachmentOffset = pos=(4.3,23,0) rot=(0,0,-1;1.5708rad)
  AttachmentSupport = -> [Pad015]
  ForceCompound = false
  Fuse = false
  MapMode = 5
  Objects = -> [MirroredSketch004]
  Placement = pos=(-4.3,-2.1,23) rot=(-0.57735,0.57735,0.57735;2.0944rad)
  Scale = (0.65,0.65,0.65)
FEATURE [PartDesign::Pocket] Pocket014
  BaseFeature = -> Pad015
  Direction = (0,-1,2e-16)
  Length = 2
  Length2 = 5
  Profile = -> Clone2D005
  ReferenceAxis = -> Clone2D005 [N_Axis]
  Refine = true
  SideType = 0
  Suppressed = false
  Type = 0
  Type2 = 0
FEATURE [Sketcher::SketchObject] Sketch036
  ArcFitTolerance = 1e-06
  AttachmentSupport = -> [Pad015]
  ExternalGeometry = -> [Pad015]
  ExternalTypes = [0,0]
  FullyConstrained = true
  MakeInternals = false
  MapMode = 5
  Placement = pos=(0,0,3) rot=(0,0,1;0rad)
  _ExternalGeoVersion = 0
  sketch-geometry (4):
    g0: LineSegment StartX=-13.5 StartY=-5.575 StartZ=0 EndX=13.5 EndY=-5.575 EndZ=0
    g1: LineSegment StartX=13.5 StartY=-5.575 StartZ=0 EndX=13.5 EndY=-2.575 EndZ=0
    g2: LineSegment StartX=13.5 StartY=-2.575 StartZ=0 EndX=-13.5 EndY=-2.575 EndZ=0
    g3: LineSegment StartX=-13.5 StartY=-2.575 StartZ=0 EndX=-13.5 EndY=-5.575 EndZ=0
  constraints (11):
    c: Coincident(g0,g1)
    c: Coincident(g1,g2)
    c: Coincident(g2,g3)
    c: Coincident(g3,g0)
    c: Horizontal(g2)
    c: Vertical(g1)
    c: Vertical(g3)
    c: DistanceY(g1,g1) = 3
    c: Horizontal(g0)
    c: Coincident(g0,g-3)
    c: PointOnObject(g2,g-4)
FEATURE [PartDesign::AdditiveLoft] AdditiveLoft008
  BaseFeature = -> Pocket014
  Closed = false
  Profile = -> Sketch036
  Refine = true
  Ruled = false
  Sections = -> [Pocket014]
  Suppressed = false
FEATURE [PartDesign::Chamfer] Chamfer006
  Angle = 45
  Base = -> AdditiveLoft008 [Edge468,Edge489]
  BaseFeature = -> AdditiveLoft008
  ChamferType = 0
  FlipDirection = false
  Refine = true
  Size = 2
  Size2 = 1
  SupportTransform = false
  Suppressed = false
  UseAllEdges = false
FEATURE [Sketcher::SketchObject] Sketch037
  ArcFitTolerance = 1e-06
  AttachmentSupport = -> [Chamfer006]
  ExternalGeometry = -> [Chamfer006]
  ExternalTypes = [0,0]
  FullyConstrained = true
  MakeInternals = false
  MapMode = 5
  Placement = pos=(0,0,43.3) rot=(0,0,1;0rad)
  _ExternalGeoVersion = 0
  sketch-geometry (2):
    g0: Circle CenterX=-31.8 CenterY=-2.6 CenterZ=0 NormalX=0 NormalY=0 NormalZ=1 AngleXU=0 Radius=1.75
    g1: Circle CenterX=-0.2 CenterY=-2.6 CenterZ=0 NormalX=0 NormalY=0 NormalZ=1 AngleXU=0 Radius=1.75
  constraints (4):
    c: Coincident(g0,g-4)
    c: Coincident(g1,g-3)
    c: Equal(g1,g0)
    c: Diameter(g0) = 3.5
FEATURE [PartDesign::Pocket] Pocket015
  BaseFeature = -> Chamfer006
  Direction = (0,0,-1)
  Length = 11
  Length2 = 5
  Profile = -> Sketch037
  ReferenceAxis = -> Sketch037 [N_Axis]
  Refine = true
  SideType = 0
  Suppressed = false
  Type = 0
  Type2 = 0
FEATURE [Sketcher::SketchObject] Sketch038
  ArcFitTolerance = 1e-06
  ExternalTypes = [0,0]
  FullyConstrained = true
  MakeInternals = false
  MapMode = 5
  Placement = pos=(0,0,3) rot=(0,0,1;0rad)
  _ExternalGeoVersion = 0
  sketch-geometry (4):
    g0: LineSegment StartX=-5 StartY=-2.575 StartZ=0 EndX=5 EndY=-2.575 EndZ=0
    g1: LineSegment StartX=5 StartY=-2.575 StartZ=0 EndX=5 EndY=5.575 EndZ=0
    g2: LineSegment StartX=5 StartY=5.575 StartZ=0 EndX=-5 EndY=5.575 EndZ=0
    g3: LineSegment StartX=-5 StartY=5.575 StartZ=0 EndX=-5 EndY=-2.575 EndZ=0
  constraints (11):
    c: Coincident(g0,g1)
    c: Coincident(g1,g2)
    c: Coincident(g2,g3)
    c: Coincident(g3,g0)
    c: Horizontal(g0)
    c: Vertical(g1)
    c: Vertical(g3)
    c: PointOnObject(g0,g-3)
    c: PointOnObject(g1,g-4)
    c: DistanceX(g2,g2) = 10
    c: Symmetric(g1,g2,g-2)
FEATURE [Sketcher::SketchObject] Sketch039
  ArcFitTolerance = 1e-06
  ExternalTypes = [0]
  FullyConstrained = true
  MakeInternals = false
  MapMode = 5
  Placement = pos=(1e-16,-2.65108,0.0688123) rot=(0,0.716222,0.697873;3.14159rad)
  _ExternalGeoVersion = 0
  sketch-geometry (4):
    g0: LineSegment StartX=-5.5 StartY=11.0322 StartZ=0 EndX=-5.5 EndY=10.9322 EndZ=0
    g1: LineSegment StartX=-5.5 StartY=10.9322 StartZ=0 EndX=4.5 EndY=10.9322 EndZ=0
    g2: LineSegment StartX=4.5 StartY=10.9322 StartZ=0 EndX=4.5 EndY=11.0322 EndZ=0
    g3: LineSegment StartX=4.5 StartY=11.0322 StartZ=0 EndX=-5.5 EndY=11.0322 EndZ=0
  constraints (12):
    c: Coincident(g0,g1)
    c: Coincident(g1,g2)
    c: Coincident(g2,g3)
    c: Coincident(g3,g0)
    c: Vertical(g0)
    c: Vertical(g2)
    c: Horizontal(g1)
    c: Horizontal(g3)
    c: DistanceX(g3,g3) = 10
    c: DistanceY(g2,g2) = 0.1
    c: DistanceY(g-3,g0) = 8
    c: DistanceX(g-3,g0) = 8
FEATURE [PartDesign::AdditiveLoft] AdditiveLoft009
  BaseFeature = -> Pocket015
  Closed = false
  Profile = -> Sketch038
  Refine = true
  Ruled = false
  Sections = -> [Sketch039]
  Suppressed = false
FEATURE [Sketcher::SketchObject] Sketch040
  ArcFitTolerance = 1e-06
  AttachmentSupport = -> [AdditiveLoft009]
  ExternalGeometry = -> [Sketch037,AdditiveLoft009]
  ExternalTypes = [0,0]
  FullyConstrained = true
  MakeInternals = false
  MapMode = 5
  Placement = pos=(0,0,43.3) rot=(0,0,1;0rad)
  _ExternalGeoVersion = 0
  sketch-geometry (2):
    g0: Circle CenterX=-31.8 CenterY=-2.6 CenterZ=0 NormalX=0 NormalY=0 NormalZ=1 AngleXU=0 Radius=2
    g1: Circle CenterX=-0.2 CenterY=-2.6 CenterZ=0 NormalX=0 NormalY=0 NormalZ=1 AngleXU=0 Radius=2
  constraints (4):
    c: Coincident(g0,g-4)
    c: Coincident(g1,g-3)
    c: Equal(g0,g1)
    c: Diameter(g1) = 4
FEATURE [PartDesign::Pocket] Pocket016
  BaseFeature = -> AdditiveLoft009
  Direction = (0,0,-1)
  Length = 5
  Length2 = 5
  Profile = -> Sketch040
  ReferenceAxis = -> Sketch040 [N_Axis]
  Refine = true
  SideType = 0
  Suppressed = false
  Type = 0
  Type2 = 0
FEATURE [Sketcher::SketchObject] Sketch041
  ArcFitTolerance = 1e-06
  AttachmentSupport = -> [Pocket016]
  ExternalTypes = [0]
  FullyConstrained = false
  MakeInternals = false
  MapMode = 5
  Placement = pos=(0,-6.6,0) rot=(1,0,0;1.5708rad)
  _ExternalGeoVersion = 0
  sketch-geometry (263):
    g0: LineSegment [constr] StartX=-1.07861 StartY=42.2016 StartZ=0 EndX=-30.576 EndY=42.0699 EndZ=0
    g1: BSplineCurve PolesCount=3 KnotsCount=2 Degree=2 IsPeriodic=0
    g2: BSplineCurve PolesCount=3 KnotsCount=2 Degree=2 IsPeriodic=0
    g3: BSplineCurve PolesCount=3 KnotsCount=2 Degree=2 IsPeriodic=0
    g4: LineSegment StartX=-2.45691 StartY=38.4054 StartZ=0 EndX=-1.8301 EndY=38.4082 EndZ=0
    g5: BSplineCurve PolesCount=3 KnotsCount=2 Degree=2 IsPeriodic=0
    g6: BSplineCurve PolesCount=3 KnotsCount=2 Degree=2 IsPeriodic=0
    g7: LineSegment StartX=-1.3678 StartY=38.8747 StartZ=0 EndX=-1.3749 EndY=40.4656 EndZ=0
    g8: BSplineCurve PolesCount=3 KnotsCount=2 Degree=2 IsPeriodic=0
    g9: BSplineCurve PolesCount=3 KnotsCount=2 Degree=2 IsPeriodic=0
    g10: LineSegment StartX=-1.79354 StartY=40.9469 StartZ=0 EndX=-2.49323 EndY=40.9438 EndZ=0
    g11: BSplineCurve PolesCount=3 KnotsCount=2 Degree=2 IsPeriodic=0
    g12: BSplineCurve PolesCount=3 KnotsCount=2 Degree=2 IsPeriodic=0
    g13: LineSegment StartX=-2.49247 StartY=41.2395 StartZ=0 EndX=-1.78236 EndY=41.2427 EndZ=0
    g14: BSplineCurve PolesCount=3 KnotsCount=2 Degree=2 IsPeriodic=0
    g15: BSplineCurve PolesCount=3 KnotsCount=2 Degree=2 IsPeriodic=0
    g16: LineSegment StartX=-1.07094 StartY=40.4837 StartZ=0 EndX=-1.06366 EndY=38.8531 EndZ=0
    g17: BSplineCurve PolesCount=3 KnotsCount=2 Degree=2 IsPeriodic=0
    g18: BSplineCurve PolesCount=3 KnotsCount=2 Degree=2 IsPeriodic=0
    g19: BSplineCurve PolesCount=3 KnotsCount=2 Degree=2 IsPeriodic=0
    g20: BSplineCurve PolesCount=3 KnotsCount=2 Degree=2 IsPeriodic=0
    g21: BSplineCurve PolesCount=3 KnotsCount=2 Degree=2 IsPeriodic=0
    g22: BSplineCurve PolesCount=3 KnotsCount=2 Degree=2 IsPeriodic=0
    g23: LineSegment StartX=-3.68431 StartY=40.926 StartZ=0 EndX=-4.32153 EndY=40.9231 EndZ=0
    g24: LineSegment StartX=-4.32153 StartY=40.9231 StartZ=0 EndX=-4.31865 EndY=40.2776 EndZ=0
    g25: LineSegment StartX=-4.31865 StartY=40.2776 StartZ=0 EndX=-3.71059 EndY=40.2803 EndZ=0
    g26: BSplineCurve PolesCount=3 KnotsCount=2 Degree=2 IsPeriodic=0
    g27: BSplineCurve PolesCount=3 KnotsCount=2 Degree=2 IsPeriodic=0
    g28: LineSegment StartX=-3.37182 StartY=39.0323 StartZ=0 EndX=-4.01945 EndY=39.0294 EndZ=0
    g29: BSplineCurve PolesCount=3 KnotsCount=2 Degree=2 IsPeriodic=0
    g30: BSplineCurve PolesCount=3 KnotsCount=2 Degree=2 IsPeriodic=0
    g31: LineSegment StartX=-4.62818 StartY=39.641 StartZ=0 EndX=-4.63442 EndY=41.0404 EndZ=0
    g32: BSplineCurve PolesCount=3 KnotsCount=2 Degree=2 IsPeriodic=0
    g33: BSplineCurve PolesCount=3 KnotsCount=2 Degree=2 IsPeriodic=0
    g34: LineSegment StartX=-4.45621 StartY=41.237 StartZ=0 EndX=-3.66489 EndY=41.2405 EndZ=0
    g35: BSplineCurve PolesCount=3 KnotsCount=2 Degree=2 IsPeriodic=0
    g36: BSplineCurve PolesCount=3 KnotsCount=2 Degree=2 IsPeriodic=0
    g37: BSplineCurve PolesCount=3 KnotsCount=2 Degree=2 IsPeriodic=0
    g38: BSplineCurve PolesCount=3 KnotsCount=2 Degree=2 IsPeriodic=0
    g39: LineSegment StartX=-3.66759 StartY=39.9785 StartZ=0 EndX=-4.3173 EndY=39.9756 EndZ=0
    g40: LineSegment StartX=-4.3173 StartY=39.9756 StartZ=0 EndX=-4.31559 EndY=39.5925 EndZ=0
    g41: BSplineCurve PolesCount=3 KnotsCount=2 Degree=2 IsPeriodic=0
    g42: BSplineCurve PolesCount=3 KnotsCount=2 Degree=2 IsPeriodic=0
    g43: LineSegment StartX=-4.01248 StartY=39.3335 StartZ=0 EndX=-3.37318 EndY=39.3364 EndZ=0
    g44: BSplineCurve PolesCount=3 KnotsCount=2 Degree=2 IsPeriodic=0
    g45: BSplineCurve PolesCount=3 KnotsCount=2 Degree=2 IsPeriodic=0
    g46: BSplineCurve PolesCount=3 KnotsCount=2 Degree=2 IsPeriodic=0
    g47: BSplineCurve PolesCount=3 KnotsCount=2 Degree=2 IsPeriodic=0
    g48: BSplineCurve PolesCount=3 KnotsCount=2 Degree=2 IsPeriodic=0
    g49: BSplineCurve PolesCount=3 KnotsCount=2 Degree=2 IsPeriodic=0
    g50: BSplineCurve PolesCount=3 KnotsCount=2 Degree=2 IsPeriodic=0
    g51: LineSegment StartX=-6.12197 StartY=39.3262 StartZ=0 EndX=-5.47643 EndY=39.329 EndZ=0
    g52: LineSegment StartX=-5.47643 StartY=39.329 StartZ=0 EndX=-5.48416 EndY=41.0616 EndZ=0
    g53: BSplineCurve PolesCount=3 KnotsCount=2 Degree=2 IsPeriodic=0
    g54: BSplineCurve PolesCount=3 KnotsCount=2 Degree=2 IsPeriodic=0
    g55: BSplineCurve PolesCount=3 KnotsCount=2 Degree=2 IsPeriodic=0
    g56: BSplineCurve PolesCount=3 KnotsCount=2 Degree=2 IsPeriodic=0
    g57: BSplineCurve PolesCount=3 KnotsCount=2 Degree=2 IsPeriodic=0
    g58: BSplineCurve PolesCount=3 KnotsCount=2 Degree=2 IsPeriodic=0
    g59: BSplineCurve PolesCount=3 KnotsCount=2 Degree=2 IsPeriodic=0
    g60: BSplineCurve PolesCount=3 KnotsCount=2 Degree=2 IsPeriodic=0
    g61: BSplineCurve PolesCount=3 KnotsCount=2 Degree=2 IsPeriodic=0
    g62: LineSegment StartX=-7.84415 StartY=39.3226 StartZ=0 EndX=-7.37144 EndY=39.3247 EndZ=0
    g63: LineSegment StartX=-7.37144 StartY=39.3247 StartZ=0 EndX=-7.3792 EndY=41.0636 EndZ=0
    g64: BSplineCurve PolesCount=3 KnotsCount=2 Degree=2 IsPeriodic=0
    g65: BSplineCurve PolesCount=3 KnotsCount=2 Degree=2 IsPeriodic=0
    g66: LineSegment StartX=-7.07927 StartY=41.0503 StartZ=0 EndX=-7.07157 EndY=39.3261 EndZ=0
    g67: LineSegment StartX=-7.07157 StartY=39.3261 StartZ=0 EndX=-6.91331 EndY=39.3268 EndZ=0
    g68: BSplineCurve PolesCount=3 KnotsCount=2 Degree=2 IsPeriodic=0
    g69: BSplineCurve PolesCount=3 KnotsCount=2 Degree=2 IsPeriodic=0
    g70: LineSegment StartX=-6.90991 StartY=39.0311 StartZ=0 EndX=-7.07025 EndY=39.0304 EndZ=0
    g71: LineSegment StartX=-7.07025 StartY=39.0304 StartZ=0 EndX=-7.06671 EndY=38.237 EndZ=0
    g72: BSplineCurve PolesCount=3 KnotsCount=2 Degree=2 IsPeriodic=0
    g73: LineSegment StartX=-8.68553 StartY=39.8041 StartZ=0 EndX=-8.68838 EndY=40.4434 EndZ=0
    g74: BSplineCurve PolesCount=3 KnotsCount=2 Degree=2 IsPeriodic=0
    g75: BSplineCurve PolesCount=3 KnotsCount=2 Degree=2 IsPeriodic=0
    g76: BSplineCurve PolesCount=3 KnotsCount=2 Degree=2 IsPeriodic=0
    g77: BSplineCurve PolesCount=3 KnotsCount=2 Degree=2 IsPeriodic=0
    g78: LineSegment StartX=-9.65642 StartY=40.3745 StartZ=0 EndX=-9.65405 EndY=39.8435 EndZ=0
    g79: BSplineCurve PolesCount=3 KnotsCount=2 Degree=2 IsPeriodic=0
    g80: BSplineCurve PolesCount=3 KnotsCount=2 Degree=2 IsPeriodic=0
    g81: BSplineCurve PolesCount=3 KnotsCount=2 Degree=2 IsPeriodic=0
    g82: BSplineCurve PolesCount=3 KnotsCount=2 Degree=2 IsPeriodic=0
    g83: BSplineCurve PolesCount=3 KnotsCount=2 Degree=2 IsPeriodic=0
    g84: LineSegment StartX=-9.94707 StartY=39.7089 StartZ=0 EndX=-9.95031 EndY=40.4336 EndZ=0
    g85: BSplineCurve PolesCount=3 KnotsCount=2 Degree=2 IsPeriodic=0
    g86: BSplineCurve PolesCount=3 KnotsCount=2 Degree=2 IsPeriodic=0
    g87: BSplineCurve PolesCount=3 KnotsCount=2 Degree=2 IsPeriodic=0
    g88: BSplineCurve PolesCount=3 KnotsCount=2 Degree=2 IsPeriodic=0
    g89: LineSegment StartX=-8.39053 StartY=40.4301 StartZ=0 EndX=-8.38749 EndY=39.7492 EndZ=0
    g90: BSplineCurve PolesCount=3 KnotsCount=2 Degree=2 IsPeriodic=0
    g91: BSplineCurve PolesCount=3 KnotsCount=2 Degree=2 IsPeriodic=0
    g92: BSplineCurve PolesCount=3 KnotsCount=2 Degree=2 IsPeriodic=0
    g93: BSplineCurve PolesCount=3 KnotsCount=2 Degree=2 IsPeriodic=0
    g94: LineSegment StartX=-10.784 StartY=39.6614 StartZ=0 EndX=-10.7879 EndY=40.5298 EndZ=0
    g95: BSplineCurve PolesCount=3 KnotsCount=2 Degree=2 IsPeriodic=0
    g96: BSplineCurve PolesCount=3 KnotsCount=2 Degree=2 IsPeriodic=0
    g97: LineSegment StartX=-11.1352 StartY=40.9052 StartZ=0 EndX=-11.7516 EndY=40.9024 EndZ=0
    g98: LineSegment StartX=-11.7516 StartY=40.9024 StartZ=0 EndX=-11.7445 EndY=39.3073 EndZ=0
    g99: LineSegment StartX=-11.7445 StartY=39.3073 StartZ=0 EndX=-11.1427 EndY=39.31 EndZ=0
    g100: BSplineCurve PolesCount=3 KnotsCount=2 Degree=2 IsPeriodic=0
    g101: BSplineCurve PolesCount=3 KnotsCount=2 Degree=2 IsPeriodic=0
    g102: BSplineCurve PolesCount=3 KnotsCount=2 Degree=2 IsPeriodic=0
    g103: BSplineCurve PolesCount=3 KnotsCount=2 Degree=2 IsPeriodic=0
    g104: BSplineCurve PolesCount=3 KnotsCount=2 Degree=2 IsPeriodic=0
    g105: BSplineCurve PolesCount=3 KnotsCount=2 Degree=2 IsPeriodic=0
    g106: BSplineCurve PolesCount=3 KnotsCount=2 Degree=2 IsPeriodic=0
    g107: BSplineCurve PolesCount=3 KnotsCount=2 Degree=2 IsPeriodic=0
    g108: BSplineCurve PolesCount=3 KnotsCount=2 Degree=2 IsPeriodic=0
    g109: BSplineCurve PolesCount=3 KnotsCount=2 Degree=2 IsPeriodic=0
    g110: LineSegment StartX=-11.7483 StartY=41.5563 StartZ=0 EndX=-11.7467 EndY=41.2044 EndZ=0
    g111: BSplineCurve PolesCount=3 KnotsCount=2 Degree=2 IsPeriodic=0
    g112: BSplineCurve PolesCount=3 KnotsCount=2 Degree=2 IsPeriodic=0
    g113: BSplineCurve PolesCount=3 KnotsCount=2 Degree=2 IsPeriodic=0
    g114: BSplineCurve PolesCount=3 KnotsCount=2 Degree=2 IsPeriodic=0
    g115: BSplineCurve PolesCount=3 KnotsCount=2 Degree=2 IsPeriodic=0
    g116: BSplineCurve PolesCount=3 KnotsCount=2 Degree=2 IsPeriodic=0
    g117: BSplineCurve PolesCount=3 KnotsCount=2 Degree=2 IsPeriodic=0
    g118: BSplineCurve PolesCount=3 KnotsCount=2 Degree=2 IsPeriodic=0
    g119: BSplineCurve PolesCount=3 KnotsCount=2 Degree=2 IsPeriodic=0
    g120: BSplineCurve PolesCount=3 KnotsCount=2 Degree=2 IsPeriodic=0
    g121: BSplineCurve PolesCount=3 KnotsCount=2 Degree=2 IsPeriodic=0
    g122: BSplineCurve PolesCount=3 KnotsCount=2 Degree=2 IsPeriodic=0
    g123: BSplineCurve PolesCount=3 KnotsCount=2 Degree=2 IsPeriodic=0
    g124: LineSegment StartX=-13.5833 StartY=39.2928 StartZ=0 EndX=-12.9377 EndY=39.2957 EndZ=0
    g125: LineSegment StartX=-12.9377 StartY=39.2957 StartZ=0 EndX=-12.9454 EndY=41.0283 EndZ=0
    g126: BSplineCurve PolesCount=3 KnotsCount=2 Degree=2 IsPeriodic=0
    g127: BSplineCurve PolesCount=3 KnotsCount=2 Degree=2 IsPeriodic=0
    g128: BSplineCurve PolesCount=3 KnotsCount=2 Degree=2 IsPeriodic=0
    g129: BSplineCurve PolesCount=3 KnotsCount=2 Degree=2 IsPeriodic=0
    g130: BSplineCurve PolesCount=3 KnotsCount=2 Degree=2 IsPeriodic=0
    g131: BSplineCurve PolesCount=3 KnotsCount=2 Degree=2 IsPeriodic=0
    g132: BSplineCurve PolesCount=3 KnotsCount=2 Degree=2 IsPeriodic=0
    g133: LineSegment StartX=-14.9356 StartY=40.8757 StartZ=0 EndX=-15.5728 EndY=40.8729 EndZ=0
    g134: LineSegment StartX=-15.5728 StartY=40.8729 StartZ=0 EndX=-15.5699 EndY=40.2273 EndZ=0
    g135: LineSegment StartX=-15.5699 StartY=40.2273 StartZ=0 EndX=-14.9619 EndY=40.23 EndZ=0
    g136: BSplineCurve PolesCount=3 KnotsCount=2 Degree=2 IsPeriodic=0
    g137: BSplineCurve PolesCount=3 KnotsCount=2 Degree=2 IsPeriodic=0
    g138: LineSegment StartX=-14.6231 StartY=38.9821 StartZ=0 EndX=-15.2707 EndY=38.9792 EndZ=0
    g139: BSplineCurve PolesCount=3 KnotsCount=2 Degree=2 IsPeriodic=0
    g140: BSplineCurve PolesCount=3 KnotsCount=2 Degree=2 IsPeriodic=0
    g141: LineSegment StartX=-15.8795 StartY=39.5908 StartZ=0 EndX=-15.8857 EndY=40.9902 EndZ=0
    g142: BSplineCurve PolesCount=3 KnotsCount=2 Degree=2 IsPeriodic=0
    g143: BSplineCurve PolesCount=3 KnotsCount=2 Degree=2 IsPeriodic=0
    g144: LineSegment StartX=-15.7075 StartY=41.1867 StartZ=0 EndX=-14.9162 EndY=41.1903 EndZ=0
    g145: BSplineCurve PolesCount=3 KnotsCount=2 Degree=2 IsPeriodic=0
    g146: BSplineCurve PolesCount=3 KnotsCount=2 Degree=2 IsPeriodic=0
    g147: BSplineCurve PolesCount=3 KnotsCount=2 Degree=2 IsPeriodic=0
    g148: BSplineCurve PolesCount=3 KnotsCount=2 Degree=2 IsPeriodic=0
    g149: LineSegment StartX=-14.9189 StartY=39.9283 StartZ=0 EndX=-15.5686 EndY=39.9254 EndZ=0
    g150: LineSegment StartX=-15.5686 StartY=39.9254 StartZ=0 EndX=-15.5669 EndY=39.5422 EndZ=0
    g151: BSplineCurve PolesCount=3 KnotsCount=2 Degree=2 IsPeriodic=0
    g152: BSplineCurve PolesCount=3 KnotsCount=2 Degree=2 IsPeriodic=0
    g153: LineSegment StartX=-15.2638 StartY=39.2833 StartZ=0 EndX=-14.6245 EndY=39.2861 EndZ=0
    g154: BSplineCurve PolesCount=3 KnotsCount=2 Degree=2 IsPeriodic=0
    g155: BSplineCurve PolesCount=3 KnotsCount=2 Degree=2 IsPeriodic=0
    g156: LineSegment StartX=-17.7371 StartY=40.5404 StartZ=0 EndX=-17.733 EndY=39.6283 EndZ=0
    g157: BSplineCurve PolesCount=3 KnotsCount=2 Degree=2 IsPeriodic=0
    g158: BSplineCurve PolesCount=3 KnotsCount=2 Degree=2 IsPeriodic=0
    g159: LineSegment StartX=-17.4129 StartY=39.2882 StartZ=0 EndX=-16.7673 EndY=39.2911 EndZ=0
    g160: LineSegment StartX=-16.7673 StartY=39.2911 StartZ=0 EndX=-16.7744 EndY=40.8821 EndZ=0
    g161: LineSegment StartX=-16.7744 StartY=40.8821 StartZ=0 EndX=-17.4429 EndY=40.8791 EndZ=0
    g162: BSplineCurve PolesCount=3 KnotsCount=2 Degree=2 IsPeriodic=0
    g163: BSplineCurve PolesCount=3 KnotsCount=2 Degree=2 IsPeriodic=0
    g164: BSplineCurve PolesCount=3 KnotsCount=2 Degree=2 IsPeriodic=0
    g165: BSplineCurve PolesCount=3 KnotsCount=2 Degree=2 IsPeriodic=0
    g166: BSplineCurve PolesCount=3 KnotsCount=2 Degree=2 IsPeriodic=0
    g167: BSplineCurve PolesCount=3 KnotsCount=2 Degree=2 IsPeriodic=0
    g168: BSplineCurve PolesCount=3 KnotsCount=2 Degree=2 IsPeriodic=0
    g169: LineSegment StartX=-17.4588 StartY=41.1789 StartZ=0 EndX=-16.7758 EndY=41.182 EndZ=0
    g170: LineSegment StartX=-16.7758 StartY=41.182 StartZ=0 EndX=-16.7792 EndY=41.942 EndZ=0
    g171: BSplineCurve PolesCount=3 KnotsCount=2 Degree=2 IsPeriodic=0
    g172: BSplineCurve PolesCount=3 KnotsCount=2 Degree=2 IsPeriodic=0
    g173: BSplineCurve PolesCount=3 KnotsCount=2 Degree=2 IsPeriodic=0
    g174: BSplineCurve PolesCount=3 KnotsCount=2 Degree=2 IsPeriodic=0
    g175: BSplineCurve PolesCount=3 KnotsCount=2 Degree=2 IsPeriodic=0
    g176: LineSegment StartX=-18.924 StartY=38.1945 StartZ=0 EndX=-18.9275 EndY=38.9649 EndZ=0
    g177: LineSegment StartX=-18.9275 StartY=38.9649 StartZ=0 EndX=-19.573 EndY=38.9621 EndZ=0
    g178: BSplineCurve PolesCount=3 KnotsCount=2 Degree=2 IsPeriodic=0
    g179: BSplineCurve PolesCount=3 KnotsCount=2 Degree=2 IsPeriodic=0
    g180: LineSegment StartX=-20.1901 StartY=39.582 StartZ=0 EndX=-20.1964 EndY=40.9918 EndZ=0
    g181: BSplineCurve PolesCount=3 KnotsCount=2 Degree=2 IsPeriodic=0
    g182: BSplineCurve PolesCount=3 KnotsCount=2 Degree=2 IsPeriodic=0
    g183: LineSegment StartX=-19.8986 StartY=40.9889 StartZ=0 EndX=-19.8925 EndY=39.6187 EndZ=0
    g184: BSplineCurve PolesCount=3 KnotsCount=2 Degree=2 IsPeriodic=0
    g185: LineSegment StartX=-19.5244 StartY=39.2622 StartZ=0 EndX=-18.9288 EndY=39.2648 EndZ=0
    g186: LineSegment StartX=-18.9288 StartY=39.2648 StartZ=0 EndX=-18.9365 EndY=40.9911 EndZ=0
    g187: BSplineCurve PolesCount=3 KnotsCount=2 Degree=2 IsPeriodic=0
    g188: BSplineCurve PolesCount=3 KnotsCount=2 Degree=2 IsPeriodic=0
    g189: LineSegment StartX=-18.6324 StartY=40.9821 StartZ=0 EndX=-18.62 EndY=38.2041 EndZ=0
    g190: LineSegment StartX=-21.0453 StartY=39.9051 StartZ=0 EndX=-22.0012 EndY=39.9008 EndZ=0
    g191: BSplineCurve PolesCount=3 KnotsCount=2 Degree=2 IsPeriodic=0
    g192: BSplineCurve PolesCount=3 KnotsCount=2 Degree=2 IsPeriodic=0
    g193: BSplineCurve PolesCount=3 KnotsCount=2 Degree=2 IsPeriodic=0
    g194: BSplineCurve PolesCount=3 KnotsCount=2 Degree=2 IsPeriodic=0
    g195: BSplineCurve PolesCount=3 KnotsCount=2 Degree=2 IsPeriodic=0
    g196: BSplineCurve PolesCount=3 KnotsCount=2 Degree=2 IsPeriodic=0
    g197: BSplineCurve PolesCount=3 KnotsCount=2 Degree=2 IsPeriodic=0
    g198: BSplineCurve PolesCount=3 KnotsCount=2 Degree=2 IsPeriodic=0
    g199: LineSegment StartX=-22.2978 StartY=39.6496 StartZ=0 EndX=-22.2996 EndY=40.0453 EndZ=0
    g200: BSplineCurve PolesCount=3 KnotsCount=2 Degree=2 IsPeriodic=0
    g201: LineSegment StartX=-22.1608 StartY=40.1958 StartZ=0 EndX=-21.0425 EndY=40.2008 EndZ=0
    g202: LineSegment StartX=-21.0425 StartY=40.2008 StartZ=0 EndX=-21.0437 EndY=40.4757 EndZ=0
    g203: BSplineCurve PolesCount=3 KnotsCount=2 Degree=2 IsPeriodic=0
    g204: LineSegment StartX=-21.3703 StartY=40.8574 StartZ=0 EndX=-22.1262 EndY=40.854 EndZ=0
    g205: BSplineCurve PolesCount=3 KnotsCount=2 Degree=2 IsPeriodic=0
    g206: BSplineCurve PolesCount=3 KnotsCount=2 Degree=2 IsPeriodic=0
    g207: LineSegment StartX=-22.1297 StartY=41.1581 StartZ=0 EndX=-21.3633 EndY=41.1615 EndZ=0
    g208: BSplineCurve PolesCount=3 KnotsCount=2 Degree=2 IsPeriodic=0
    g209: BSplineCurve PolesCount=3 KnotsCount=2 Degree=2 IsPeriodic=0
    g210: BSplineCurve PolesCount=3 KnotsCount=2 Degree=2 IsPeriodic=0
    g211: BSplineCurve PolesCount=3 KnotsCount=2 Degree=2 IsPeriodic=0
    g212: BSplineCurve PolesCount=3 KnotsCount=2 Degree=2 IsPeriodic=0
    g213: BSplineCurve PolesCount=3 KnotsCount=2 Degree=2 IsPeriodic=0
    g214: BSplineCurve PolesCount=3 KnotsCount=2 Degree=2 IsPeriodic=0
    g215: BSplineCurve PolesCount=3 KnotsCount=2 Degree=2 IsPeriodic=0
    g216: BSplineCurve PolesCount=3 KnotsCount=2 Degree=2 IsPeriodic=0
    g217: BSplineCurve PolesCount=3 KnotsCount=2 Degree=2 IsPeriodic=0
    g218: LineSegment StartX=-23.7975 StartY=39.2472 StartZ=0 EndX=-23.152 EndY=39.2501 EndZ=0
    g219: LineSegment StartX=-23.152 StartY=39.2501 StartZ=0 EndX=-23.1597 EndY=40.9827 EndZ=0
    g220: BSplineCurve PolesCount=3 KnotsCount=2 Degree=2 IsPeriodic=0
    g221: BSplineCurve PolesCount=3 KnotsCount=2 Degree=2 IsPeriodic=0
    g222: BSplineCurve PolesCount=3 KnotsCount=2 Degree=2 IsPeriodic=0
    g223: LineSegment StartX=-27.4766 StartY=40.5094 StartZ=0 EndX=-28.2677 EndY=38.1236 EndZ=0
    g224: BSplineCurve PolesCount=3 KnotsCount=2 Degree=2 IsPeriodic=0
    g225: BSplineCurve PolesCount=3 KnotsCount=2 Degree=2 IsPeriodic=0
    g226: BSplineCurve PolesCount=3 KnotsCount=2 Degree=2 IsPeriodic=0
    g227: LineSegment StartX=-28.5534 StartY=38.2264 StartZ=0 EndX=-27.6474 EndY=40.9918 EndZ=0
    g228: BSplineCurve PolesCount=3 KnotsCount=2 Degree=2 IsPeriodic=0
    g229: BSplineCurve PolesCount=3 KnotsCount=2 Degree=2 IsPeriodic=0
    g230: LineSegment StartX=-27.3351 StartY=40.9974 StartZ=0 EndX=-26.3793 EndY=38.207 EndZ=0
    g231: BSplineCurve PolesCount=3 KnotsCount=2 Degree=2 IsPeriodic=0
    g232: BSplineCurve PolesCount=3 KnotsCount=2 Degree=2 IsPeriodic=0
    g233: BSplineCurve PolesCount=3 KnotsCount=2 Degree=2 IsPeriodic=0
    g234: LineSegment StartX=-26.6747 StartY=38.1474 StartZ=0 EndX=-27.4766 EndY=40.5094 EndZ=0
    g235: BSplineCurve PolesCount=3 KnotsCount=2 Degree=2 IsPeriodic=0
    g236: BSplineCurve PolesCount=3 KnotsCount=2 Degree=2 IsPeriodic=0
    g237: BSplineCurve PolesCount=3 KnotsCount=2 Degree=2 IsPeriodic=0
    g238: BSplineCurve PolesCount=3 KnotsCount=2 Degree=2 IsPeriodic=0
    g239: BSplineCurve PolesCount=3 KnotsCount=2 Degree=2 IsPeriodic=0
    g240: BSplineCurve PolesCount=3 KnotsCount=2 Degree=2 IsPeriodic=0
    g241: BSplineCurve PolesCount=3 KnotsCount=2 Degree=2 IsPeriodic=0
    g242: BSplineCurve PolesCount=3 KnotsCount=2 Degree=2 IsPeriodic=0
    g243: BSplineCurve PolesCount=3 KnotsCount=2 Degree=2 IsPeriodic=0
    g244: BSplineCurve PolesCount=3 KnotsCount=2 Degree=2 IsPeriodic=0
    g245: BSplineCurve PolesCount=3 KnotsCount=2 Degree=2 IsPeriodic=0
    g246: BSplineCurve PolesCount=3 KnotsCount=2 Degree=2 IsPeriodic=0
    g247: BSplineCurve PolesCount=3 KnotsCount=2 Degree=2 IsPeriodic=0
    g248: BSplineCurve PolesCount=3 KnotsCount=2 Degree=2 IsPeriodic=0
    g249: LineSegment StartX=-30.2682 StartY=40.3033 StartZ=0 EndX=-30.267 EndY=40.0326 EndZ=0
    g250: BSplineCurve PolesCount=3 KnotsCount=2 Degree=2 IsPeriodic=0
    g251: BSplineCurve PolesCount=3 KnotsCount=2 Degree=2 IsPeriodic=0
    g252: LineSegment StartX=-29.815 StartY=39.5307 StartZ=0 EndX=-29.4985 EndY=39.5321 EndZ=0
    g253: BSplineCurve PolesCount=3 KnotsCount=2 Degree=2 IsPeriodic=0
    g254: BSplineCurve PolesCount=3 KnotsCount=2 Degree=2 IsPeriodic=0
    g255: LineSegment StartX=-29.4992 StartY=39.2384 StartZ=0 EndX=-29.7803 EndY=39.2372 EndZ=0
    g256: BSplineCurve PolesCount=3 KnotsCount=2 Degree=2 IsPeriodic=0
    g257: BSplineCurve PolesCount=3 KnotsCount=2 Degree=2 IsPeriodic=0
    g258: BSplineCurve PolesCount=3 KnotsCount=2 Degree=2 IsPeriodic=0
    g259: BSplineCurve PolesCount=3 KnotsCount=2 Degree=2 IsPeriodic=0
    g260: LineSegment StartX=-29.8073 StartY=38.2729 StartZ=0 EndX=-29.1909 EndY=38.2756 EndZ=0
    g261: BSplineCurve PolesCount=3 KnotsCount=2 Degree=2 IsPeriodic=0
    g262: BSplineCurve PolesCount=3 KnotsCount=2 Degree=2 IsPeriodic=0
  constraints (1):
    c: T21(g0,g1,g2)
FEATURE [PartDesign::Pocket] Pocket017
  BaseFeature = -> Pocket016
  Direction = (0,1,-2e-16)
  Length = 2
  Length2 = 5
  Profile = -> Sketch041
  ReferenceAxis = -> Sketch041 [N_Axis]
  Refine = true
  SideType = 0
  Suppressed = false
  Type = 0
  Type2 = 0
FEATURE [Sketcher::SketchObject] Sketch042
  ArcFitTolerance = 1e-06
  AttachmentSupport = -> [Pocket017]
  ExternalGeometry = -> [Sketch037]
  ExternalTypes = [0,0]
  FullyConstrained = true
  MakeInternals = false
  MapMode = 5
  Placement = pos=(0,0,43.3) rot=(0,0,1;0rad)
  _ExternalGeoVersion = 0
  sketch-geometry (2):
    g0: Circle CenterX=-31.8 CenterY=-2.6 CenterZ=0 NormalX=0 NormalY=0 NormalZ=1 AngleXU=0 Radius=2.25
    g1: Circle CenterX=-0.2 CenterY=-2.6 CenterZ=0 NormalX=0 NormalY=0 NormalZ=1 AngleXU=0 Radius=2.25
  constraints (4):
    c: Coincident(g0,g-3)
    c: Coincident(g1,g-4)
    c: Equal(g1,g0)
    c: Diameter(g0) = 4.5
FEATURE [PartDesign::Pocket] Pocket018
  BaseFeature = -> Pocket017
  Direction = (0,0,-1)
  Length = 1
  Length2 = 5
  Profile = -> Sketch042
  ReferenceAxis = -> Sketch042 [N_Axis]
  Refine = true
  SideType = 0
  Suppressed = false
  Type = 0
  Type2 = 0
FEATURE [PartDesign::Body] Body005  label="CartographerV3_HeatSetInserts"
  AllowCompound = true
  Group = -> [Sketch034,Sketch035,Pad014,Pad015,Sketch036,MirroredSketch004,Clone2D005,Pocket014,AdditiveLoft008,Chamfer006,Sketch037,Pocket015,Sketch038,Sketch039,AdditiveLoft009,Sketch040,Pocket016,Sketch041,Pocket017,Sketch042,Pocket018]
  Origin = -> Origin014
  Placement = pos=(0,0,0) rot=(0,0,1;6.13955rad)
  Tip = -> Pocket018
FEATURE [App::Point] Origin017  label="Origin019"
  Role = Origin
FEATURE [Sketcher::SketchObject] Sketch044
  ArcFitTolerance = 1e-06
  AttachmentOffset = pos=(-16,-2,43.3) rot=(0,0,1;0rad)
  AttachmentSupport = -> [Origin016]
  ExternalTypes = [0,0]
  FullyConstrained = true
  MakeInternals = false
  MapMode = 5
  Placement = pos=(-16,-2,43.3) rot=(0,0,1;0rad)
  _ExternalGeoVersion = 0
  sketch-geometry (4):
    g0: ArcOfCircle CenterX=-15.8 CenterY=0 CenterZ=0 NormalX=0 NormalY=0 NormalZ=1 AngleXU=0 Radius=4 StartAngle=0.125328 EndAngle=4.71239
    g1: ArcOfCircle CenterX=15.8 CenterY=0 CenterZ=0 NormalX=0 NormalY=0 NormalZ=1 AngleXU=0 Radius=4 StartAngle=4.71239 EndAngle=9.29945
    g2: LineSegment StartX=-15.8 StartY=-4 StartZ=0 EndX=15.8 EndY=-4 EndZ=0
    g3: LineSegment StartX=-11.8314 StartY=0.5 StartZ=0 EndX=11.8314 EndY=0.5 EndZ=0
  constraints (12):
    c: DistanceX(g0,g1) = 31.6
    c: Vertical(g2,g1)
    c: Symmetric(g0,g1,g-2)
    c: Symmetric(g2,g2,g-2)
    c: Horizontal(g3)
    c: PointOnObject(g0,g-1)
    c: DistanceY(g2,g3) = 4.5
    c: DistanceY(g2,g0) = 4
    c: Coincident(g3,g1)
    c: Coincident(g1,g2)
    c: Coincident(g3,g0)
    c: Coincident(g0,g2)
FEATURE [PartDesign::Pad] Pad016
  Direction = (0,0,1)
  Length = 22
  Length2 = 10
  Profile = -> Sketch044
  ReferenceAxis = -> Sketch044 [N_Axis]
  Refine = true
  Reversed = true
  SideType = 0
  Suppressed = false
  Type = 0
  Type2 = 0
FEATURE [Sketcher::SketchObject] Sketch045
  ArcFitTolerance = 1e-06
  AttachmentSupport = -> [Origin016]
  ExternalTypes = [0]
  FullyConstrained = true
  MakeInternals = false
  MapMode = 5
  _ExternalGeoVersion = 0
  expr: Constraints[11] = 5 + 3.5 / 2
  sketch-geometry (6):
    g0: LineSegment StartX=-13.5 StartY=-5.575 StartZ=0 EndX=13.5 EndY=-5.575 EndZ=0
    g1: LineSegment StartX=13.5 StartY=-5.575 StartZ=0 EndX=13.5 EndY=5.575 EndZ=0
    g2: Circle CenterX=-9 CenterY=1.175 CenterZ=0 NormalX=0 NormalY=0 NormalZ=1 AngleXU=0 Radius=1.75
    g3: Circle CenterX=9 CenterY=1.175 CenterZ=0 NormalX=0 NormalY=0 NormalZ=1 AngleXU=0 Radius=1.75
    g4: LineSegment StartX=-13.5 StartY=-5.575 StartZ=0 EndX=-13.5 EndY=5.575 EndZ=0
    g5: LineSegment StartX=-13.5 StartY=5.575 StartZ=0 EndX=13.5 EndY=5.575 EndZ=0
  constraints (16):
    c: Equal(g3,g2)
    c: Diameter(g3) = 3.5
    c: Symmetric(g2,g3,g-2)
    c: Coincident(g4,g0)
    c: Vertical(g4)
    c: Coincident(g5,g4)
    c: Coincident(g5,g1)
    c: Horizontal(g5)
    c: DistanceY(g4,g4) = 11.15
    c: Symmetric(g4,g0,g-1)
    c: DistanceX(g5,g5) = 27
    c: DistanceY(g0,g2) = 6.75
    c: DistanceX(g2,g3) = 18
    c: Horizontal(g0)
    c: Vertical(g1)
    c: Coincident(g1,g0)
FEATURE [PartDesign::Pad] Pad017
  BaseFeature = -> Pad016
  Direction = (0,0,1)
  Length = 3
  Length2 = 10
  Profile = -> Sketch045
  ReferenceAxis = -> Sketch045 [N_Axis]
  Refine = true
  SideType = 0
  Suppressed = false
  Type = 0
  Type2 = 0
FEATURE [Sketcher::SketchObject] MirroredSketch005
  ArcFitTolerance = 1e-06
  AttachmentOffset = pos=(14,-18,0) rot=(0,0,1;0rad)
  AttachmentSupport = -> [Pad017]
  ExternalTypes = [0]
  FullyConstrained = false
  MakeInternals = false
  MapMode = 5
  Placement = pos=(-14,-1.5,-18) rot=(0,0.707107,0.707107;3.14159rad)
  _ExternalGeoVersion = 0
  sketch-geometry (160):
    g0: BSplineCurve PolesCount=4 KnotsCount=2 Degree=3 IsPeriodic=0
    g1: BSplineCurve PolesCount=4 KnotsCount=2 Degree=3 IsPeriodic=0
    g2: BSplineCurve PolesCount=4 KnotsCount=2 Degree=3 IsPeriodic=0
    g3: BSplineCurve PolesCount=4 KnotsCount=2 Degree=3 IsPeriodic=0
    g4: BSplineCurve PolesCount=4 KnotsCount=2 Degree=3 IsPeriodic=0
    g5: BSplineCurve PolesCount=4 KnotsCount=2 Degree=3 IsPeriodic=0
    g6: BSplineCurve PolesCount=4 KnotsCount=2 Degree=3 IsPeriodic=0
    g7: BSplineCurve PolesCount=4 KnotsCount=2 Degree=3 IsPeriodic=0
    g8: BSplineCurve PolesCount=4 KnotsCount=2 Degree=3 IsPeriodic=0
    g9: BSplineCurve PolesCount=4 KnotsCount=2 Degree=3 IsPeriodic=0
    g10: BSplineCurve PolesCount=4 KnotsCount=2 Degree=3 IsPeriodic=0
    g11: BSplineCurve PolesCount=4 KnotsCount=2 Degree=3 IsPeriodic=0
    g12: BSplineCurve PolesCount=4 KnotsCount=2 Degree=3 IsPeriodic=0
    g13: BSplineCurve PolesCount=4 KnotsCount=2 Degree=3 IsPeriodic=0
    g14: BSplineCurve PolesCount=4 KnotsCount=2 Degree=3 IsPeriodic=0
    g15: BSplineCurve PolesCount=4 KnotsCount=2 Degree=3 IsPeriodic=0
    g16: BSplineCurve PolesCount=4 KnotsCount=2 Degree=3 IsPeriodic=0
    g17: BSplineCurve PolesCount=4 KnotsCount=2 Degree=3 IsPeriodic=0
    g18: BSplineCurve PolesCount=4 KnotsCount=2 Degree=3 IsPeriodic=0
    g19: BSplineCurve PolesCount=4 KnotsCount=2 Degree=3 IsPeriodic=0
    g20: BSplineCurve PolesCount=4 KnotsCount=2 Degree=3 IsPeriodic=0
    g21: BSplineCurve PolesCount=4 KnotsCount=2 Degree=3 IsPeriodic=0
    g22: BSplineCurve PolesCount=4 KnotsCount=2 Degree=3 IsPeriodic=0
    g23: BSplineCurve PolesCount=4 KnotsCount=2 Degree=3 IsPeriodic=0
    g24: BSplineCurve PolesCount=4 KnotsCount=2 Degree=3 IsPeriodic=0
    g25: BSplineCurve PolesCount=4 KnotsCount=2 Degree=3 IsPeriodic=0
    g26: BSplineCurve PolesCount=4 KnotsCount=2 Degree=3 IsPeriodic=0
    g27: BSplineCurve PolesCount=4 KnotsCount=2 Degree=3 IsPeriodic=0
    g28: BSplineCurve PolesCount=4 KnotsCount=2 Degree=3 IsPeriodic=0
    g29: BSplineCurve PolesCount=4 KnotsCount=2 Degree=3 IsPeriodic=0
    g30: BSplineCurve PolesCount=4 KnotsCount=2 Degree=3 IsPeriodic=0
    g31: BSplineCurve PolesCount=4 KnotsCount=2 Degree=3 IsPeriodic=0
    g32: BSplineCurve PolesCount=4 KnotsCount=2 Degree=3 IsPeriodic=0
    g33: BSplineCurve PolesCount=4 KnotsCount=2 Degree=3 IsPeriodic=0
    g34: BSplineCurve PolesCount=4 KnotsCount=2 Degree=3 IsPeriodic=0
    g35: BSplineCurve PolesCount=4 KnotsCount=2 Degree=3 IsPeriodic=0
    g36: BSplineCurve PolesCount=4 KnotsCount=2 Degree=3 IsPeriodic=0
    g37: BSplineCurve PolesCount=4 KnotsCount=2 Degree=3 IsPeriodic=0
    g38: BSplineCurve PolesCount=4 KnotsCount=2 Degree=3 IsPeriodic=0
    g39: BSplineCurve PolesCount=4 KnotsCount=2 Degree=3 IsPeriodic=0
    g40: BSplineCurve PolesCount=4 KnotsCount=2 Degree=3 IsPeriodic=0
    g41: BSplineCurve PolesCount=4 KnotsCount=2 Degree=3 IsPeriodic=0
    g42: BSplineCurve PolesCount=4 KnotsCount=2 Degree=3 IsPeriodic=0
    g43: BSplineCurve PolesCount=4 KnotsCount=2 Degree=3 IsPeriodic=0
    g44: BSplineCurve PolesCount=4 KnotsCount=2 Degree=3 IsPeriodic=0
    g45: BSplineCurve PolesCount=4 KnotsCount=2 Degree=3 IsPeriodic=0
    g46: BSplineCurve PolesCount=4 KnotsCount=2 Degree=3 IsPeriodic=0
    g47: BSplineCurve PolesCount=4 KnotsCount=2 Degree=3 IsPeriodic=0
    g48: BSplineCurve PolesCount=4 KnotsCount=2 Degree=3 IsPeriodic=0
    g49: BSplineCurve PolesCount=4 KnotsCount=2 Degree=3 IsPeriodic=0
    g50: BSplineCurve PolesCount=4 KnotsCount=2 Degree=3 IsPeriodic=0
    g51: BSplineCurve PolesCount=4 KnotsCount=2 Degree=3 IsPeriodic=0
    g52: BSplineCurve PolesCount=4 KnotsCount=2 Degree=3 IsPeriodic=0
    g53: BSplineCurve PolesCount=4 KnotsCount=2 Degree=3 IsPeriodic=0
    g54: BSplineCurve PolesCount=4 KnotsCount=2 Degree=3 IsPeriodic=0
    g55: BSplineCurve PolesCount=4 KnotsCount=2 Degree=3 IsPeriodic=0
    g56: BSplineCurve PolesCount=4 KnotsCount=2 Degree=3 IsPeriodic=0
    g57: BSplineCurve PolesCount=4 KnotsCount=2 Degree=3 IsPeriodic=0
    g58: BSplineCurve PolesCount=4 KnotsCount=2 Degree=3 IsPeriodic=0
    g59: BSplineCurve PolesCount=4 KnotsCount=2 Degree=3 IsPeriodic=0
    g60: BSplineCurve PolesCount=4 KnotsCount=2 Degree=3 IsPeriodic=0
    g61: BSplineCurve PolesCount=4 KnotsCount=2 Degree=3 IsPeriodic=0
    g62: BSplineCurve PolesCount=4 KnotsCount=2 Degree=3 IsPeriodic=0
    g63: BSplineCurve PolesCount=4 KnotsCount=2 Degree=3 IsPeriodic=0
    g64: BSplineCurve PolesCount=4 KnotsCount=2 Degree=3 IsPeriodic=0
    g65: BSplineCurve PolesCount=4 KnotsCount=2 Degree=3 IsPeriodic=0
    g66: BSplineCurve PolesCount=4 KnotsCount=2 Degree=3 IsPeriodic=0
    g67: BSplineCurve PolesCount=4 KnotsCount=2 Degree=3 IsPeriodic=0
    g68: BSplineCurve PolesCount=4 KnotsCount=2 Degree=3 IsPeriodic=0
    g69: BSplineCurve PolesCount=4 KnotsCount=2 Degree=3 IsPeriodic=0
    g70: BSplineCurve PolesCount=4 KnotsCount=2 Degree=3 IsPeriodic=0
    g71: BSplineCurve PolesCount=4 KnotsCount=2 Degree=3 IsPeriodic=0
    g72: BSplineCurve PolesCount=4 KnotsCount=2 Degree=3 IsPeriodic=0
    g73: BSplineCurve PolesCount=4 KnotsCount=2 Degree=3 IsPeriodic=0
    g74: BSplineCurve PolesCount=4 KnotsCount=2 Degree=3 IsPeriodic=0
    g75: BSplineCurve PolesCount=4 KnotsCount=2 Degree=3 IsPeriodic=0
    g76: BSplineCurve PolesCount=4 KnotsCount=2 Degree=3 IsPeriodic=0
    g77: BSplineCurve PolesCount=4 KnotsCount=2 Degree=3 IsPeriodic=0
    g78: BSplineCurve PolesCount=4 KnotsCount=2 Degree=3 IsPeriodic=0
    g79: BSplineCurve PolesCount=4 KnotsCount=2 Degree=3 IsPeriodic=0
    g80: BSplineCurve PolesCount=4 KnotsCount=2 Degree=3 IsPeriodic=0
    g81: BSplineCurve PolesCount=4 KnotsCount=2 Degree=3 IsPeriodic=0
    g82: BSplineCurve PolesCount=4 KnotsCount=2 Degree=3 IsPeriodic=0
    g83: BSplineCurve PolesCount=4 KnotsCount=2 Degree=3 IsPeriodic=0
    g84: BSplineCurve PolesCount=4 KnotsCount=2 Degree=3 IsPeriodic=0
    g85: BSplineCurve PolesCount=4 KnotsCount=2 Degree=3 IsPeriodic=0
    g86: BSplineCurve PolesCount=4 KnotsCount=2 Degree=3 IsPeriodic=0
    g87: BSplineCurve PolesCount=4 KnotsCount=2 Degree=3 IsPeriodic=0
    g88: BSplineCurve PolesCount=4 KnotsCount=2 Degree=3 IsPeriodic=0
    g89: BSplineCurve PolesCount=4 KnotsCount=2 Degree=3 IsPeriodic=0
    g90: BSplineCurve PolesCount=4 KnotsCount=2 Degree=3 IsPeriodic=0
    g91: BSplineCurve PolesCount=4 KnotsCount=2 Degree=3 IsPeriodic=0
    g92: BSplineCurve PolesCount=4 KnotsCount=2 Degree=3 IsPeriodic=0
    g93: BSplineCurve PolesCount=4 KnotsCount=2 Degree=3 IsPeriodic=0
    g94: BSplineCurve PolesCount=4 KnotsCount=2 Degree=3 IsPeriodic=0
    g95: BSplineCurve PolesCount=4 KnotsCount=2 Degree=3 IsPeriodic=0
    g96: BSplineCurve PolesCount=4 KnotsCount=2 Degree=3 IsPeriodic=0
    g97: BSplineCurve PolesCount=4 KnotsCount=2 Degree=3 IsPeriodic=0
    g98: BSplineCurve PolesCount=4 KnotsCount=2 Degree=3 IsPeriodic=0
    g99: BSplineCurve PolesCount=4 KnotsCount=2 Degree=3 IsPeriodic=0
    g100: BSplineCurve PolesCount=4 KnotsCount=2 Degree=3 IsPeriodic=0
    g101: BSplineCurve PolesCount=4 KnotsCount=2 Degree=3 IsPeriodic=0
    g102: BSplineCurve PolesCount=4 KnotsCount=2 Degree=3 IsPeriodic=0
    g103: BSplineCurve PolesCount=4 KnotsCount=2 Degree=3 IsPeriodic=0
    g104: BSplineCurve PolesCount=4 KnotsCount=2 Degree=3 IsPeriodic=0
    g105: BSplineCurve PolesCount=2 KnotsCount=2 Degree=1 IsPeriodic=0
    g106: BSplineCurve PolesCount=4 KnotsCount=2 Degree=3 IsPeriodic=0
    g107: BSplineCurve PolesCount=4 KnotsCount=2 Degree=3 IsPeriodic=0
    g108: BSplineCurve PolesCount=4 KnotsCount=2 Degree=3 IsPeriodic=0
    g109: BSplineCurve PolesCount=4 KnotsCount=2 Degree=3 IsPeriodic=0
    g110: BSplineCurve PolesCount=4 KnotsCount=2 Degree=3 IsPeriodic=0
    g111: BSplineCurve PolesCount=4 KnotsCount=2 Degree=3 IsPeriodic=0
    g112: BSplineCurve PolesCount=4 KnotsCount=2 Degree=3 IsPeriodic=0
    g113: BSplineCurve PolesCount=4 KnotsCount=2 Degree=3 IsPeriodic=0
    g114: BSplineCurve PolesCount=4 KnotsCount=2 Degree=3 IsPeriodic=0
    g115: BSplineCurve PolesCount=4 KnotsCount=2 Degree=3 IsPeriodic=0
    g116: BSplineCurve PolesCount=4 KnotsCount=2 Degree=3 IsPeriodic=0
    g117: BSplineCurve PolesCount=4 KnotsCount=2 Degree=3 IsPeriodic=0
    g118: BSplineCurve PolesCount=4 KnotsCount=2 Degree=3 IsPeriodic=0
    g119: BSplineCurve PolesCount=4 KnotsCount=2 Degree=3 IsPeriodic=0
    g120: BSplineCurve PolesCount=4 KnotsCount=2 Degree=3 IsPeriodic=0
    g121: BSplineCurve PolesCount=4 KnotsCount=2 Degree=3 IsPeriodic=0
    g122: BSplineCurve PolesCount=4 KnotsCount=2 Degree=3 IsPeriodic=0
    g123: BSplineCurve PolesCount=4 KnotsCount=2 Degree=3 IsPeriodic=0
    g124: BSplineCurve PolesCount=4 KnotsCount=2 Degree=3 IsPeriodic=0
    g125: BSplineCurve PolesCount=4 KnotsCount=2 Degree=3 IsPeriodic=0
    g126: BSplineCurve PolesCount=4 KnotsCount=2 Degree=3 IsPeriodic=0
    g127: BSplineCurve PolesCount=4 KnotsCount=2 Degree=3 IsPeriodic=0
    g128: BSplineCurve PolesCount=4 KnotsCount=2 Degree=3 IsPeriodic=0
    g129: BSplineCurve PolesCount=4 KnotsCount=2 Degree=3 IsPeriodic=0
    g130: BSplineCurve PolesCount=4 KnotsCount=2 Degree=3 IsPeriodic=0
    g131: BSplineCurve PolesCount=4 KnotsCount=2 Degree=3 IsPeriodic=0
    g132: BSplineCurve PolesCount=4 KnotsCount=2 Degree=3 IsPeriodic=0
    g133: BSplineCurve PolesCount=4 KnotsCount=2 Degree=3 IsPeriodic=0
    g134: BSplineCurve PolesCount=4 KnotsCount=2 Degree=3 IsPeriodic=0
    g135: BSplineCurve PolesCount=4 KnotsCount=2 Degree=3 IsPeriodic=0
    g136: BSplineCurve PolesCount=4 KnotsCount=2 Degree=3 IsPeriodic=0
    g137: BSplineCurve PolesCount=4 KnotsCount=2 Degree=3 IsPeriodic=0
    g138: BSplineCurve PolesCount=4 KnotsCount=2 Degree=3 IsPeriodic=0
    g139: BSplineCurve PolesCount=4 KnotsCount=2 Degree=3 IsPeriodic=0
    g140: BSplineCurve PolesCount=4 KnotsCount=2 Degree=3 IsPeriodic=0
    g141: BSplineCurve PolesCount=4 KnotsCount=2 Degree=3 IsPeriodic=0
    g142: BSplineCurve PolesCount=4 KnotsCount=2 Degree=3 IsPeriodic=0
    g143: BSplineCurve PolesCount=4 KnotsCount=2 Degree=3 IsPeriodic=0
    g144: BSplineCurve PolesCount=4 KnotsCount=2 Degree=3 IsPeriodic=0
    g145: BSplineCurve PolesCount=4 KnotsCount=2 Degree=3 IsPeriodic=0
    g146: BSplineCurve PolesCount=4 KnotsCount=2 Degree=3 IsPeriodic=0
    g147: BSplineCurve PolesCount=4 KnotsCount=2 Degree=3 IsPeriodic=0
    g148: BSplineCurve PolesCount=4 KnotsCount=2 Degree=3 IsPeriodic=0
    g149: BSplineCurve PolesCount=4 KnotsCount=2 Degree=3 IsPeriodic=0
    g150: BSplineCurve PolesCount=4 KnotsCount=2 Degree=3 IsPeriodic=0
    g151: BSplineCurve PolesCount=4 KnotsCount=2 Degree=3 IsPeriodic=0
    g152: BSplineCurve PolesCount=4 KnotsCount=2 Degree=3 IsPeriodic=0
    g153: BSplineCurve PolesCount=4 KnotsCount=2 Degree=3 IsPeriodic=0
    g154: BSplineCurve PolesCount=4 KnotsCount=2 Degree=3 IsPeriodic=0
    g155: BSplineCurve PolesCount=4 KnotsCount=2 Degree=3 IsPeriodic=0
    g156: BSplineCurve PolesCount=4 KnotsCount=2 Degree=3 IsPeriodic=0
    g157: BSplineCurve PolesCount=4 KnotsCount=2 Degree=3 IsPeriodic=0
    g158: BSplineCurve PolesCount=4 KnotsCount=2 Degree=3 IsPeriodic=0
    g159: BSplineCurve PolesCount=4 KnotsCount=2 Degree=3 IsPeriodic=0
  constraints (160):
    c: Coincident(g10,g11)
    c: Coincident(g4,g5)
    c: Coincident(g11,g12)
    c: Coincident(g0,g12)
    c: Coincident(g5,g6)
    c: Coincident(g9,g10)
    c: Coincident(g0,g1)
    c: Coincident(g8,g9)
    c: Coincident(g1,g2)
    c: Coincident(g3,g4)
    c: Coincident(g2,g3)
    c: Coincident(g7,g8)
    c: Coincident(g6,g7)
    c: Coincident(g79,g80)
    c: Coincident(g96,g97)
    c: Coincident(g109,g110)
    c: Coincident(g13,g26)
    c: Coincident(g110,g111)
    c: Coincident(g13,g14)
    c: Coincident(g136,g137)
    c: Coincident(g102,g103)
    c: Coincident(g82,g83)
    c: Coincident(g137,g138)
    c: Coincident(g103,g104)
    c: Coincident(g78,g79)
    c: Coincident(g83,g84)
    c: Coincident(g80,g81)
    c: Coincident(g25,g26)
    c: Coincident(g95,g96)
    c: Coincident(g108,g109)
    c: Coincident(g73,g81)
    c: Coincident(g14,g15)
    c: Coincident(g111,g112)
    c: Coincident(g127,g131)
    c: Coincident(g127,g128)
    c: Coincident(g87,g88)
    c: Coincident(g91,g92)
    c: Coincident(g112,g113)
    c: Coincident(g15,g16)
    c: Coincident(g130,g131)
    c: Coincident(g97,g98)
    c: Coincident(g88,g89)
    c: Coincident(g84,g85)
    c: Coincident(g92,g93)
    c: Coincident(g113,g114)
    c: Coincident(g16,g17)
    c: Coincident(g17,g18)
    c: Coincident(g114,g115)
    c: Coincident(g82,g100)
    c: Coincident(g129,g130)
    c: Coincident(g128,g129)
    c: Coincident(g73,g74)
    c: Coincident(g107,g108)
    c: Coincident(g135,g136)
    c: Coincident(g18,g19)
    c: Coincident(g19,g20)
    c: Coincident(g106,g107)
    c: Coincident(g24,g25)
    c: Coincident(g99,g100)
    c: Coincident(g106,g120)
    c: Coincident(g74,g75)
    c: Coincident(g75,g76)
    c: Coincident(g138,g139)
    c: Coincident(g119,g120)
    c: Coincident(g139,g140)
    c: Coincident(g132,g140)
    c: Coincident(g20,g21)
    c: Coincident(g98,g99)
    c: Coincident(g118,g119)
    c: Coincident(g132,g133)
    c: Coincident(g21,g22)
    c: Coincident(g115,g116)
    c: Coincident(g90,g91)
    c: Coincident(g89,g90)
    c: Coincident(g77,g78)
    c: Coincident(g134,g135)
    c: Coincident(g85,g86)
    c: Coincident(g86,g87)
    c: Coincident(g23,g24)
    c: Coincident(g104,g105)
    c: Coincident(g101,g102)
    c: Coincident(g94,g95)
    c: Coincident(g117,g118)
    c: Coincident(g101,g105)
    c: Coincident(g22,g23)
    c: Coincident(g93,g94)
    c: Coincident(g76,g77)
    c: Coincident(g133,g134)
    c: Coincident(g116,g117)
    c: Coincident(g148,g149)
    c: Coincident(g157,g158)
    c: Coincident(g158,g159)
    c: Coincident(g147,g148)
    c: Coincident(g146,g147)
    c: Coincident(g156,g157)
    c: Coincident(g149,g150)
    c: Coincident(g57,g58)
    c: Coincident(g155,g156)
    c: Coincident(g46,g47)
    c: Coincident(g56,g57)
    c: Coincident(g47,g48)
    c: Coincident(g48,g49)
    c: Coincident(g45,g46)
    c: Coincident(g150,g151)
    c: Coincident(g55,g56)
    c: Coincident(g49,g50)
    c: Coincident(g122,g123)
    c: Coincident(g43,g44)
    c: Coincident(g44,g45)
    c: Coincident(g54,g55)
    c: Coincident(g123,g124)
    c: Coincident(g42,g43)
    c: Coincident(g50,g51)
    c: Coincident(g124,g125)
    c: Coincident(g53,g54)
    c: Coincident(g40,g41)
    c: Coincident(g52,g53)
    c: Coincident(g51,g52)
    c: Coincident(g58,g59)
    c: Coincident(g121,g122)
    c: Coincident(g39,g40)
    c: Coincident(g41,g42)
    c: Coincident(g38,g39)
    c: Coincident(g125,g126)
    c: Coincident(g121,g126)
    c: Coincident(g32,g33)
    c: Coincident(g31,g32)
    c: Coincident(g153,g159)
    c: Coincident(g37,g38)
    c: Coincident(g59,g60)
    c: Coincident(g67,g68)
    c: Coincident(g154,g155)
    c: Coincident(g66,g67)
    c: Coincident(g36,g37)
    c: Coincident(g60,g61)
    c: Coincident(g153,g154)
    c: Coincident(g65,g66)
    c: Coincident(g68,g69)
    c: Coincident(g71,g72)
    c: Coincident(g141,g144)
    c: Coincident(g33,g34)
    c: Coincident(g64,g65)
    c: Coincident(g145,g146)
    c: Coincident(g141,g142)
    c: Coincident(g63,g64)
    c: Coincident(g145,g152)
    c: Coincident(g143,g144)
    c: Coincident(g61,g62)
    c: Coincident(g34,g35)
    c: Coincident(g29,g30)
    c: Coincident(g35,g36)
    c: Coincident(g62,g63)
    c: Coincident(g27,g30)
    c: Coincident(g69,g70)
    c: Coincident(g70,g71)
    c: Coincident(g142,g143)
    c: Coincident(g28,g29)
    c: Coincident(g151,g152)
    c: Coincident(g27,g28)
    c: Coincident(g31,g72)
FEATURE [Part::Part2DObjectPython] Clone2D006  label="MirroredSketch001 (2D)005"  # Draft 2D object (typed FeaturePython)
  AttachmentOffset = pos=(4.3,23,0) rot=(0,0,-1;1.5708rad)
  AttachmentSupport = -> [Pad017]
  ForceCompound = false
  Fuse = false
  MapMode = 5
  Objects = -> [MirroredSketch005]
  Placement = pos=(-4.3,-1.5,23) rot=(-0.57735,0.57735,0.57735;2.0944rad)
  Scale = (0.65,0.65,0.65)
FEATURE [PartDesign::Pocket] Pocket020
  BaseFeature = -> Pad017
  Direction = (0,-1,2e-16)
  Length = 2
  Length2 = 5
  Profile = -> Clone2D006
  ReferenceAxis = -> Clone2D006 [N_Axis]
  Refine = true
  SideType = 0
  Suppressed = false
  Type = 0
  Type2 = 0
FEATURE [Sketcher::SketchObject] Sketch046
  ArcFitTolerance = 1e-06
  AttachmentSupport = -> [Pad017]
  ExternalGeometry = -> [Pad017]
  ExternalTypes = [0,0]
  FullyConstrained = true
  MakeInternals = false
  MapMode = 5
  Placement = pos=(0,0,3) rot=(0,0,1;0rad)
  _ExternalGeoVersion = 0
  sketch-geometry (4):
    g0: LineSegment StartX=-13.5 StartY=-5.575 StartZ=0 EndX=13.5 EndY=-5.575 EndZ=0
    g1: LineSegment StartX=13.5 StartY=-5.575 StartZ=0 EndX=13.5 EndY=-2.575 EndZ=0
    g2: LineSegment StartX=13.5 StartY=-2.575 StartZ=0 EndX=-13.5 EndY=-2.575 EndZ=0
    g3: LineSegment StartX=-13.5 StartY=-2.575 StartZ=0 EndX=-13.5 EndY=-5.575 EndZ=0
  constraints (11):
    c: Coincident(g0,g1)
    c: Coincident(g1,g2)
    c: Coincident(g2,g3)
    c: Coincident(g3,g0)
    c: Horizontal(g2)
    c: Vertical(g1)
    c: Vertical(g3)
    c: DistanceY(g1,g1) = 3
    c: Horizontal(g0)
    c: Coincident(g0,g-3)
    c: PointOnObject(g2,g-4)
FEATURE [PartDesign::AdditiveLoft] AdditiveLoft010
  BaseFeature = -> Pocket020
  Closed = false
  Profile = -> Sketch046
  Refine = true
  Ruled = false
  Sections = -> [Pocket020]
  Suppressed = false
FEATURE [PartDesign::Chamfer] Chamfer007
  Angle = 45
  Base = -> AdditiveLoft010 [Edge468,Edge489]
  BaseFeature = -> AdditiveLoft010
  ChamferType = 0
  FlipDirection = false
  Refine = true
  Size = 2
  Size2 = 1
  SupportTransform = false
  Suppressed = false
  UseAllEdges = false
FEATURE [Sketcher::SketchObject] Sketch047
  ArcFitTolerance = 1e-06
  AttachmentSupport = -> [Chamfer007]
  ExternalGeometry = -> [Chamfer007]
  ExternalTypes = [0,0]
  FullyConstrained = true
  MakeInternals = false
  MapMode = 5
  Placement = pos=(0,0,43.3) rot=(0,0,1;0rad)
  _ExternalGeoVersion = 0
  sketch-geometry (2):
    g0: Circle CenterX=-31.8 CenterY=-2 CenterZ=0 NormalX=0 NormalY=0 NormalZ=1 AngleXU=0 Radius=1.5
    g1: Circle CenterX=-0.2 CenterY=-2 CenterZ=0 NormalX=0 NormalY=0 NormalZ=1 AngleXU=0 Radius=1.5
  constraints (4):
    c: Coincident(g0,g-4)
    c: Coincident(g1,g-3)
    c: Equal(g1,g0)
    c: Diameter(g0) = 3
FEATURE [PartDesign::Pocket] Pocket021
  BaseFeature = -> Chamfer007
  Direction = (0,0,-1)
  Length = 11
  Length2 = 5
  Profile = -> Sketch047
  ReferenceAxis = -> Sketch047 [N_Axis]
  Refine = true
  SideType = 0
  Suppressed = false
  Type = 0
  Type2 = 0
FEATURE [Sketcher::SketchObject] Sketch048
  ArcFitTolerance = 1e-06
  ExternalTypes = [0,0]
  FullyConstrained = true
  MakeInternals = false
  MapMode = 5
  Placement = pos=(0,0,3) rot=(0,0,1;0rad)
  _ExternalGeoVersion = 0
  sketch-geometry (4):
    g0: LineSegment StartX=-5 StartY=-2.575 StartZ=0 EndX=5 EndY=-2.575 EndZ=0
    g1: LineSegment StartX=5 StartY=-2.575 StartZ=0 EndX=5 EndY=5.575 EndZ=0
    g2: LineSegment StartX=5 StartY=5.575 StartZ=0 EndX=-5 EndY=5.575 EndZ=0
    g3: LineSegment StartX=-5 StartY=5.575 StartZ=0 EndX=-5 EndY=-2.575 EndZ=0
  constraints (11):
    c: Coincident(g0,g1)
    c: Coincident(g1,g2)
    c: Coincident(g2,g3)
    c: Coincident(g3,g0)
    c: Horizontal(g0)
    c: Vertical(g1)
    c: Vertical(g3)
    c: PointOnObject(g0,g-3)
    c: PointOnObject(g1,g-4)
    c: DistanceX(g2,g2) = 10
    c: Symmetric(g1,g2,g-2)
FEATURE [Sketcher::SketchObject] Sketch049
  ArcFitTolerance = 1e-06
  ExternalTypes = [0]
  FullyConstrained = true
  MakeInternals = false
  MapMode = 5
  Placement = pos=(1e-16,-2.74177,0.16106) rot=(0,0.727545,0.68606;3.14159rad)
  _ExternalGeoVersion = 0
  sketch-geometry (4):
    g0: LineSegment StartX=-5.5 StartY=10.9438 StartZ=0 EndX=-5.5 EndY=10.8438 EndZ=0
    g1: LineSegment StartX=-5.5 StartY=10.8438 StartZ=0 EndX=4.5 EndY=10.8438 EndZ=0
    g2: LineSegment StartX=4.5 StartY=10.8438 StartZ=0 EndX=4.5 EndY=10.9438 EndZ=0
    g3: LineSegment StartX=4.5 StartY=10.9438 StartZ=0 EndX=-5.5 EndY=10.9438 EndZ=0
  constraints (12):
    c: Coincident(g0,g1)
    c: Coincident(g1,g2)
    c: Coincident(g2,g3)
    c: Coincident(g3,g0)
    c: Vertical(g0)
    c: Vertical(g2)
    c: Horizontal(g1)
    c: Horizontal(g3)
    c: DistanceX(g3,g3) = 10
    c: DistanceY(g2,g2) = 0.1
    c: DistanceY(g-3,g0) = 8
    c: DistanceX(g-3,g0) = 8
FEATURE [PartDesign::AdditiveLoft] AdditiveLoft011
  BaseFeature = -> Pocket021
  Closed = false
  Profile = -> Sketch048
  Refine = true
  Ruled = false
  Sections = -> [Sketch049]
  Suppressed = false
FEATURE [Sketcher::SketchObject] Sketch050
  ArcFitTolerance = 1e-06
  AttachmentSupport = -> [AdditiveLoft011]
  ExternalGeometry = -> [Sketch047]
  ExternalTypes = [0,0]
  FullyConstrained = true
  MakeInternals = false
  MapMode = 5
  Placement = pos=(0,0,43.3) rot=(0,0,1;0rad)
  _ExternalGeoVersion = 1
  sketch-geometry (2):
    g0: Circle CenterX=-31.8 CenterY=-2 CenterZ=0 NormalX=0 NormalY=0 NormalZ=1 AngleXU=0 Radius=2
    g1: Circle CenterX=-0.2 CenterY=-2 CenterZ=0 NormalX=0 NormalY=0 NormalZ=1 AngleXU=0 Radius=2
  constraints (4):
    c: Coincident(g0,g-3)
    c: Coincident(g1,g-4)
    c: Equal(g0,g1)
    c: Diameter(g0) = 4
FEATURE [PartDesign::Pocket] Pocket022
  BaseFeature = -> AdditiveLoft011
  Direction = (0,0,-1)
  Length = 5
  Length2 = 5
  Profile = -> Sketch050
  ReferenceAxis = -> Sketch050 [N_Axis]
  Refine = true
  SideType = 0
  Suppressed = false
  Type = 0
  Type2 = 0
FEATURE [Sketcher::SketchObject] Sketch051
  ArcFitTolerance = 1e-06
  AttachmentSupport = -> [Pocket022]
  ExternalGeometry = -> [Sketch047]
  ExternalTypes = [0,0]
  FullyConstrained = true
  MakeInternals = false
  MapMode = 5
  Placement = pos=(0,0,43.3) rot=(0,0,1;0rad)
  _ExternalGeoVersion = 1
  sketch-geometry (2):
    g0: Circle CenterX=-31.8 CenterY=-2 CenterZ=0 NormalX=0 NormalY=0 NormalZ=1 AngleXU=0 Radius=2.25
    g1: Circle CenterX=-0.2 CenterY=-2 CenterZ=0 NormalX=0 NormalY=0 NormalZ=1 AngleXU=0 Radius=2.25
  constraints (4):
    c: Coincident(g0,g-4)
    c: Coincident(g1,g-3)
    c: Equal(g0,g1)
    c: Diameter(g0) = 4.5
FEATURE [PartDesign::Pocket] Pocket023
  BaseFeature = -> Pocket022
  Direction = (0,0,-1)
  Length = 1
  Length2 = 5
  Profile = -> Sketch051
  ReferenceAxis = -> Sketch051 [N_Axis]
  Refine = true
  SideType = 0
  Suppressed = false
  Type = 0
  Type2 = 0
FEATURE [Sketcher::SketchObject] Sketch052
  ArcFitTolerance = 1e-06
  AttachmentSupport = -> [Pocket023]
  ExternalTypes = [0]
  FullyConstrained = false
  MakeInternals = false
  MapMode = 5
  Placement = pos=(0,-6,0) rot=(1,0,0;1.5708rad)
  _ExternalGeoVersion = 1
  sketch-geometry (256):
    g0: LineSegment [constr] StartX=-1.15063 StartY=41.781 StartZ=0 EndX=-30.7091 EndY=41.781 EndZ=0
    g1: BSplineCurve PolesCount=3 KnotsCount=2 Degree=2 IsPeriodic=0
    g2: BSplineCurve PolesCount=3 KnotsCount=2 Degree=2 IsPeriodic=0
    g3: BSplineCurve PolesCount=3 KnotsCount=2 Degree=2 IsPeriodic=0
    g4: LineSegment StartX=-2.53438 StartY=38.0222 StartZ=0 EndX=-1.91272 EndY=38.0222 EndZ=0
    g5: BSplineCurve PolesCount=3 KnotsCount=2 Degree=2 IsPeriodic=0
    g6: BSplineCurve PolesCount=3 KnotsCount=2 Degree=2 IsPeriodic=0
    g7: LineSegment StartX=-1.45216 StartY=38.4828 StartZ=0 EndX=-1.45216 EndY=40.0607 EndZ=0
    g8: BSplineCurve PolesCount=3 KnotsCount=2 Degree=2 IsPeriodic=0
    g9: BSplineCurve PolesCount=3 KnotsCount=2 Degree=2 IsPeriodic=0
    g10: LineSegment StartX=-1.86522 StartY=40.5398 StartZ=0 EndX=-2.55916 EndY=40.5398 EndZ=0
    g11: BSplineCurve PolesCount=3 KnotsCount=2 Degree=2 IsPeriodic=0
    g12: BSplineCurve PolesCount=3 KnotsCount=2 Degree=2 IsPeriodic=0
    g13: LineSegment StartX=-2.5571 StartY=40.8331 StartZ=0 EndX=-1.85283 EndY=40.8331 EndZ=0
    g14: BSplineCurve PolesCount=3 KnotsCount=2 Degree=2 IsPeriodic=0
    g15: BSplineCurve PolesCount=3 KnotsCount=2 Degree=2 IsPeriodic=0
    g16: LineSegment StartX=-1.15063 StartY=40.0772 StartZ=0 EndX=-1.15063 EndY=38.4601 EndZ=0
    g17: BSplineCurve PolesCount=3 KnotsCount=2 Degree=2 IsPeriodic=0
    g18: BSplineCurve PolesCount=3 KnotsCount=2 Degree=2 IsPeriodic=0
    g19: BSplineCurve PolesCount=3 KnotsCount=2 Degree=2 IsPeriodic=0
    g20: BSplineCurve PolesCount=3 KnotsCount=2 Degree=2 IsPeriodic=0
    g21: BSplineCurve PolesCount=3 KnotsCount=2 Degree=2 IsPeriodic=0
    g22: BSplineCurve PolesCount=3 KnotsCount=2 Degree=2 IsPeriodic=0
    g23: LineSegment StartX=-3.74051 StartY=40.5274 StartZ=0 EndX=-4.37249 EndY=40.5274 EndZ=0
    g24: LineSegment StartX=-4.37249 StartY=40.5274 StartZ=0 EndX=-4.37249 EndY=39.8872 EndZ=0
    g25: LineSegment StartX=-4.37249 StartY=39.8872 StartZ=0 EndX=-3.76942 EndY=39.8872 EndZ=0
    g26: BSplineCurve PolesCount=3 KnotsCount=2 Degree=2 IsPeriodic=0
    g27: BSplineCurve PolesCount=3 KnotsCount=2 Degree=2 IsPeriodic=0
    g28: LineSegment StartX=-3.43898 StartY=38.648 StartZ=0 EndX=-4.08128 EndY=38.648 EndZ=0
    g29: BSplineCurve PolesCount=3 KnotsCount=2 Degree=2 IsPeriodic=0
    g30: BSplineCurve PolesCount=3 KnotsCount=2 Degree=2 IsPeriodic=0
    g31: LineSegment StartX=-4.68228 StartY=39.2573 StartZ=0 EndX=-4.68228 EndY=40.6451 EndZ=0
    g32: BSplineCurve PolesCount=3 KnotsCount=2 Degree=2 IsPeriodic=0
    g33: BSplineCurve PolesCount=3 KnotsCount=2 Degree=2 IsPeriodic=0
    g34: LineSegment StartX=-4.50467 StartY=40.8393 StartZ=0 EndX=-3.71986 EndY=40.8393 EndZ=0
    g35: BSplineCurve PolesCount=3 KnotsCount=2 Degree=2 IsPeriodic=0
    g36: BSplineCurve PolesCount=3 KnotsCount=2 Degree=2 IsPeriodic=0
    g37: BSplineCurve PolesCount=3 KnotsCount=2 Degree=2 IsPeriodic=0
    g38: BSplineCurve PolesCount=3 KnotsCount=2 Degree=2 IsPeriodic=0
    g39: LineSegment StartX=-3.72812 StartY=39.5877 StartZ=0 EndX=-4.37249 EndY=39.5877 EndZ=0
    g40: LineSegment StartX=-4.37249 StartY=39.5877 StartZ=0 EndX=-4.37249 EndY=39.2077 EndZ=0
    g41: BSplineCurve PolesCount=3 KnotsCount=2 Degree=2 IsPeriodic=0
    g42: BSplineCurve PolesCount=3 KnotsCount=2 Degree=2 IsPeriodic=0
    g43: LineSegment StartX=-4.07302 StartY=38.9495 StartZ=0 EndX=-3.43898 EndY=38.9495 EndZ=0
    g44: BSplineCurve PolesCount=3 KnotsCount=2 Degree=2 IsPeriodic=0
    g45: BSplineCurve PolesCount=3 KnotsCount=2 Degree=2 IsPeriodic=0
    g46: BSplineCurve PolesCount=3 KnotsCount=2 Degree=2 IsPeriodic=0
    g47: BSplineCurve PolesCount=3 KnotsCount=2 Degree=2 IsPeriodic=0
    g48: BSplineCurve PolesCount=3 KnotsCount=2 Degree=2 IsPeriodic=0
    g49: BSplineCurve PolesCount=3 KnotsCount=2 Degree=2 IsPeriodic=0
    g50: BSplineCurve PolesCount=3 KnotsCount=2 Degree=2 IsPeriodic=0
    g51: LineSegment StartX=-6.16517 StartY=38.9516 StartZ=0 EndX=-5.52493 EndY=38.9516 EndZ=0
    g52: LineSegment StartX=-5.52493 StartY=38.9516 StartZ=0 EndX=-5.52493 EndY=40.6699 EndZ=0
    g53: BSplineCurve PolesCount=3 KnotsCount=2 Degree=2 IsPeriodic=0
    g54: BSplineCurve PolesCount=3 KnotsCount=2 Degree=2 IsPeriodic=0
    g55: BSplineCurve PolesCount=3 KnotsCount=2 Degree=2 IsPeriodic=0
    g56: BSplineCurve PolesCount=3 KnotsCount=2 Degree=2 IsPeriodic=0
    g57: BSplineCurve PolesCount=3 KnotsCount=2 Degree=2 IsPeriodic=0
    g58: BSplineCurve PolesCount=3 KnotsCount=2 Degree=2 IsPeriodic=0
    g59: BSplineCurve PolesCount=3 KnotsCount=2 Degree=2 IsPeriodic=0
    g60: BSplineCurve PolesCount=3 KnotsCount=2 Degree=2 IsPeriodic=0
    g61: BSplineCurve PolesCount=3 KnotsCount=2 Degree=2 IsPeriodic=0
    g62: LineSegment StartX=-7.87317 StartY=38.9557 StartZ=0 EndX=-7.40434 EndY=38.9557 EndZ=0
    g63: LineSegment StartX=-7.40434 StartY=38.9557 StartZ=0 EndX=-7.40434 EndY=40.6802 EndZ=0
    g64: BSplineCurve PolesCount=3 KnotsCount=2 Degree=2 IsPeriodic=0
    g65: BSplineCurve PolesCount=3 KnotsCount=2 Degree=2 IsPeriodic=0
    g66: LineSegment StartX=-7.10694 StartY=40.6658 StartZ=0 EndX=-7.10694 EndY=38.9557 EndZ=0
    g67: LineSegment StartX=-7.10694 StartY=38.9557 StartZ=0 EndX=-6.94998 EndY=38.9557 EndZ=0
    g68: BSplineCurve PolesCount=3 KnotsCount=2 Degree=2 IsPeriodic=0
    g69: BSplineCurve PolesCount=3 KnotsCount=2 Degree=2 IsPeriodic=0
    g70: LineSegment StartX=-6.94791 StartY=38.6625 StartZ=0 EndX=-7.10694 EndY=38.6625 EndZ=0
    g71: LineSegment StartX=-7.10694 StartY=38.6625 StartZ=0 EndX=-7.10694 EndY=37.8756 EndZ=0
    g72: BSplineCurve PolesCount=3 KnotsCount=2 Degree=2 IsPeriodic=0
    g73: LineSegment StartX=-8.70548 StartY=39.4369 StartZ=0 EndX=-8.70548 EndY=40.071 EndZ=0
    g74: BSplineCurve PolesCount=3 KnotsCount=2 Degree=2 IsPeriodic=0
    g75: BSplineCurve PolesCount=3 KnotsCount=2 Degree=2 IsPeriodic=0
    g76: BSplineCurve PolesCount=3 KnotsCount=2 Degree=2 IsPeriodic=0
    g77: BSplineCurve PolesCount=3 KnotsCount=2 Degree=2 IsPeriodic=0
    g78: LineSegment StartX=-9.66584 StartY=40.007 StartZ=0 EndX=-9.66584 EndY=39.4803 EndZ=0
    g79: BSplineCurve PolesCount=3 KnotsCount=2 Degree=2 IsPeriodic=0
    g80: BSplineCurve PolesCount=3 KnotsCount=2 Degree=2 IsPeriodic=0
    g81: BSplineCurve PolesCount=3 KnotsCount=2 Degree=2 IsPeriodic=0
    g82: BSplineCurve PolesCount=3 KnotsCount=2 Degree=2 IsPeriodic=0
    g83: BSplineCurve PolesCount=3 KnotsCount=2 Degree=2 IsPeriodic=0
    g84: LineSegment StartX=-9.95705 StartY=39.3481 StartZ=0 EndX=-9.95705 EndY=40.0669 EndZ=0
    g85: BSplineCurve PolesCount=3 KnotsCount=2 Degree=2 IsPeriodic=0
    g86: BSplineCurve PolesCount=3 KnotsCount=2 Degree=2 IsPeriodic=0
    g87: BSplineCurve PolesCount=3 KnotsCount=2 Degree=2 IsPeriodic=0
    g88: BSplineCurve PolesCount=3 KnotsCount=2 Degree=2 IsPeriodic=0
    g89: LineSegment StartX=-8.41014 StartY=40.0565 StartZ=0 EndX=-8.41014 EndY=39.3812 EndZ=0
    g90: BSplineCurve PolesCount=3 KnotsCount=2 Degree=2 IsPeriodic=0
    g91: BSplineCurve PolesCount=3 KnotsCount=2 Degree=2 IsPeriodic=0
    g92: BSplineCurve PolesCount=3 KnotsCount=2 Degree=2 IsPeriodic=0
    g93: BSplineCurve PolesCount=3 KnotsCount=2 Degree=2 IsPeriodic=0
    g94: LineSegment StartX=-10.7873 StartY=39.3048 StartZ=0 EndX=-10.7873 EndY=40.166 EndZ=0
    g95: BSplineCurve PolesCount=3 KnotsCount=2 Degree=2 IsPeriodic=0
    g96: BSplineCurve PolesCount=3 KnotsCount=2 Degree=2 IsPeriodic=0
    g97: LineSegment StartX=-11.1301 StartY=40.5398 StartZ=0 EndX=-11.7415 EndY=40.5398 EndZ=0
    g98: LineSegment StartX=-11.7415 StartY=40.5398 StartZ=0 EndX=-11.7415 EndY=38.9578 EndZ=0
    g99: LineSegment StartX=-11.7415 StartY=38.9578 StartZ=0 EndX=-11.1446 EndY=38.9578 EndZ=0
    g100: BSplineCurve PolesCount=3 KnotsCount=2 Degree=2 IsPeriodic=0
    g101: BSplineCurve PolesCount=3 KnotsCount=2 Degree=2 IsPeriodic=0
    g102: BSplineCurve PolesCount=3 KnotsCount=2 Degree=2 IsPeriodic=0
    g103: BSplineCurve PolesCount=3 KnotsCount=2 Degree=2 IsPeriodic=0
    g104: BSplineCurve PolesCount=3 KnotsCount=2 Degree=2 IsPeriodic=0
    g105: BSplineCurve PolesCount=3 KnotsCount=2 Degree=2 IsPeriodic=0
    g106: BSplineCurve PolesCount=3 KnotsCount=2 Degree=2 IsPeriodic=0
    g107: BSplineCurve PolesCount=3 KnotsCount=2 Degree=2 IsPeriodic=0
    g108: BSplineCurve PolesCount=3 KnotsCount=2 Degree=2 IsPeriodic=0
    g109: BSplineCurve PolesCount=3 KnotsCount=2 Degree=2 IsPeriodic=0
    g110: LineSegment StartX=-11.7353 StartY=41.1883 StartZ=0 EndX=-11.7353 EndY=40.8393 EndZ=0
    g111: BSplineCurve PolesCount=3 KnotsCount=2 Degree=2 IsPeriodic=0
    g112: BSplineCurve PolesCount=3 KnotsCount=2 Degree=2 IsPeriodic=0
    g113: BSplineCurve PolesCount=3 KnotsCount=2 Degree=2 IsPeriodic=0
    g114: BSplineCurve PolesCount=3 KnotsCount=2 Degree=2 IsPeriodic=0
    g115: BSplineCurve PolesCount=3 KnotsCount=2 Degree=2 IsPeriodic=0
    g116: BSplineCurve PolesCount=3 KnotsCount=2 Degree=2 IsPeriodic=0
    g117: BSplineCurve PolesCount=3 KnotsCount=2 Degree=2 IsPeriodic=0
    g118: BSplineCurve PolesCount=3 KnotsCount=2 Degree=2 IsPeriodic=0
    g119: BSplineCurve PolesCount=3 KnotsCount=2 Degree=2 IsPeriodic=0
    g120: BSplineCurve PolesCount=3 KnotsCount=2 Degree=2 IsPeriodic=0
    g121: BSplineCurve PolesCount=3 KnotsCount=2 Degree=2 IsPeriodic=0
    g122: BSplineCurve PolesCount=3 KnotsCount=2 Degree=2 IsPeriodic=0
    g123: BSplineCurve PolesCount=3 KnotsCount=2 Degree=2 IsPeriodic=0
    g124: LineSegment StartX=-13.5651 StartY=38.9516 StartZ=0 EndX=-12.9249 EndY=38.9516 EndZ=0
    g125: LineSegment StartX=-12.9249 StartY=38.9516 StartZ=0 EndX=-12.9249 EndY=40.6699 EndZ=0
    g126: BSplineCurve PolesCount=3 KnotsCount=2 Degree=2 IsPeriodic=0
    g127: BSplineCurve PolesCount=3 KnotsCount=2 Degree=2 IsPeriodic=0
    g128: BSplineCurve PolesCount=3 KnotsCount=2 Degree=2 IsPeriodic=0
    g129: BSplineCurve PolesCount=3 KnotsCount=2 Degree=2 IsPeriodic=0
    g130: BSplineCurve PolesCount=3 KnotsCount=2 Degree=2 IsPeriodic=0
    g131: BSplineCurve PolesCount=3 KnotsCount=2 Degree=2 IsPeriodic=0
    g132: BSplineCurve PolesCount=3 KnotsCount=2 Degree=2 IsPeriodic=0
    g133: LineSegment StartX=-14.8993 StartY=40.5274 StartZ=0 EndX=-15.5313 EndY=40.5274 EndZ=0
    g134: LineSegment StartX=-15.5313 StartY=40.5274 StartZ=0 EndX=-15.5313 EndY=39.8872 EndZ=0
    g135: LineSegment StartX=-15.5313 StartY=39.8872 StartZ=0 EndX=-14.9282 EndY=39.8872 EndZ=0
    g136: BSplineCurve PolesCount=3 KnotsCount=2 Degree=2 IsPeriodic=0
    g137: BSplineCurve PolesCount=3 KnotsCount=2 Degree=2 IsPeriodic=0
    g138: LineSegment StartX=-14.5978 StartY=38.648 StartZ=0 EndX=-15.2401 EndY=38.648 EndZ=0
    g139: BSplineCurve PolesCount=3 KnotsCount=2 Degree=2 IsPeriodic=0
    g140: BSplineCurve PolesCount=3 KnotsCount=2 Degree=2 IsPeriodic=0
    g141: LineSegment StartX=-15.8411 StartY=39.2573 StartZ=0 EndX=-15.8411 EndY=40.6451 EndZ=0
    g142: BSplineCurve PolesCount=3 KnotsCount=2 Degree=2 IsPeriodic=0
    g143: BSplineCurve PolesCount=3 KnotsCount=2 Degree=2 IsPeriodic=0
    g144: LineSegment StartX=-15.6635 StartY=40.8393 StartZ=0 EndX=-14.8786 EndY=40.8393 EndZ=0
    g145: BSplineCurve PolesCount=3 KnotsCount=2 Degree=2 IsPeriodic=0
    g146: BSplineCurve PolesCount=3 KnotsCount=2 Degree=2 IsPeriodic=0
    g147: BSplineCurve PolesCount=3 KnotsCount=2 Degree=2 IsPeriodic=0
    g148: BSplineCurve PolesCount=3 KnotsCount=2 Degree=2 IsPeriodic=0
    g149: LineSegment StartX=-14.8869 StartY=39.5877 StartZ=0 EndX=-15.5313 EndY=39.5877 EndZ=0
    g150: LineSegment StartX=-15.5313 StartY=39.5877 StartZ=0 EndX=-15.5313 EndY=39.2077 EndZ=0
    g151: BSplineCurve PolesCount=3 KnotsCount=2 Degree=2 IsPeriodic=0
    g152: BSplineCurve PolesCount=3 KnotsCount=2 Degree=2 IsPeriodic=0
    g153: LineSegment StartX=-15.2318 StartY=38.9495 StartZ=0 EndX=-14.5978 EndY=38.9495 EndZ=0
    g154: BSplineCurve PolesCount=3 KnotsCount=2 Degree=2 IsPeriodic=0
    g155: BSplineCurve PolesCount=3 KnotsCount=2 Degree=2 IsPeriodic=0
    g156: LineSegment StartX=-17.6792 StartY=40.2073 StartZ=0 EndX=-17.6792 EndY=39.3027 EndZ=0
    g157: BSplineCurve PolesCount=3 KnotsCount=2 Degree=2 IsPeriodic=0
    g158: BSplineCurve PolesCount=3 KnotsCount=2 Degree=2 IsPeriodic=0
    g159: LineSegment StartX=-17.3632 StartY=38.964 StartZ=0 EndX=-16.723 EndY=38.964 EndZ=0
    g160: LineSegment StartX=-16.723 StartY=38.964 StartZ=0 EndX=-16.723 EndY=40.5419 EndZ=0
    g161: LineSegment StartX=-16.723 StartY=40.5419 StartZ=0 EndX=-17.3859 EndY=40.5419 EndZ=0
    g162: BSplineCurve PolesCount=3 KnotsCount=2 Degree=2 IsPeriodic=0
    g163: BSplineCurve PolesCount=3 KnotsCount=2 Degree=2 IsPeriodic=0
    g164: BSplineCurve PolesCount=3 KnotsCount=2 Degree=2 IsPeriodic=0
    g165: BSplineCurve PolesCount=3 KnotsCount=2 Degree=2 IsPeriodic=0
    g166: BSplineCurve PolesCount=3 KnotsCount=2 Degree=2 IsPeriodic=0
    g167: BSplineCurve PolesCount=3 KnotsCount=2 Degree=2 IsPeriodic=0
    g168: BSplineCurve PolesCount=3 KnotsCount=2 Degree=2 IsPeriodic=0
    g169: LineSegment StartX=-17.4004 StartY=40.8393 StartZ=0 EndX=-16.723 EndY=40.8393 EndZ=0
    g170: LineSegment StartX=-16.723 StartY=40.8393 StartZ=0 EndX=-16.723 EndY=41.5931 EndZ=0
    g171: BSplineCurve PolesCount=3 KnotsCount=2 Degree=2 IsPeriodic=0
    g172: BSplineCurve PolesCount=3 KnotsCount=2 Degree=2 IsPeriodic=0
    g173: BSplineCurve PolesCount=3 KnotsCount=2 Degree=2 IsPeriodic=0
    g174: BSplineCurve PolesCount=3 KnotsCount=2 Degree=2 IsPeriodic=0
    g175: BSplineCurve PolesCount=3 KnotsCount=2 Degree=2 IsPeriodic=0
    g176: LineSegment StartX=-18.8667 StartY=37.8859 StartZ=0 EndX=-18.8667 EndY=38.6501 EndZ=0
    g177: LineSegment StartX=-18.8667 StartY=38.6501 StartZ=0 EndX=-19.507 EndY=38.6501 EndZ=0
    g178: BSplineCurve PolesCount=3 KnotsCount=2 Degree=2 IsPeriodic=0
    g179: BSplineCurve PolesCount=3 KnotsCount=2 Degree=2 IsPeriodic=0
    g180: LineSegment StartX=-20.1162 StartY=39.2676 StartZ=0 EndX=-20.1162 EndY=40.6658 EndZ=0
    g181: BSplineCurve PolesCount=3 KnotsCount=2 Degree=2 IsPeriodic=0
    g182: BSplineCurve PolesCount=3 KnotsCount=2 Degree=2 IsPeriodic=0
    g183: LineSegment StartX=-19.8209 StartY=40.6617 StartZ=0 EndX=-19.8209 EndY=39.3027 EndZ=0
    g184: BSplineCurve PolesCount=3 KnotsCount=2 Degree=2 IsPeriodic=0
    g185: LineSegment StartX=-19.4574 StartY=38.9475 StartZ=0 EndX=-18.8667 EndY=38.9475 EndZ=0
    g186: LineSegment StartX=-18.8667 StartY=38.9475 StartZ=0 EndX=-18.8667 EndY=40.6596 EndZ=0
    g187: BSplineCurve PolesCount=3 KnotsCount=2 Degree=2 IsPeriodic=0
    g188: BSplineCurve PolesCount=3 KnotsCount=2 Degree=2 IsPeriodic=0
    g189: LineSegment StartX=-18.5652 StartY=40.6493 StartZ=0 EndX=-18.5652 EndY=37.8942 EndZ=0
    g190: LineSegment StartX=-20.963 StartY=39.5918 StartZ=0 EndX=-21.911 EndY=39.5918 EndZ=0
    g191: BSplineCurve PolesCount=3 KnotsCount=2 Degree=2 IsPeriodic=0
    g192: BSplineCurve PolesCount=3 KnotsCount=2 Degree=2 IsPeriodic=0
    g193: BSplineCurve PolesCount=3 KnotsCount=2 Degree=2 IsPeriodic=0
    g194: BSplineCurve PolesCount=3 KnotsCount=2 Degree=2 IsPeriodic=0
    g195: BSplineCurve PolesCount=3 KnotsCount=2 Degree=2 IsPeriodic=0
    g196: BSplineCurve PolesCount=3 KnotsCount=2 Degree=2 IsPeriodic=0
    g197: BSplineCurve PolesCount=3 KnotsCount=2 Degree=2 IsPeriodic=0
    g198: BSplineCurve PolesCount=3 KnotsCount=2 Degree=2 IsPeriodic=0
    g199: LineSegment StartX=-22.2063 StartY=39.344 StartZ=0 EndX=-22.2063 EndY=39.7364 EndZ=0
    g200: BSplineCurve PolesCount=3 KnotsCount=2 Degree=2 IsPeriodic=0
    g201: LineSegment StartX=-22.0679 StartY=39.8851 StartZ=0 EndX=-20.9589 EndY=39.8851 EndZ=0
    g202: LineSegment StartX=-20.9589 StartY=39.8851 StartZ=0 EndX=-20.9589 EndY=40.1577 EndZ=0
    g203: BSplineCurve PolesCount=3 KnotsCount=2 Degree=2 IsPeriodic=0
    g204: LineSegment StartX=-21.2811 StartY=40.5377 StartZ=0 EndX=-22.0308 EndY=40.5377 EndZ=0
    g205: BSplineCurve PolesCount=3 KnotsCount=2 Degree=2 IsPeriodic=0
    g206: BSplineCurve PolesCount=3 KnotsCount=2 Degree=2 IsPeriodic=0
    g207: LineSegment StartX=-22.0328 StartY=40.8393 StartZ=0 EndX=-21.2728 EndY=40.8393 EndZ=0
    g208: BSplineCurve PolesCount=3 KnotsCount=2 Degree=2 IsPeriodic=0
    g209: BSplineCurve PolesCount=3 KnotsCount=2 Degree=2 IsPeriodic=0
    g210: BSplineCurve PolesCount=3 KnotsCount=2 Degree=2 IsPeriodic=0
    g211: BSplineCurve PolesCount=3 KnotsCount=2 Degree=2 IsPeriodic=0
    g212: BSplineCurve PolesCount=3 KnotsCount=2 Degree=2 IsPeriodic=0
    g213: BSplineCurve PolesCount=3 KnotsCount=2 Degree=2 IsPeriodic=0
    g214: BSplineCurve PolesCount=3 KnotsCount=2 Degree=2 IsPeriodic=0
    g215: BSplineCurve PolesCount=3 KnotsCount=2 Degree=2 IsPeriodic=0
    g216: BSplineCurve PolesCount=3 KnotsCount=2 Degree=2 IsPeriodic=0
    g217: BSplineCurve PolesCount=3 KnotsCount=2 Degree=2 IsPeriodic=0
    g218: LineSegment StartX=-23.6954 StartY=38.9516 StartZ=0 EndX=-23.0551 EndY=38.9516 EndZ=0
    g219: LineSegment StartX=-23.0551 StartY=38.9516 StartZ=0 EndX=-23.0551 EndY=40.6699 EndZ=0
    g220: BSplineCurve PolesCount=3 KnotsCount=2 Degree=2 IsPeriodic=0
    g221: BSplineCurve PolesCount=3 KnotsCount=2 Degree=2 IsPeriodic=0
    g222: BSplineCurve PolesCount=3 KnotsCount=2 Degree=2 IsPeriodic=0
    g223: LineSegment StartX=-27.3386 StartY=40.2197 StartZ=0 EndX=-28.1337 EndY=37.857 EndZ=0
    g224: BSplineCurve PolesCount=3 KnotsCount=2 Degree=2 IsPeriodic=0
    g225: BSplineCurve PolesCount=3 KnotsCount=2 Degree=2 IsPeriodic=0
    g226: BSplineCurve PolesCount=3 KnotsCount=2 Degree=2 IsPeriodic=0
    g227: LineSegment StartX=-28.4167 StartY=37.9603 StartZ=0 EndX=-27.5059 EndY=40.6988 EndZ=0
    g228: BSplineCurve PolesCount=3 KnotsCount=2 Degree=2 IsPeriodic=0
    g229: BSplineCurve PolesCount=3 KnotsCount=2 Degree=2 IsPeriodic=0
    g230: LineSegment StartX=-27.1961 StartY=40.703 StartZ=0 EndX=-26.2605 EndY=37.9313 EndZ=0
    g231: BSplineCurve PolesCount=3 KnotsCount=2 Degree=2 IsPeriodic=0
    g232: BSplineCurve PolesCount=3 KnotsCount=2 Degree=2 IsPeriodic=0
    g233: BSplineCurve PolesCount=3 KnotsCount=2 Degree=2 IsPeriodic=0
    g234: LineSegment StartX=-26.5538 StartY=37.8735 StartZ=0 EndX=-27.3386 EndY=40.2197 EndZ=0
    g235: BSplineCurve PolesCount=3 KnotsCount=2 Degree=2 IsPeriodic=0
    g236: BSplineCurve PolesCount=3 KnotsCount=2 Degree=2 IsPeriodic=0
    g237: BSplineCurve PolesCount=3 KnotsCount=2 Degree=2 IsPeriodic=0
    g238: LineSegment StartX=-29.7529 StartY=37.9355 StartZ=0 EndX=-29.1891 EndY=39.9016 EndZ=0
    g239: LineSegment StartX=-29.1891 StartY=39.9016 StartZ=0 EndX=-29.9429 EndY=39.9016 EndZ=0
    g240: LineSegment StartX=-29.9429 StartY=39.9016 StartZ=0 EndX=-29.9429 EndY=39.4514 EndZ=0
    g241: BSplineCurve PolesCount=3 KnotsCount=2 Degree=2 IsPeriodic=0
    g242: BSplineCurve PolesCount=3 KnotsCount=2 Degree=2 IsPeriodic=0
    g243: LineSegment StartX=-30.2403 StartY=39.4638 StartZ=0 EndX=-30.2403 EndY=39.9037 EndZ=0
    g244: BSplineCurve PolesCount=3 KnotsCount=2 Degree=2 IsPeriodic=0
    g245: BSplineCurve PolesCount=3 KnotsCount=2 Degree=2 IsPeriodic=0
    g246: BSplineCurve PolesCount=3 KnotsCount=2 Degree=2 IsPeriodic=0
    g247: LineSegment StartX=-30.5522 StartY=40.199 StartZ=0 EndX=-30.2403 EndY=40.199 EndZ=0
    g248: LineSegment StartX=-30.2403 StartY=40.199 StartZ=0 EndX=-30.2403 EndY=40.6658 EndZ=0
    g249: BSplineCurve PolesCount=3 KnotsCount=2 Degree=2 IsPeriodic=0
    g250: BSplineCurve PolesCount=3 KnotsCount=2 Degree=2 IsPeriodic=0
    g251: LineSegment StartX=-29.9429 StartY=40.672 StartZ=0 EndX=-29.9429 EndY=40.2052 EndZ=0
    g252: LineSegment StartX=-29.9429 StartY=40.2052 StartZ=0 EndX=-28.9949 EndY=40.2052 EndZ=0
    g253: BSplineCurve PolesCount=3 KnotsCount=2 Degree=2 IsPeriodic=0
    g254: BSplineCurve PolesCount=3 KnotsCount=2 Degree=2 IsPeriodic=0
    g255: BSplineCurve PolesCount=3 KnotsCount=2 Degree=2 IsPeriodic=0
  constraints (2):
    c: Horizontal(g0)
    c: T21(g0,g1,g2)
FEATURE [PartDesign::Pocket] Pocket024
  BaseFeature = -> Pocket023
  Direction = (0,1,0)
  Length = 1
  Length2 = 5
  Profile = -> Sketch052
  ReferenceAxis = -> Sketch052 [N_Axis]
  Refine = true
  SideType = 0
  Suppressed = false
  Type = 0
  Type2 = 0
FEATURE [PartDesign::Body] Body006  label="CartographerV4_HeatSetInserts"
  AllowCompound = true
  Group = -> [Sketch044,Sketch045,Pad016,Pad017,Sketch046,MirroredSketch005,Clone2D006,Pocket020,AdditiveLoft010,Chamfer007,Sketch047,Pocket021,Sketch048,Sketch049,AdditiveLoft011,Sketch050,Pocket022,Sketch051,Pocket023,Sketch052,Pocket024]
  Origin = -> Origin016
  Placement = pos=(0,0,0) rot=(0,0,1;6.13955rad)
  Tip = -> Pocket024
